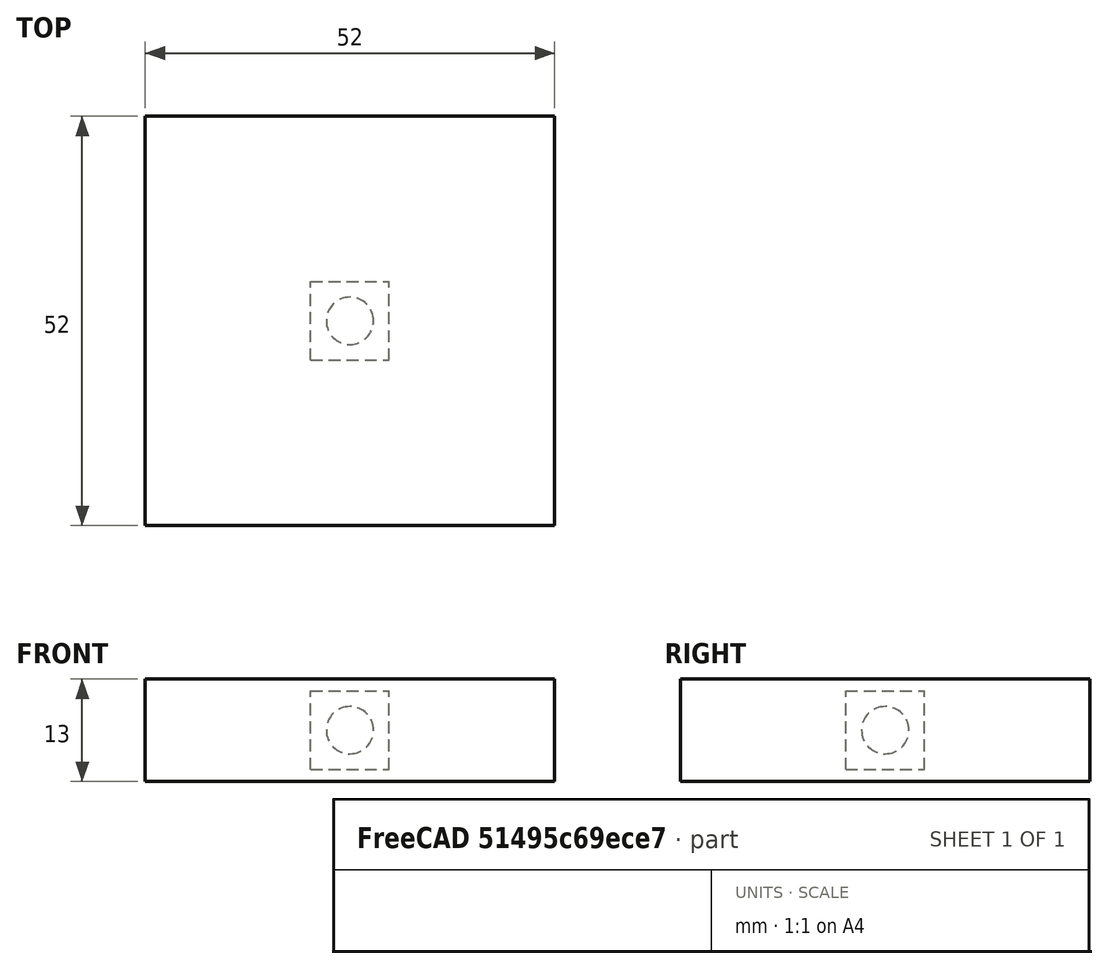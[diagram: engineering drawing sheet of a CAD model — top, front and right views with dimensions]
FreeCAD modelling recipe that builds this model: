
FCSTD DOCUMENT  (FreeCAD 0.21RUnknown)
Label: array-of-mother-daughter-vols-correct
License: All rights reserved
objects: App::DocumentObjectGroupPython×1251, Part::FeaturePython×5, App::Part×3
note: 3 computed .brp shape members not serialized (recipe doc carries the construction recipe); baked Part::Feature solids carry a one-line shape summary decoded from their .brp

FEATURE [App::DocumentObjectGroupPython] HALFPI  # scripted group (container) (typed FeaturePython)
  name = HALFPI
  value = pi/2.
FEATURE [App::DocumentObjectGroupPython] PI  # scripted group (container) (typed FeaturePython)
  name = PI
  value = 1.*pi
FEATURE [App::DocumentObjectGroupPython] TWOPI  # scripted group (container) (typed FeaturePython)
  name = TWOPI
  value = 2.*pi
FEATURE [App::DocumentObjectGroupPython] Constants  # scripted group (container) (typed FeaturePython)
  Group = -> [HALFPI,PI,TWOPI]
FEATURE [App::DocumentObjectGroupPython] Variables  # scripted group (container) (typed FeaturePython)
FEATURE [App::DocumentObjectGroupPython] Quantities  # scripted group (container) (typed FeaturePython)
FEATURE [App::DocumentObjectGroupPython] Isotopes  # scripted group (container) (typed FeaturePython)
FEATURE [App::DocumentObjectGroupPython] Elements  # scripted group (container) (typed FeaturePython)
FEATURE [App::DocumentObjectGroupPython] Matrix  # scripted group (container) (typed FeaturePython)
FEATURE [App::DocumentObjectGroupPython] Surfaces  # scripted group (container) (typed FeaturePython)
FEATURE [App::DocumentObjectGroupPython] Opticals  # scripted group (container) (typed FeaturePython)
  Group = -> [Matrix,Surfaces]
FEATURE [App::DocumentObjectGroupPython] G4Isotopes  # scripted group (container) (typed FeaturePython)
FEATURE [App::DocumentObjectGroupPython] H_element  # scripted group (container) (typed FeaturePython)
  Z = 1
  atom_value = 1.008
  formula = H
  name = H_element
FEATURE [App::DocumentObjectGroupPython] He_element  # scripted group (container) (typed FeaturePython)
  Z = 2
  atom_value = 4.0026
  formula = He
  name = He_element
FEATURE [App::DocumentObjectGroupPython] Li_element  # scripted group (container) (typed FeaturePython)
  Z = 3
  atom_value = 6.94
  formula = Li
  name = Li_element
FEATURE [App::DocumentObjectGroupPython] Be_element  # scripted group (container) (typed FeaturePython)
  Z = 4
  atom_value = 9.01218
  formula = Be
  name = Be_element
FEATURE [App::DocumentObjectGroupPython] B_element  # scripted group (container) (typed FeaturePython)
  Z = 5
  atom_value = 10.81
  formula = B
  name = B_element
FEATURE [App::DocumentObjectGroupPython] C_element  # scripted group (container) (typed FeaturePython)
  Z = 6
  atom_value = 12.011
  formula = C
  name = C_element
FEATURE [App::DocumentObjectGroupPython] N_element  # scripted group (container) (typed FeaturePython)
  Z = 7
  atom_value = 14.007
  formula = N
  name = N_element
FEATURE [App::DocumentObjectGroupPython] O_element  # scripted group (container) (typed FeaturePython)
  Z = 8
  atom_value = 15.999
  formula = O
  name = O_element
FEATURE [App::DocumentObjectGroupPython] F_element  # scripted group (container) (typed FeaturePython)
  Z = 9
  atom_value = 18.9984
  formula = F
  name = F_element
FEATURE [App::DocumentObjectGroupPython] Ne_element  # scripted group (container) (typed FeaturePython)
  Z = 10
  atom_value = 20.1797
  formula = Ne
  name = Ne_element
FEATURE [App::DocumentObjectGroupPython] Na_element  # scripted group (container) (typed FeaturePython)
  Z = 11
  atom_value = 22.9898
  formula = Na
  name = Na_element
FEATURE [App::DocumentObjectGroupPython] Mg_element  # scripted group (container) (typed FeaturePython)
  Z = 12
  atom_value = 24.305
  formula = Mg
  name = Mg_element
FEATURE [App::DocumentObjectGroupPython] Al_element  # scripted group (container) (typed FeaturePython)
  Z = 13
  atom_value = 26.9815
  formula = Al
  name = Al_element
FEATURE [App::DocumentObjectGroupPython] Si_element  # scripted group (container) (typed FeaturePython)
  Z = 14
  atom_value = 28.085
  formula = Si
  name = Si_element
FEATURE [App::DocumentObjectGroupPython] P_element  # scripted group (container) (typed FeaturePython)
  Z = 15
  atom_value = 30.9738
  formula = P
  name = P_element
FEATURE [App::DocumentObjectGroupPython] S_element  # scripted group (container) (typed FeaturePython)
  Z = 16
  atom_value = 32.06
  formula = S
  name = S_element
FEATURE [App::DocumentObjectGroupPython] Cl_element  # scripted group (container) (typed FeaturePython)
  Z = 17
  atom_value = 35.45
  formula = Cl
  name = Cl_element
FEATURE [App::DocumentObjectGroupPython] Ar_element  # scripted group (container) (typed FeaturePython)
  Z = 18
  atom_value = 39.95
  formula = Ar
  name = Ar_element
FEATURE [App::DocumentObjectGroupPython] K_element  # scripted group (container) (typed FeaturePython)
  Z = 19
  atom_value = 39.0983
  formula = K
  name = K_element
FEATURE [App::DocumentObjectGroupPython] Ca_element  # scripted group (container) (typed FeaturePython)
  Z = 20
  atom_value = 40.078
  formula = Ca
  name = Ca_element
FEATURE [App::DocumentObjectGroupPython] Sc_element  # scripted group (container) (typed FeaturePython)
  Z = 21
  atom_value = 44.9559
  formula = Sc
  name = Sc_element
FEATURE [App::DocumentObjectGroupPython] Ti_element  # scripted group (container) (typed FeaturePython)
  Z = 22
  atom_value = 47.867
  formula = Ti
  name = Ti_element
FEATURE [App::DocumentObjectGroupPython] V_element  # scripted group (container) (typed FeaturePython)
  Z = 23
  atom_value = 50.9415
  formula = V
  name = V_element
FEATURE [App::DocumentObjectGroupPython] Cr_element  # scripted group (container) (typed FeaturePython)
  Z = 24
  atom_value = 51.9961
  formula = Cr
  name = Cr_element
FEATURE [App::DocumentObjectGroupPython] Mn_element  # scripted group (container) (typed FeaturePython)
  Z = 25
  atom_value = 54.938
  formula = Mn
  name = Mn_element
FEATURE [App::DocumentObjectGroupPython] Fe_element  # scripted group (container) (typed FeaturePython)
  Z = 26
  atom_value = 55.845
  formula = Fe
  name = Fe_element
FEATURE [App::DocumentObjectGroupPython] Co_element  # scripted group (container) (typed FeaturePython)
  Z = 27
  atom_value = 58.9332
  formula = Co
  name = Co_element
FEATURE [App::DocumentObjectGroupPython] Ni_element  # scripted group (container) (typed FeaturePython)
  Z = 28
  atom_value = 58.6934
  formula = Ni
  name = Ni_element
FEATURE [App::DocumentObjectGroupPython] Cu_element  # scripted group (container) (typed FeaturePython)
  Z = 29
  atom_value = 63.546
  formula = Cu
  name = Cu_element
FEATURE [App::DocumentObjectGroupPython] Zn_element  # scripted group (container) (typed FeaturePython)
  Z = 30
  atom_value = 65.38
  formula = Zn
  name = Zn_element
FEATURE [App::DocumentObjectGroupPython] Ga_element  # scripted group (container) (typed FeaturePython)
  Z = 31
  atom_value = 69.723
  formula = Ga
  name = Ga_element
FEATURE [App::DocumentObjectGroupPython] Ge_element  # scripted group (container) (typed FeaturePython)
  Z = 32
  atom_value = 72.63
  formula = Ge
  name = Ge_element
FEATURE [App::DocumentObjectGroupPython] As_element  # scripted group (container) (typed FeaturePython)
  Z = 33
  atom_value = 74.9216
  formula = As
  name = As_element
FEATURE [App::DocumentObjectGroupPython] Se_element  # scripted group (container) (typed FeaturePython)
  Z = 34
  atom_value = 78.971
  formula = Se
  name = Se_element
FEATURE [App::DocumentObjectGroupPython] Br_element  # scripted group (container) (typed FeaturePython)
  Z = 35
  atom_value = 79.904
  formula = Br
  name = Br_element
FEATURE [App::DocumentObjectGroupPython] Kr_element  # scripted group (container) (typed FeaturePython)
  Z = 36
  atom_value = 83.798
  formula = Kr
  name = Kr_element
FEATURE [App::DocumentObjectGroupPython] Rb_element  # scripted group (container) (typed FeaturePython)
  Z = 37
  atom_value = 85.4678
  formula = Rb
  name = Rb_element
FEATURE [App::DocumentObjectGroupPython] Sr_element  # scripted group (container) (typed FeaturePython)
  Z = 38
  atom_value = 87.62
  formula = Sr
  name = Sr_element
FEATURE [App::DocumentObjectGroupPython] Y_element  # scripted group (container) (typed FeaturePython)
  Z = 39
  atom_value = 88.9058
  formula = Y
  name = Y_element
FEATURE [App::DocumentObjectGroupPython] Zr_element  # scripted group (container) (typed FeaturePython)
  Z = 40
  atom_value = 91.224
  formula = Zr
  name = Zr_element
FEATURE [App::DocumentObjectGroupPython] Nb_element  # scripted group (container) (typed FeaturePython)
  Z = 41
  atom_value = 92.9064
  formula = Nb
  name = Nb_element
FEATURE [App::DocumentObjectGroupPython] Mo_element  # scripted group (container) (typed FeaturePython)
  Z = 42
  atom_value = 95.95
  formula = Mo
  name = Mo_element
FEATURE [App::DocumentObjectGroupPython] Tc_element  # scripted group (container) (typed FeaturePython)
  Z = 43
  atom_value = 97
  formula = Tc
  name = Tc_element
FEATURE [App::DocumentObjectGroupPython] Ru_element  # scripted group (container) (typed FeaturePython)
  Z = 44
  atom_value = 101.07
  formula = Ru
  name = Ru_element
FEATURE [App::DocumentObjectGroupPython] Rh_element  # scripted group (container) (typed FeaturePython)
  Z = 45
  atom_value = 102.905
  formula = Rh
  name = Rh_element
FEATURE [App::DocumentObjectGroupPython] Pd_element  # scripted group (container) (typed FeaturePython)
  Z = 46
  atom_value = 106.42
  formula = Pd
  name = Pd_element
FEATURE [App::DocumentObjectGroupPython] Ag_element  # scripted group (container) (typed FeaturePython)
  Z = 47
  atom_value = 107.868
  formula = Ag
  name = Ag_element
FEATURE [App::DocumentObjectGroupPython] Cd_element  # scripted group (container) (typed FeaturePython)
  Z = 48
  atom_value = 112.414
  formula = Cd
  name = Cd_element
FEATURE [App::DocumentObjectGroupPython] In_element  # scripted group (container) (typed FeaturePython)
  Z = 49
  atom_value = 114.818
  formula = In
  name = In_element
FEATURE [App::DocumentObjectGroupPython] Sn_element  # scripted group (container) (typed FeaturePython)
  Z = 50
  atom_value = 118.71
  formula = Sn
  name = Sn_element
FEATURE [App::DocumentObjectGroupPython] Sb_element  # scripted group (container) (typed FeaturePython)
  Z = 51
  atom_value = 121.76
  formula = Sb
  name = Sb_element
FEATURE [App::DocumentObjectGroupPython] Te_element  # scripted group (container) (typed FeaturePython)
  Z = 52
  atom_value = 127.6
  formula = Te
  name = Te_element
FEATURE [App::DocumentObjectGroupPython] I_element  # scripted group (container) (typed FeaturePython)
  Z = 53
  atom_value = 126.904
  formula = I
  name = I_element
FEATURE [App::DocumentObjectGroupPython] Xe_element  # scripted group (container) (typed FeaturePython)
  Z = 54
  atom_value = 131.293
  formula = Xe
  name = Xe_element
FEATURE [App::DocumentObjectGroupPython] Cs_element  # scripted group (container) (typed FeaturePython)
  Z = 55
  atom_value = 132.905
  formula = Cs
  name = Cs_element
FEATURE [App::DocumentObjectGroupPython] Ba_element  # scripted group (container) (typed FeaturePython)
  Z = 56
  atom_value = 137.327
  formula = Ba
  name = Ba_element
FEATURE [App::DocumentObjectGroupPython] La_element  # scripted group (container) (typed FeaturePython)
  Z = 57
  atom_value = 138.905
  formula = La
  name = La_element
FEATURE [App::DocumentObjectGroupPython] Ce_element  # scripted group (container) (typed FeaturePython)
  Z = 58
  atom_value = 140.116
  formula = Ce
  name = Ce_element
FEATURE [App::DocumentObjectGroupPython] Pr_element  # scripted group (container) (typed FeaturePython)
  Z = 59
  atom_value = 140.908
  formula = Pr
  name = Pr_element
FEATURE [App::DocumentObjectGroupPython] Nd_element  # scripted group (container) (typed FeaturePython)
  Z = 60
  atom_value = 144.242
  formula = Nd
  name = Nd_element
FEATURE [App::DocumentObjectGroupPython] Pm_element  # scripted group (container) (typed FeaturePython)
  Z = 61
  atom_value = 145
  formula = Pm
  name = Pm_element
FEATURE [App::DocumentObjectGroupPython] Sm_element  # scripted group (container) (typed FeaturePython)
  Z = 62
  atom_value = 150.36
  formula = Sm
  name = Sm_element
FEATURE [App::DocumentObjectGroupPython] Eu_element  # scripted group (container) (typed FeaturePython)
  Z = 63
  atom_value = 151.964
  formula = Eu
  name = Eu_element
FEATURE [App::DocumentObjectGroupPython] Gd_element  # scripted group (container) (typed FeaturePython)
  Z = 64
  atom_value = 157.25
  formula = Gd
  name = Gd_element
FEATURE [App::DocumentObjectGroupPython] Tb_element  # scripted group (container) (typed FeaturePython)
  Z = 65
  atom_value = 158.925
  formula = Tb
  name = Tb_element
FEATURE [App::DocumentObjectGroupPython] Dy_element  # scripted group (container) (typed FeaturePython)
  Z = 66
  atom_value = 162.5
  formula = Dy
  name = Dy_element
FEATURE [App::DocumentObjectGroupPython] Ho_element  # scripted group (container) (typed FeaturePython)
  Z = 67
  atom_value = 164.93
  formula = Ho
  name = Ho_element
FEATURE [App::DocumentObjectGroupPython] Er_element  # scripted group (container) (typed FeaturePython)
  Z = 68
  atom_value = 167.259
  formula = Er
  name = Er_element
FEATURE [App::DocumentObjectGroupPython] Tm_element  # scripted group (container) (typed FeaturePython)
  Z = 69
  atom_value = 168.934
  formula = Tm
  name = Tm_element
FEATURE [App::DocumentObjectGroupPython] Yb_element  # scripted group (container) (typed FeaturePython)
  Z = 70
  atom_value = 173.045
  formula = Yb
  name = Yb_element
FEATURE [App::DocumentObjectGroupPython] Lu_element  # scripted group (container) (typed FeaturePython)
  Z = 71
  atom_value = 174.967
  formula = Lu
  name = Lu_element
FEATURE [App::DocumentObjectGroupPython] Hf_element  # scripted group (container) (typed FeaturePython)
  Z = 72
  atom_value = 178.49
  formula = Hf
  name = Hf_element
FEATURE [App::DocumentObjectGroupPython] Ta_element  # scripted group (container) (typed FeaturePython)
  Z = 73
  atom_value = 180.948
  formula = Ta
  name = Ta_element
FEATURE [App::DocumentObjectGroupPython] W_element  # scripted group (container) (typed FeaturePython)
  Z = 74
  atom_value = 183.84
  formula = W
  name = W_element
FEATURE [App::DocumentObjectGroupPython] Re_element  # scripted group (container) (typed FeaturePython)
  Z = 75
  atom_value = 186.207
  formula = Re
  name = Re_element
FEATURE [App::DocumentObjectGroupPython] Os_element  # scripted group (container) (typed FeaturePython)
  Z = 76
  atom_value = 190.23
  formula = Os
  name = Os_element
FEATURE [App::DocumentObjectGroupPython] Ir_element  # scripted group (container) (typed FeaturePython)
  Z = 77
  atom_value = 192.217
  formula = Ir
  name = Ir_element
FEATURE [App::DocumentObjectGroupPython] Pt_element  # scripted group (container) (typed FeaturePython)
  Z = 78
  atom_value = 195.084
  formula = Pt
  name = Pt_element
FEATURE [App::DocumentObjectGroupPython] Au_element  # scripted group (container) (typed FeaturePython)
  Z = 79
  atom_value = 196.967
  formula = Au
  name = Au_element
FEATURE [App::DocumentObjectGroupPython] Hg_element  # scripted group (container) (typed FeaturePython)
  Z = 80
  atom_value = 200.592
  formula = Hg
  name = Hg_element
FEATURE [App::DocumentObjectGroupPython] Tl_element  # scripted group (container) (typed FeaturePython)
  Z = 81
  atom_value = 204.38
  formula = Tl
  name = Tl_element
FEATURE [App::DocumentObjectGroupPython] Pb_element  # scripted group (container) (typed FeaturePython)
  Z = 82
  atom_value = 207.2
  formula = Pb
  name = Pb_element
FEATURE [App::DocumentObjectGroupPython] Bi_element  # scripted group (container) (typed FeaturePython)
  Z = 83
  atom_value = 208.98
  formula = Bi
  name = Bi_element
FEATURE [App::DocumentObjectGroupPython] Po_element  # scripted group (container) (typed FeaturePython)
  Z = 84
  atom_value = 209
  formula = Po
  name = Po_element
FEATURE [App::DocumentObjectGroupPython] At_element  # scripted group (container) (typed FeaturePython)
  Z = 85
  atom_value = 210
  formula = At
  name = At_element
FEATURE [App::DocumentObjectGroupPython] Rn_element  # scripted group (container) (typed FeaturePython)
  Z = 86
  atom_value = 222
  formula = Rn
  name = Rn_element
FEATURE [App::DocumentObjectGroupPython] Fr_element  # scripted group (container) (typed FeaturePython)
  Z = 87
  atom_value = 223
  formula = Fr
  name = Fr_element
FEATURE [App::DocumentObjectGroupPython] Ra_element  # scripted group (container) (typed FeaturePython)
  Z = 88
  atom_value = 226
  formula = Ra
  name = Ra_element
FEATURE [App::DocumentObjectGroupPython] Ac_element  # scripted group (container) (typed FeaturePython)
  Z = 89
  atom_value = 227
  formula = Ac
  name = Ac_element
FEATURE [App::DocumentObjectGroupPython] Th_element  # scripted group (container) (typed FeaturePython)
  Z = 90
  atom_value = 232.038
  formula = Th
  name = Th_element
FEATURE [App::DocumentObjectGroupPython] Pa_element  # scripted group (container) (typed FeaturePython)
  Z = 91
  atom_value = 231.036
  formula = Pa
  name = Pa_element
FEATURE [App::DocumentObjectGroupPython] U_element  # scripted group (container) (typed FeaturePython)
  Z = 92
  atom_value = 238.029
  formula = U
  name = U_element
FEATURE [App::DocumentObjectGroupPython] Np_element  # scripted group (container) (typed FeaturePython)
  Z = 93
  atom_value = 237
  formula = Np
  name = Np_element
FEATURE [App::DocumentObjectGroupPython] Pu_element  # scripted group (container) (typed FeaturePython)
  Z = 94
  atom_value = 244
  formula = Pu
  name = Pu_element
FEATURE [App::DocumentObjectGroupPython] Am_element  # scripted group (container) (typed FeaturePython)
  Z = 95
  atom_value = 243
  formula = Am
  name = Am_element
FEATURE [App::DocumentObjectGroupPython] Cm_element  # scripted group (container) (typed FeaturePython)
  Z = 96
  atom_value = 247
  formula = Cm
  name = Cm_element
FEATURE [App::DocumentObjectGroupPython] Bk_element  # scripted group (container) (typed FeaturePython)
  Z = 97
  atom_value = 247
  formula = Bk
  name = Bk_element
FEATURE [App::DocumentObjectGroupPython] Cf_element  # scripted group (container) (typed FeaturePython)
  Z = 98
  atom_value = 251
  formula = Cf
  name = Cf_element
FEATURE [App::DocumentObjectGroupPython] G4Elements  # scripted group (container) (typed FeaturePython)
  Group = -> [H_element,He_element,Li_element,Be_element,B_element,C_element,N_element,O_element,F_element,Ne_element,Na_element,Mg_element,Al_element,Si_element,P_element,S_element,Cl_element,Ar_element,K_element,Ca_element,Sc_element,Ti_element,V_element,Cr_element,Mn_element,Fe_element,Co_element,Ni_element,Cu_element,Zn_element,Ga_element,Ge_element,As_element,Se_element,Br_element,Kr_element,Rb_element,+61 more]
FEATURE [App::DocumentObjectGroupPython] H_element001  label="H_element : 0.101"  # scripted group (container) (typed FeaturePython)
  n = 0.101327
FEATURE [App::DocumentObjectGroupPython] C_element001  label="C_element : 0.775"  # scripted group (container) (typed FeaturePython)
  n = 0.7755
FEATURE [App::DocumentObjectGroupPython] N_element001  label="N_element : 0.035"  # scripted group (container) (typed FeaturePython)
  n = 0.035057
FEATURE [App::DocumentObjectGroupPython] O_element001  label="O_element : 0.052"  # scripted group (container) (typed FeaturePython)
  n = 0.0523159
FEATURE [App::DocumentObjectGroupPython] F_element001  label="F_element : 0.017"  # scripted group (container) (typed FeaturePython)
  n = 0.017422
FEATURE [App::DocumentObjectGroupPython] Ca_element001  label="Ca_element : 0.018"  # scripted group (container) (typed FeaturePython)
  n = 0.018378
FEATURE [App::DocumentObjectGroupPython] G4_A_150_TISSUE  label="G4_A-150_TISSUE"  # scripted group (container) (typed FeaturePython)
  Dunit = g/cm3
  Dvalue = 1.127
  Group = -> [H_element001,C_element001,N_element001,O_element001,F_element001,Ca_element001]
  conduct = 2
  density = 1
  expand = 3
  formula = G4_A-150_TISSUE
  name = G4_A-150_TISSUE
  specific = 4
FEATURE [App::DocumentObjectGroupPython] C_element002  label="C_element : 3"  # scripted group (container) (typed FeaturePython)
  n = 3
  ref = C_element
FEATURE [App::DocumentObjectGroupPython] H_element002  label="H_element : 6"  # scripted group (container) (typed FeaturePython)
  n = 6
  ref = H_element
FEATURE [App::DocumentObjectGroupPython] O_element002  label="O_element : 1"  # scripted group (container) (typed FeaturePython)
  n = 1
  ref = O_element
FEATURE [App::DocumentObjectGroupPython] G4_ACETONE  # scripted group (container) (typed FeaturePython)
  Dunit = g/cm3
  Dvalue = 0.7899
  Group = -> [C_element002,H_element002,O_element002]
  conduct = 2
  density = 1
  expand = 3
  formula = G4_ACETONE
  name = G4_ACETONE
  specific = 4
FEATURE [App::DocumentObjectGroupPython] C_element003  label="C_element : 2"  # scripted group (container) (typed FeaturePython)
  n = 2
  ref = C_element
FEATURE [App::DocumentObjectGroupPython] H_element003  label="H_element : 2"  # scripted group (container) (typed FeaturePython)
  n = 2
  ref = H_element
FEATURE [App::DocumentObjectGroupPython] G4_ACETYLENE  # scripted group (container) (typed FeaturePython)
  Dunit = g/cm3
  Dvalue = 0.0010967
  Group = -> [C_element003,H_element003]
  conduct = 2
  density = 1
  expand = 3
  formula = G4_ACETYLENE
  name = G4_ACETYLENE
  specific = 4
FEATURE [App::DocumentObjectGroupPython] C_element004  label="C_element : 5"  # scripted group (container) (typed FeaturePython)
  n = 5
  ref = C_element
FEATURE [App::DocumentObjectGroupPython] H_element004  label="H_element : 5"  # scripted group (container) (typed FeaturePython)
  n = 5
  ref = H_element
FEATURE [App::DocumentObjectGroupPython] N_element002  label="N_element : 5"  # scripted group (container) (typed FeaturePython)
  n = 5
  ref = N_element
FEATURE [App::DocumentObjectGroupPython] G4_ADENINE  # scripted group (container) (typed FeaturePython)
  Dunit = g/cm3
  Dvalue = 1.6
  Group = -> [C_element004,H_element004,N_element002]
  conduct = 2
  density = 1
  expand = 3
  formula = G4_ADENINE
  name = G4_ADENINE
  specific = 4
FEATURE [App::DocumentObjectGroupPython] H_element005  label="H_element : 0.114"  # scripted group (container) (typed FeaturePython)
  n = 0.114
FEATURE [App::DocumentObjectGroupPython] C_element005  label="C_element : 0.598"  # scripted group (container) (typed FeaturePython)
  n = 0.598
FEATURE [App::DocumentObjectGroupPython] N_element003  label="N_element : 0.007"  # scripted group (container) (typed FeaturePython)
  n = 0.007
FEATURE [App::DocumentObjectGroupPython] O_element003  label="O_element : 0.278"  # scripted group (container) (typed FeaturePython)
  n = 0.278
FEATURE [App::DocumentObjectGroupPython] Na_element001  label="Na_element : 0.001"  # scripted group (container) (typed FeaturePython)
  n = 0.001
FEATURE [App::DocumentObjectGroupPython] S_element001  label="S_element : 0.001"  # scripted group (container) (typed FeaturePython)
  n = 0.001
FEATURE [App::DocumentObjectGroupPython] Cl_element001  label="Cl_element : 0.001"  # scripted group (container) (typed FeaturePython)
  n = 0.001
FEATURE [App::DocumentObjectGroupPython] G4_ADIPOSE_TISSUE_ICRP  # scripted group (container) (typed FeaturePython)
  Dunit = g/cm3
  Dvalue = 0.95
  Group = -> [H_element005,C_element005,N_element003,O_element003,Na_element001,S_element001,Cl_element001]
  conduct = 2
  density = 1
  expand = 3
  formula = G4_ADIPOSE_TISSUE_ICRP
  name = G4_ADIPOSE_TISSUE_ICRP
  specific = 4
FEATURE [App::DocumentObjectGroupPython] C_element006  label="C_element : 0.000"  # scripted group (container) (typed FeaturePython)
  n = 0.000124
FEATURE [App::DocumentObjectGroupPython] N_element004  label="N_element : 0.755"  # scripted group (container) (typed FeaturePython)
  n = 0.755268
FEATURE [App::DocumentObjectGroupPython] O_element004  label="O_element : 0.232"  # scripted group (container) (typed FeaturePython)
  n = 0.231781
FEATURE [App::DocumentObjectGroupPython] Ar_element001  label="Ar_element : 0.013"  # scripted group (container) (typed FeaturePython)
  n = 0.012827
FEATURE [App::DocumentObjectGroupPython] G4_AIR  # scripted group (container) (typed FeaturePython)
  Dunit = g/cm3
  Dvalue = 0.00120479
  Group = -> [C_element006,N_element004,O_element004,Ar_element001]
  conduct = 2
  density = 1
  expand = 3
  formula = G4_AIR
  name = G4_AIR
  specific = 4
FEATURE [App::DocumentObjectGroupPython] C_element007  label="C_element : 006"  # scripted group (container) (typed FeaturePython)
  n = 3
  ref = C_element
FEATURE [App::DocumentObjectGroupPython] H_element006  label="H_element : 7"  # scripted group (container) (typed FeaturePython)
  n = 7
  ref = H_element
FEATURE [App::DocumentObjectGroupPython] N_element005  label="N_element : 1"  # scripted group (container) (typed FeaturePython)
  n = 1
  ref = N_element
FEATURE [App::DocumentObjectGroupPython] O_element005  label="O_element : 2"  # scripted group (container) (typed FeaturePython)
  n = 2
  ref = O_element
FEATURE [App::DocumentObjectGroupPython] G4_ALANINE  # scripted group (container) (typed FeaturePython)
  Dunit = g/cm3
  Dvalue = 1.42
  Group = -> [C_element007,H_element006,N_element005,O_element005]
  conduct = 2
  density = 1
  expand = 3
  formula = G4_ALANINE
  name = G4_ALANINE
  specific = 4
FEATURE [App::DocumentObjectGroupPython] Al_element001  label="Al_element : 2"  # scripted group (container) (typed FeaturePython)
  n = 2
  ref = Al_element
FEATURE [App::DocumentObjectGroupPython] O_element006  label="O_element : 3"  # scripted group (container) (typed FeaturePython)
  n = 3
  ref = O_element
FEATURE [App::DocumentObjectGroupPython] G4_ALUMINUM_OXIDE  # scripted group (container) (typed FeaturePython)
  Dunit = g/cm3
  Dvalue = 3.97
  Group = -> [Al_element001,O_element006]
  conduct = 2
  density = 1
  expand = 3
  formula = G4_ALUMINUM_OXIDE
  name = G4_ALUMINUM_OXIDE
  specific = 4
FEATURE [App::DocumentObjectGroupPython] H_element007  label="H_element : 0.106"  # scripted group (container) (typed FeaturePython)
  n = 0.10593
FEATURE [App::DocumentObjectGroupPython] C_element008  label="C_element : 0.789"  # scripted group (container) (typed FeaturePython)
  n = 0.788974
FEATURE [App::DocumentObjectGroupPython] O_element007  label="O_element : 0.105"  # scripted group (container) (typed FeaturePython)
  n = 0.105096
FEATURE [App::DocumentObjectGroupPython] G4_AMBER  # scripted group (container) (typed FeaturePython)
  Dunit = g/cm3
  Dvalue = 1.1
  Group = -> [H_element007,C_element008,O_element007]
  conduct = 2
  density = 1
  expand = 3
  formula = G4_AMBER
  name = G4_AMBER
  specific = 4
FEATURE [App::DocumentObjectGroupPython] N_element006  label="N_element : 006"  # scripted group (container) (typed FeaturePython)
  n = 1
  ref = N_element
FEATURE [App::DocumentObjectGroupPython] H_element008  label="H_element : 3"  # scripted group (container) (typed FeaturePython)
  n = 3
  ref = H_element
FEATURE [App::DocumentObjectGroupPython] G4_AMMONIA  # scripted group (container) (typed FeaturePython)
  Dunit = g/cm3
  Dvalue = 0.000826019
  Group = -> [N_element006,H_element008]
  conduct = 2
  density = 1
  expand = 3
  formula = G4_AMMONIA
  name = G4_AMMONIA
  specific = 4
FEATURE [App::DocumentObjectGroupPython] C_element009  label="C_element : 6"  # scripted group (container) (typed FeaturePython)
  n = 6
  ref = C_element
FEATURE [App::DocumentObjectGroupPython] H_element009  label="H_element : 008"  # scripted group (container) (typed FeaturePython)
  n = 7
  ref = H_element
FEATURE [App::DocumentObjectGroupPython] N_element007  label="N_element : 007"  # scripted group (container) (typed FeaturePython)
  n = 1
  ref = N_element
FEATURE [App::DocumentObjectGroupPython] G4_ANILINE  # scripted group (container) (typed FeaturePython)
  Dunit = g/cm3
  Dvalue = 1.0235
  Group = -> [C_element009,H_element009,N_element007]
  conduct = 2
  density = 1
  expand = 3
  formula = G4_ANILINE
  name = G4_ANILINE
  specific = 4
FEATURE [App::DocumentObjectGroupPython] C_element010  label="C_element : 14"  # scripted group (container) (typed FeaturePython)
  n = 14
  ref = C_element
FEATURE [App::DocumentObjectGroupPython] H_element010  label="H_element : 10"  # scripted group (container) (typed FeaturePython)
  n = 10
  ref = H_element
FEATURE [App::DocumentObjectGroupPython] G4_ANTHRACENE  # scripted group (container) (typed FeaturePython)
  Dunit = g/cm3
  Dvalue = 1.283
  Group = -> [C_element010,H_element010]
  conduct = 2
  density = 1
  expand = 3
  formula = G4_ANTHRACENE
  name = G4_ANTHRACENE
  specific = 4
FEATURE [App::DocumentObjectGroupPython] H_element011  label="H_element : 0.065"  # scripted group (container) (typed FeaturePython)
  n = 0.0654709
FEATURE [App::DocumentObjectGroupPython] C_element011  label="C_element : 0.537"  # scripted group (container) (typed FeaturePython)
  n = 0.536944
FEATURE [App::DocumentObjectGroupPython] N_element008  label="N_element : 0.021"  # scripted group (container) (typed FeaturePython)
  n = 0.0215
FEATURE [App::DocumentObjectGroupPython] O_element008  label="O_element : 0.032"  # scripted group (container) (typed FeaturePython)
  n = 0.032085
FEATURE [App::DocumentObjectGroupPython] F_element002  label="F_element : 0.167"  # scripted group (container) (typed FeaturePython)
  n = 0.167411
FEATURE [App::DocumentObjectGroupPython] Ca_element002  label="Ca_element : 0.177"  # scripted group (container) (typed FeaturePython)
  n = 0.176589
FEATURE [App::DocumentObjectGroupPython] G4_B_100_BONE  label="G4_B-100_BONE"  # scripted group (container) (typed FeaturePython)
  Dunit = g/cm3
  Dvalue = 1.45
  Group = -> [H_element011,C_element011,N_element008,O_element008,F_element002,Ca_element002]
  conduct = 2
  density = 1
  expand = 3
  formula = G4_B-100_BONE
  name = G4_B-100_BONE
  specific = 4
FEATURE [App::DocumentObjectGroupPython] H_element012  label="H_element : 0.057"  # scripted group (container) (typed FeaturePython)
  n = 0.057441
FEATURE [App::DocumentObjectGroupPython] C_element012  label="C_element : 0.790"  # scripted group (container) (typed FeaturePython)
  n = 0.774591
FEATURE [App::DocumentObjectGroupPython] O_element009  label="O_element : 0.168"  # scripted group (container) (typed FeaturePython)
  n = 0.167968
FEATURE [App::DocumentObjectGroupPython] G4_BAKELITE  # scripted group (container) (typed FeaturePython)
  Dunit = g/cm3
  Dvalue = 1.25
  Group = -> [H_element012,C_element012,O_element009]
  conduct = 2
  density = 1
  expand = 3
  formula = G4_BAKELITE
  name = G4_BAKELITE
  specific = 4
FEATURE [App::DocumentObjectGroupPython] Ba_element001  label="Ba_element : 1"  # scripted group (container) (typed FeaturePython)
  n = 1
  ref = Ba_element
FEATURE [App::DocumentObjectGroupPython] F_element003  label="F_element : 2"  # scripted group (container) (typed FeaturePython)
  n = 2
  ref = F_element
FEATURE [App::DocumentObjectGroupPython] G4_BARIUM_FLUORIDE  # scripted group (container) (typed FeaturePython)
  Dunit = g/cm3
  Dvalue = 4.89
  Group = -> [Ba_element001,F_element003]
  conduct = 2
  density = 1
  expand = 3
  formula = G4_BARIUM_FLUORIDE
  name = G4_BARIUM_FLUORIDE
  specific = 4
FEATURE [App::DocumentObjectGroupPython] Ba_element002  label="Ba_element : 002"  # scripted group (container) (typed FeaturePython)
  n = 1
  ref = Ba_element
FEATURE [App::DocumentObjectGroupPython] S_element002  label="S_element : 1"  # scripted group (container) (typed FeaturePython)
  n = 1
  ref = S_element
FEATURE [App::DocumentObjectGroupPython] O_element010  label="O_element : 4"  # scripted group (container) (typed FeaturePython)
  n = 4
  ref = O_element
FEATURE [App::DocumentObjectGroupPython] G4_BARIUM_SULFATE  # scripted group (container) (typed FeaturePython)
  Dunit = g/cm3
  Dvalue = 4.5
  Group = -> [Ba_element002,S_element002,O_element010]
  conduct = 2
  density = 1
  expand = 3
  formula = G4_BARIUM_SULFATE
  name = G4_BARIUM_SULFATE
  specific = 4
FEATURE [App::DocumentObjectGroupPython] C_element013  label="C_element : 007"  # scripted group (container) (typed FeaturePython)
  n = 6
  ref = C_element
FEATURE [App::DocumentObjectGroupPython] H_element013  label="H_element : 009"  # scripted group (container) (typed FeaturePython)
  n = 6
  ref = H_element
FEATURE [App::DocumentObjectGroupPython] G4_BENZENE  # scripted group (container) (typed FeaturePython)
  Dunit = g/cm3
  Dvalue = 0.87865
  Group = -> [C_element013,H_element013]
  conduct = 2
  density = 1
  expand = 3
  formula = G4_BENZENE
  name = G4_BENZENE
  specific = 4
FEATURE [App::DocumentObjectGroupPython] Be_element001  label="Be_element : 1"  # scripted group (container) (typed FeaturePython)
  n = 1
  ref = Be_element
FEATURE [App::DocumentObjectGroupPython] O_element011  label="O_element : 005"  # scripted group (container) (typed FeaturePython)
  n = 1
  ref = O_element
FEATURE [App::DocumentObjectGroupPython] G4_BERYLLIUM_OXIDE  # scripted group (container) (typed FeaturePython)
  Dunit = g/cm3
  Dvalue = 3.01
  Group = -> [Be_element001,O_element011]
  conduct = 2
  density = 1
  expand = 3
  formula = G4_BERYLLIUM_OXIDE
  name = G4_BERYLLIUM_OXIDE
  specific = 4
FEATURE [App::DocumentObjectGroupPython] Bi_element001  label="Bi_element : 4"  # scripted group (container) (typed FeaturePython)
  n = 4
  ref = Bi_element
FEATURE [App::DocumentObjectGroupPython] Ge_element001  label="Ge_element : 3"  # scripted group (container) (typed FeaturePython)
  n = 3
  ref = Ge_element
FEATURE [App::DocumentObjectGroupPython] O_element012  label="O_element : 12"  # scripted group (container) (typed FeaturePython)
  n = 12
  ref = O_element
FEATURE [App::DocumentObjectGroupPython] G4_BGO  # scripted group (container) (typed FeaturePython)
  Dunit = g/cm3
  Dvalue = 7.13
  Group = -> [Bi_element001,Ge_element001,O_element012]
  conduct = 2
  density = 1
  expand = 3
  formula = G4_BGO
  name = G4_BGO
  specific = 4
FEATURE [App::DocumentObjectGroupPython] H_element014  label="H_element : 0.102"  # scripted group (container) (typed FeaturePython)
  n = 0.102
FEATURE [App::DocumentObjectGroupPython] C_element014  label="C_element : 0.110"  # scripted group (container) (typed FeaturePython)
  n = 0.11
FEATURE [App::DocumentObjectGroupPython] N_element009  label="N_element : 0.033"  # scripted group (container) (typed FeaturePython)
  n = 0.033
FEATURE [App::DocumentObjectGroupPython] O_element013  label="O_element : 0.745"  # scripted group (container) (typed FeaturePython)
  n = 0.745
FEATURE [App::DocumentObjectGroupPython] Na_element002  label="Na_element : 0.002"  # scripted group (container) (typed FeaturePython)
  n = 0.001
FEATURE [App::DocumentObjectGroupPython] P_element001  label="P_element : 0.001"  # scripted group (container) (typed FeaturePython)
  n = 0.001
FEATURE [App::DocumentObjectGroupPython] S_element003  label="S_element : 0.002"  # scripted group (container) (typed FeaturePython)
  n = 0.002
FEATURE [App::DocumentObjectGroupPython] Cl_element002  label="Cl_element : 0.003"  # scripted group (container) (typed FeaturePython)
  n = 0.003
FEATURE [App::DocumentObjectGroupPython] K_element001  label="K_element : 0.002"  # scripted group (container) (typed FeaturePython)
  n = 0.002
FEATURE [App::DocumentObjectGroupPython] Fe_element001  label="Fe_element : 0.001"  # scripted group (container) (typed FeaturePython)
  n = 0.001
FEATURE [App::DocumentObjectGroupPython] G4_BLOOD_ICRP  # scripted group (container) (typed FeaturePython)
  Dunit = g/cm3
  Dvalue = 1.06
  Group = -> [H_element014,C_element014,N_element009,O_element013,Na_element002,P_element001,S_element003,Cl_element002,K_element001,Fe_element001]
  conduct = 2
  density = 1
  expand = 3
  formula = G4_BLOOD_ICRP
  name = G4_BLOOD_ICRP
  specific = 4
FEATURE [App::DocumentObjectGroupPython] H_element015  label="H_element : 0.064"  # scripted group (container) (typed FeaturePython)
  n = 0.064
FEATURE [App::DocumentObjectGroupPython] C_element015  label="C_element : 0.278"  # scripted group (container) (typed FeaturePython)
  n = 0.278
FEATURE [App::DocumentObjectGroupPython] N_element010  label="N_element : 0.027"  # scripted group (container) (typed FeaturePython)
  n = 0.027
FEATURE [App::DocumentObjectGroupPython] O_element014  label="O_element : 0.410"  # scripted group (container) (typed FeaturePython)
  n = 0.41
FEATURE [App::DocumentObjectGroupPython] Mg_element001  label="Mg_element : 0.002"  # scripted group (container) (typed FeaturePython)
  n = 0.002
FEATURE [App::DocumentObjectGroupPython] P_element002  label="P_element : 0.070"  # scripted group (container) (typed FeaturePython)
  n = 0.07
FEATURE [App::DocumentObjectGroupPython] S_element004  label="S_element : 0.003"  # scripted group (container) (typed FeaturePython)
  n = 0.002
FEATURE [App::DocumentObjectGroupPython] Ca_element003  label="Ca_element : 0.147"  # scripted group (container) (typed FeaturePython)
  n = 0.147
FEATURE [App::DocumentObjectGroupPython] G4_BONE_COMPACT_ICRU  # scripted group (container) (typed FeaturePython)
  Dunit = g/cm3
  Dvalue = 1.85
  Group = -> [H_element015,C_element015,N_element010,O_element014,Mg_element001,P_element002,S_element004,Ca_element003]
  conduct = 2
  density = 1
  expand = 3
  formula = G4_BONE_COMPACT_ICRU
  name = G4_BONE_COMPACT_ICRU
  specific = 4
FEATURE [App::DocumentObjectGroupPython] H_element016  label="H_element : 0.034"  # scripted group (container) (typed FeaturePython)
  n = 0.034
FEATURE [App::DocumentObjectGroupPython] C_element016  label="C_element : 0.155"  # scripted group (container) (typed FeaturePython)
  n = 0.155
FEATURE [App::DocumentObjectGroupPython] N_element011  label="N_element : 0.042"  # scripted group (container) (typed FeaturePython)
  n = 0.042
FEATURE [App::DocumentObjectGroupPython] O_element015  label="O_element : 0.435"  # scripted group (container) (typed FeaturePython)
  n = 0.435
FEATURE [App::DocumentObjectGroupPython] Na_element003  label="Na_element : 0.003"  # scripted group (container) (typed FeaturePython)
  n = 0.001
FEATURE [App::DocumentObjectGroupPython] Mg_element002  label="Mg_element : 0.003"  # scripted group (container) (typed FeaturePython)
  n = 0.002
FEATURE [App::DocumentObjectGroupPython] P_element003  label="P_element : 0.103"  # scripted group (container) (typed FeaturePython)
  n = 0.103
FEATURE [App::DocumentObjectGroupPython] S_element005  label="S_element : 0.004"  # scripted group (container) (typed FeaturePython)
  n = 0.003
FEATURE [App::DocumentObjectGroupPython] Ca_element004  label="Ca_element : 0.225"  # scripted group (container) (typed FeaturePython)
  n = 0.225
FEATURE [App::DocumentObjectGroupPython] G4_BONE_CORTICAL_ICRP  # scripted group (container) (typed FeaturePython)
  Dunit = g/cm3
  Dvalue = 1.92
  Group = -> [H_element016,C_element016,N_element011,O_element015,Na_element003,Mg_element002,P_element003,S_element005,Ca_element004]
  conduct = 2
  density = 1
  expand = 3
  formula = G4_BONE_CORTICAL_ICRP
  name = G4_BONE_CORTICAL_ICRP
  specific = 4
FEATURE [App::DocumentObjectGroupPython] B_element001  label="B_element : 4"  # scripted group (container) (typed FeaturePython)
  n = 4
  ref = B_element
FEATURE [App::DocumentObjectGroupPython] C_element017  label="C_element : 1"  # scripted group (container) (typed FeaturePython)
  n = 1
  ref = C_element
FEATURE [App::DocumentObjectGroupPython] G4_BORON_CARBIDE  # scripted group (container) (typed FeaturePython)
  Dunit = g/cm3
  Dvalue = 2.52
  Group = -> [B_element001,C_element017]
  conduct = 2
  density = 1
  expand = 3
  formula = G4_BORON_CARBIDE
  name = G4_BORON_CARBIDE
  specific = 4
FEATURE [App::DocumentObjectGroupPython] B_element002  label="B_element : 2"  # scripted group (container) (typed FeaturePython)
  n = 2
  ref = B_element
FEATURE [App::DocumentObjectGroupPython] O_element016  label="O_element : 006"  # scripted group (container) (typed FeaturePython)
  n = 3
  ref = O_element
FEATURE [App::DocumentObjectGroupPython] G4_BORON_OXIDE  # scripted group (container) (typed FeaturePython)
  Dunit = g/cm3
  Dvalue = 1.812
  Group = -> [B_element002,O_element016]
  conduct = 2
  density = 1
  expand = 3
  formula = G4_BORON_OXIDE
  name = G4_BORON_OXIDE
  specific = 4
FEATURE [App::DocumentObjectGroupPython] H_element017  label="H_element : 0.107"  # scripted group (container) (typed FeaturePython)
  n = 0.107
FEATURE [App::DocumentObjectGroupPython] C_element018  label="C_element : 0.145"  # scripted group (container) (typed FeaturePython)
  n = 0.145
FEATURE [App::DocumentObjectGroupPython] N_element012  label="N_element : 0.022"  # scripted group (container) (typed FeaturePython)
  n = 0.022
FEATURE [App::DocumentObjectGroupPython] O_element017  label="O_element : 0.712"  # scripted group (container) (typed FeaturePython)
  n = 0.712
FEATURE [App::DocumentObjectGroupPython] Na_element004  label="Na_element : 0.004"  # scripted group (container) (typed FeaturePython)
  n = 0.002
FEATURE [App::DocumentObjectGroupPython] P_element004  label="P_element : 0.004"  # scripted group (container) (typed FeaturePython)
  n = 0.004
FEATURE [App::DocumentObjectGroupPython] S_element006  label="S_element : 0.005"  # scripted group (container) (typed FeaturePython)
  n = 0.002
FEATURE [App::DocumentObjectGroupPython] Cl_element003  label="Cl_element : 0.004"  # scripted group (container) (typed FeaturePython)
  n = 0.003
FEATURE [App::DocumentObjectGroupPython] K_element002  label="K_element : 0.003"  # scripted group (container) (typed FeaturePython)
  n = 0.003
FEATURE [App::DocumentObjectGroupPython] G4_BRAIN_ICRP  # scripted group (container) (typed FeaturePython)
  Dunit = g/cm3
  Dvalue = 1.04
  Group = -> [H_element017,C_element018,N_element012,O_element017,Na_element004,P_element004,S_element006,Cl_element003,K_element002]
  conduct = 2
  density = 1
  expand = 3
  formula = G4_BRAIN_ICRP
  name = G4_BRAIN_ICRP
  specific = 4
FEATURE [App::DocumentObjectGroupPython] C_element019  label="C_element : 4"  # scripted group (container) (typed FeaturePython)
  n = 4
  ref = C_element
FEATURE [App::DocumentObjectGroupPython] H_element018  label="H_element : 010"  # scripted group (container) (typed FeaturePython)
  n = 10
  ref = H_element
FEATURE [App::DocumentObjectGroupPython] G4_BUTANE  # scripted group (container) (typed FeaturePython)
  Dunit = g/cm3
  Dvalue = 0.00249343
  Group = -> [C_element019,H_element018]
  conduct = 2
  density = 1
  expand = 3
  formula = G4_BUTANE
  name = G4_BUTANE
  specific = 4
FEATURE [App::DocumentObjectGroupPython] C_element020  label="C_element : 008"  # scripted group (container) (typed FeaturePython)
  n = 4
  ref = C_element
FEATURE [App::DocumentObjectGroupPython] H_element019  label="H_element : 011"  # scripted group (container) (typed FeaturePython)
  n = 10
  ref = H_element
FEATURE [App::DocumentObjectGroupPython] O_element018  label="O_element : 007"  # scripted group (container) (typed FeaturePython)
  n = 1
  ref = O_element
FEATURE [App::DocumentObjectGroupPython] G4_N_BUTYL_ALCOHOL  label="G4_N-BUTYL_ALCOHOL"  # scripted group (container) (typed FeaturePython)
  Dunit = g/cm3
  Dvalue = 0.8098
  Group = -> [C_element020,H_element019,O_element018]
  conduct = 2
  density = 1
  expand = 3
  formula = G4_N-BUTYL_ALCOHOL
  name = G4_N-BUTYL_ALCOHOL
  specific = 4
FEATURE [App::DocumentObjectGroupPython] H_element020  label="H_element : 0.025"  # scripted group (container) (typed FeaturePython)
  n = 0.02468
FEATURE [App::DocumentObjectGroupPython] C_element021  label="C_element : 0.502"  # scripted group (container) (typed FeaturePython)
  n = 0.501611
FEATURE [App::DocumentObjectGroupPython] O_element019  label="O_element : 0.005"  # scripted group (container) (typed FeaturePython)
  n = 0.004527
FEATURE [App::DocumentObjectGroupPython] F_element004  label="F_element : 0.465"  # scripted group (container) (typed FeaturePython)
  n = 0.465209
FEATURE [App::DocumentObjectGroupPython] Si_element001  label="Si_element : 0.004"  # scripted group (container) (typed FeaturePython)
  n = 0.003973
FEATURE [App::DocumentObjectGroupPython] G4_C_552  label="G4_C-552"  # scripted group (container) (typed FeaturePython)
  Dunit = g/cm3
  Dvalue = 1.76
  Group = -> [H_element020,C_element021,O_element019,F_element004,Si_element001]
  conduct = 2
  density = 1
  expand = 3
  formula = G4_C-552
  name = G4_C-552
  specific = 4
FEATURE [App::DocumentObjectGroupPython] Cd_element001  label="Cd_element : 1"  # scripted group (container) (typed FeaturePython)
  n = 1
  ref = Cd_element
FEATURE [App::DocumentObjectGroupPython] Te_element001  label="Te_element : 1"  # scripted group (container) (typed FeaturePython)
  n = 1
  ref = Te_element
FEATURE [App::DocumentObjectGroupPython] G4_CADMIUM_TELLURIDE  # scripted group (container) (typed FeaturePython)
  Dunit = g/cm3
  Dvalue = 6.2
  Group = -> [Cd_element001,Te_element001]
  conduct = 2
  density = 1
  expand = 3
  formula = G4_CADMIUM_TELLURIDE
  name = G4_CADMIUM_TELLURIDE
  specific = 4
FEATURE [App::DocumentObjectGroupPython] Cd_element002  label="Cd_element : 002"  # scripted group (container) (typed FeaturePython)
  n = 1
  ref = Cd_element
FEATURE [App::DocumentObjectGroupPython] W_element001  label="W_element : 1"  # scripted group (container) (typed FeaturePython)
  n = 1
  ref = W_element
FEATURE [App::DocumentObjectGroupPython] O_element020  label="O_element : 008"  # scripted group (container) (typed FeaturePython)
  n = 4
  ref = O_element
FEATURE [App::DocumentObjectGroupPython] G4_CADMIUM_TUNGSTATE  # scripted group (container) (typed FeaturePython)
  Dunit = g/cm3
  Dvalue = 7.9
  Group = -> [Cd_element002,W_element001,O_element020]
  conduct = 2
  density = 1
  expand = 3
  formula = G4_CADMIUM_TUNGSTATE
  name = G4_CADMIUM_TUNGSTATE
  specific = 4
FEATURE [App::DocumentObjectGroupPython] Ca_element005  label="Ca_element : 1"  # scripted group (container) (typed FeaturePython)
  n = 1
  ref = Ca_element
FEATURE [App::DocumentObjectGroupPython] C_element022  label="C_element : 009"  # scripted group (container) (typed FeaturePython)
  n = 1
  ref = C_element
FEATURE [App::DocumentObjectGroupPython] O_element021  label="O_element : 009"  # scripted group (container) (typed FeaturePython)
  n = 3
  ref = O_element
FEATURE [App::DocumentObjectGroupPython] G4_CALCIUM_CARBONATE  # scripted group (container) (typed FeaturePython)
  Dunit = g/cm3
  Dvalue = 2.8
  Group = -> [Ca_element005,C_element022,O_element021]
  conduct = 2
  density = 1
  expand = 3
  formula = G4_CALCIUM_CARBONATE
  name = G4_CALCIUM_CARBONATE
  specific = 4
FEATURE [App::DocumentObjectGroupPython] Ca_element006  label="Ca_element : 002"  # scripted group (container) (typed FeaturePython)
  n = 1
  ref = Ca_element
FEATURE [App::DocumentObjectGroupPython] F_element005  label="F_element : 003"  # scripted group (container) (typed FeaturePython)
  n = 2
  ref = F_element
FEATURE [App::DocumentObjectGroupPython] G4_CALCIUM_FLUORIDE  # scripted group (container) (typed FeaturePython)
  Dunit = g/cm3
  Dvalue = 3.18
  Group = -> [Ca_element006,F_element005]
  conduct = 2
  density = 1
  expand = 3
  formula = G4_CALCIUM_FLUORIDE
  name = G4_CALCIUM_FLUORIDE
  specific = 4
FEATURE [App::DocumentObjectGroupPython] Ca_element007  label="Ca_element : 003"  # scripted group (container) (typed FeaturePython)
  n = 1
  ref = Ca_element
FEATURE [App::DocumentObjectGroupPython] O_element022  label="O_element : 010"  # scripted group (container) (typed FeaturePython)
  n = 1
  ref = O_element
FEATURE [App::DocumentObjectGroupPython] G4_CALCIUM_OXIDE  # scripted group (container) (typed FeaturePython)
  Dunit = g/cm3
  Dvalue = 3.3
  Group = -> [Ca_element007,O_element022]
  conduct = 2
  density = 1
  expand = 3
  formula = G4_CALCIUM_OXIDE
  name = G4_CALCIUM_OXIDE
  specific = 4
FEATURE [App::DocumentObjectGroupPython] Ca_element008  label="Ca_element : 004"  # scripted group (container) (typed FeaturePython)
  n = 1
  ref = Ca_element
FEATURE [App::DocumentObjectGroupPython] S_element007  label="S_element : 002"  # scripted group (container) (typed FeaturePython)
  n = 1
  ref = S_element
FEATURE [App::DocumentObjectGroupPython] O_element023  label="O_element : 011"  # scripted group (container) (typed FeaturePython)
  n = 4
  ref = O_element
FEATURE [App::DocumentObjectGroupPython] G4_CALCIUM_SULFATE  # scripted group (container) (typed FeaturePython)
  Dunit = g/cm3
  Dvalue = 2.96
  Group = -> [Ca_element008,S_element007,O_element023]
  conduct = 2
  density = 1
  expand = 3
  formula = G4_CALCIUM_SULFATE
  name = G4_CALCIUM_SULFATE
  specific = 4
FEATURE [App::DocumentObjectGroupPython] Ca_element009  label="Ca_element : 005"  # scripted group (container) (typed FeaturePython)
  n = 1
  ref = Ca_element
FEATURE [App::DocumentObjectGroupPython] W_element002  label="W_element : 002"  # scripted group (container) (typed FeaturePython)
  n = 1
  ref = W_element
FEATURE [App::DocumentObjectGroupPython] O_element024  label="O_element : 012"  # scripted group (container) (typed FeaturePython)
  n = 4
  ref = O_element
FEATURE [App::DocumentObjectGroupPython] G4_CALCIUM_TUNGSTATE  # scripted group (container) (typed FeaturePython)
  Dunit = g/cm3
  Dvalue = 6.062
  Group = -> [Ca_element009,W_element002,O_element024]
  conduct = 2
  density = 1
  expand = 3
  formula = G4_CALCIUM_TUNGSTATE
  name = G4_CALCIUM_TUNGSTATE
  specific = 4
FEATURE [App::DocumentObjectGroupPython] C_element023  label="C_element : 010"  # scripted group (container) (typed FeaturePython)
  n = 1
  ref = C_element
FEATURE [App::DocumentObjectGroupPython] O_element025  label="O_element : 013"  # scripted group (container) (typed FeaturePython)
  n = 2
  ref = O_element
FEATURE [App::DocumentObjectGroupPython] G4_CARBON_DIOXIDE  # scripted group (container) (typed FeaturePython)
  Dunit = g/cm3
  Dvalue = 0.00184212
  Group = -> [C_element023,O_element025]
  conduct = 2
  density = 1
  expand = 3
  formula = G4_CARBON_DIOXIDE
  name = G4_CARBON_DIOXIDE
  specific = 4
FEATURE [App::DocumentObjectGroupPython] C_element024  label="C_element : 011"  # scripted group (container) (typed FeaturePython)
  n = 1
  ref = C_element
FEATURE [App::DocumentObjectGroupPython] Cl_element004  label="Cl_element : 4"  # scripted group (container) (typed FeaturePython)
  n = 4
  ref = Cl_element
FEATURE [App::DocumentObjectGroupPython] G4_CARBON_TETRACHLORIDE  # scripted group (container) (typed FeaturePython)
  Dunit = g/cm3
  Dvalue = 1.594
  Group = -> [C_element024,Cl_element004]
  conduct = 2
  density = 1
  expand = 3
  formula = G4_CARBON_TETRACHLORIDE
  name = G4_CARBON_TETRACHLORIDE
  specific = 4
FEATURE [App::DocumentObjectGroupPython] C_element025  label="C_element : 012"  # scripted group (container) (typed FeaturePython)
  n = 6
  ref = C_element
FEATURE [App::DocumentObjectGroupPython] H_element021  label="H_element : 012"  # scripted group (container) (typed FeaturePython)
  n = 10
  ref = H_element
FEATURE [App::DocumentObjectGroupPython] O_element026  label="O_element : 5"  # scripted group (container) (typed FeaturePython)
  n = 5
  ref = O_element
FEATURE [App::DocumentObjectGroupPython] G4_CELLULOSE_CELLOPHANE  # scripted group (container) (typed FeaturePython)
  Dunit = g/cm3
  Dvalue = 1.42
  Group = -> [C_element025,H_element021,O_element026]
  conduct = 2
  density = 1
  expand = 3
  formula = G4_CELLULOSE_CELLOPHANE
  name = G4_CELLULOSE_CELLOPHANE
  specific = 4
FEATURE [App::DocumentObjectGroupPython] H_element022  label="H_element : 0.067"  # scripted group (container) (typed FeaturePython)
  n = 0.067125
FEATURE [App::DocumentObjectGroupPython] C_element026  label="C_element : 0.545"  # scripted group (container) (typed FeaturePython)
  n = 0.545403
FEATURE [App::DocumentObjectGroupPython] O_element027  label="O_element : 0.387"  # scripted group (container) (typed FeaturePython)
  n = 0.387472
FEATURE [App::DocumentObjectGroupPython] G4_CELLULOSE_BUTYRATE  # scripted group (container) (typed FeaturePython)
  Dunit = g/cm3
  Dvalue = 1.2
  Group = -> [H_element022,C_element026,O_element027]
  conduct = 2
  density = 1
  expand = 3
  formula = G4_CELLULOSE_BUTYRATE
  name = G4_CELLULOSE_BUTYRATE
  specific = 4
FEATURE [App::DocumentObjectGroupPython] H_element023  label="H_element : 0.029"  # scripted group (container) (typed FeaturePython)
  n = 0.029216
FEATURE [App::DocumentObjectGroupPython] C_element027  label="C_element : 0.271"  # scripted group (container) (typed FeaturePython)
  n = 0.271296
FEATURE [App::DocumentObjectGroupPython] N_element013  label="N_element : 0.121"  # scripted group (container) (typed FeaturePython)
  n = 0.121276
FEATURE [App::DocumentObjectGroupPython] O_element028  label="O_element : 0.578"  # scripted group (container) (typed FeaturePython)
  n = 0.578212
FEATURE [App::DocumentObjectGroupPython] G4_CELLULOSE_NITRATE  # scripted group (container) (typed FeaturePython)
  Dunit = g/cm3
  Dvalue = 1.49
  Group = -> [H_element023,C_element027,N_element013,O_element028]
  conduct = 2
  density = 1
  expand = 3
  formula = G4_CELLULOSE_NITRATE
  name = G4_CELLULOSE_NITRATE
  specific = 4
FEATURE [App::DocumentObjectGroupPython] H_element024  label="H_element : 0.108"  # scripted group (container) (typed FeaturePython)
  n = 0.107596
FEATURE [App::DocumentObjectGroupPython] N_element014  label="N_element : 0.001"  # scripted group (container) (typed FeaturePython)
  n = 0.0008
FEATURE [App::DocumentObjectGroupPython] O_element029  label="O_element : 0.875"  # scripted group (container) (typed FeaturePython)
  n = 0.874976
FEATURE [App::DocumentObjectGroupPython] S_element008  label="S_element : 0.015"  # scripted group (container) (typed FeaturePython)
  n = 0.014627
FEATURE [App::DocumentObjectGroupPython] Ce_element001  label="Ce_element : 0.002"  # scripted group (container) (typed FeaturePython)
  n = 0.002001
FEATURE [App::DocumentObjectGroupPython] G4_CERIC_SULFATE  # scripted group (container) (typed FeaturePython)
  Dunit = g/cm3
  Dvalue = 1.03
  Group = -> [H_element024,N_element014,O_element029,S_element008,Ce_element001]
  conduct = 2
  density = 1
  expand = 3
  formula = G4_CERIC_SULFATE
  name = G4_CERIC_SULFATE
  specific = 4
FEATURE [App::DocumentObjectGroupPython] Cs_element001  label="Cs_element : 1"  # scripted group (container) (typed FeaturePython)
  n = 1
  ref = Cs_element
FEATURE [App::DocumentObjectGroupPython] F_element006  label="F_element : 1"  # scripted group (container) (typed FeaturePython)
  n = 1
  ref = F_element
FEATURE [App::DocumentObjectGroupPython] G4_CESIUM_FLUORIDE  # scripted group (container) (typed FeaturePython)
  Dunit = g/cm3
  Dvalue = 4.115
  Group = -> [Cs_element001,F_element006]
  conduct = 2
  density = 1
  expand = 3
  formula = G4_CESIUM_FLUORIDE
  name = G4_CESIUM_FLUORIDE
  specific = 4
FEATURE [App::DocumentObjectGroupPython] Cs_element002  label="Cs_element : 002"  # scripted group (container) (typed FeaturePython)
  n = 1
  ref = Cs_element
FEATURE [App::DocumentObjectGroupPython] I_element001  label="I_element : 1"  # scripted group (container) (typed FeaturePython)
  n = 1
  ref = I_element
FEATURE [App::DocumentObjectGroupPython] G4_CESIUM_IODIDE  # scripted group (container) (typed FeaturePython)
  Dunit = g/cm3
  Dvalue = 4.51
  Group = -> [Cs_element002,I_element001]
  conduct = 2
  density = 1
  expand = 3
  formula = G4_CESIUM_IODIDE
  name = G4_CESIUM_IODIDE
  specific = 4
FEATURE [App::DocumentObjectGroupPython] C_element028  label="C_element : 013"  # scripted group (container) (typed FeaturePython)
  n = 6
  ref = C_element
FEATURE [App::DocumentObjectGroupPython] H_element025  label="H_element : 013"  # scripted group (container) (typed FeaturePython)
  n = 5
  ref = H_element
FEATURE [App::DocumentObjectGroupPython] Cl_element005  label="Cl_element : 1"  # scripted group (container) (typed FeaturePython)
  n = 1
  ref = Cl_element
FEATURE [App::DocumentObjectGroupPython] G4_CHLOROBENZENE  # scripted group (container) (typed FeaturePython)
  Dunit = g/cm3
  Dvalue = 1.1058
  Group = -> [C_element028,H_element025,Cl_element005]
  conduct = 2
  density = 1
  expand = 3
  formula = G4_CHLOROBENZENE
  name = G4_CHLOROBENZENE
  specific = 4
FEATURE [App::DocumentObjectGroupPython] C_element029  label="C_element : 014"  # scripted group (container) (typed FeaturePython)
  n = 1
  ref = C_element
FEATURE [App::DocumentObjectGroupPython] H_element026  label="H_element : 1"  # scripted group (container) (typed FeaturePython)
  n = 1
  ref = H_element
FEATURE [App::DocumentObjectGroupPython] Cl_element006  label="Cl_element : 3"  # scripted group (container) (typed FeaturePython)
  n = 3
  ref = Cl_element
FEATURE [App::DocumentObjectGroupPython] G4_CHLOROFORM  # scripted group (container) (typed FeaturePython)
  Dunit = g/cm3
  Dvalue = 1.4832
  Group = -> [C_element029,H_element026,Cl_element006]
  conduct = 2
  density = 1
  expand = 3
  formula = G4_CHLOROFORM
  name = G4_CHLOROFORM
  specific = 4
FEATURE [App::DocumentObjectGroupPython] H_element027  label="H_element : 0.010"  # scripted group (container) (typed FeaturePython)
  n = 0.01
FEATURE [App::DocumentObjectGroupPython] C_element030  label="C_element : 0.001"  # scripted group (container) (typed FeaturePython)
  n = 0.001
FEATURE [App::DocumentObjectGroupPython] O_element030  label="O_element : 0.529"  # scripted group (container) (typed FeaturePython)
  n = 0.529107
FEATURE [App::DocumentObjectGroupPython] Na_element005  label="Na_element : 0.016"  # scripted group (container) (typed FeaturePython)
  n = 0.016
FEATURE [App::DocumentObjectGroupPython] Mg_element003  label="Mg_element : 0.004"  # scripted group (container) (typed FeaturePython)
  n = 0.002
FEATURE [App::DocumentObjectGroupPython] Al_element002  label="Al_element : 0.034"  # scripted group (container) (typed FeaturePython)
  n = 0.033872
FEATURE [App::DocumentObjectGroupPython] Si_element002  label="Si_element : 0.337"  # scripted group (container) (typed FeaturePython)
  n = 0.337021
FEATURE [App::DocumentObjectGroupPython] K_element003  label="K_element : 0.013"  # scripted group (container) (typed FeaturePython)
  n = 0.013
FEATURE [App::DocumentObjectGroupPython] Ca_element010  label="Ca_element : 0.044"  # scripted group (container) (typed FeaturePython)
  n = 0.044
FEATURE [App::DocumentObjectGroupPython] Fe_element002  label="Fe_element : 0.014"  # scripted group (container) (typed FeaturePython)
  n = 0.014
FEATURE [App::DocumentObjectGroupPython] G4_CONCRETE  # scripted group (container) (typed FeaturePython)
  Dunit = g/cm3
  Dvalue = 2.3
  Group = -> [H_element027,C_element030,O_element030,Na_element005,Mg_element003,Al_element002,Si_element002,K_element003,Ca_element010,Fe_element002]
  conduct = 2
  density = 1
  expand = 3
  formula = G4_CONCRETE
  name = G4_CONCRETE
  specific = 4
FEATURE [App::DocumentObjectGroupPython] C_element031  label="C_element : 015"  # scripted group (container) (typed FeaturePython)
  n = 6
  ref = C_element
FEATURE [App::DocumentObjectGroupPython] H_element028  label="H_element : 12"  # scripted group (container) (typed FeaturePython)
  n = 12
  ref = H_element
FEATURE [App::DocumentObjectGroupPython] G4_CYCLOHEXANE  # scripted group (container) (typed FeaturePython)
  Dunit = g/cm3
  Dvalue = 0.779
  Group = -> [C_element031,H_element028]
  conduct = 2
  density = 1
  expand = 3
  formula = G4_CYCLOHEXANE
  name = G4_CYCLOHEXANE
  specific = 4
FEATURE [App::DocumentObjectGroupPython] C_element032  label="C_element : 016"  # scripted group (container) (typed FeaturePython)
  n = 6
  ref = C_element
FEATURE [App::DocumentObjectGroupPython] H_element029  label="H_element : 4"  # scripted group (container) (typed FeaturePython)
  n = 4
  ref = H_element
FEATURE [App::DocumentObjectGroupPython] Cl_element007  label="Cl_element : 2"  # scripted group (container) (typed FeaturePython)
  n = 2
  ref = Cl_element
FEATURE [App::DocumentObjectGroupPython] G4_1_2_DICHLOROBENZENE  label="G4_1.2-DICHLOROBENZENE"  # scripted group (container) (typed FeaturePython)
  Dunit = g/cm3
  Dvalue = 1.3048
  Group = -> [C_element032,H_element029,Cl_element007]
  conduct = 2
  density = 1
  expand = 3
  formula = G4_1.2-DICHLOROBENZENE
  name = G4_1.2-DICHLOROBENZENE
  specific = 4
FEATURE [App::DocumentObjectGroupPython] C_element033  label="C_element : 017"  # scripted group (container) (typed FeaturePython)
  n = 4
  ref = C_element
FEATURE [App::DocumentObjectGroupPython] H_element030  label="H_element : 8"  # scripted group (container) (typed FeaturePython)
  n = 8
  ref = H_element
FEATURE [App::DocumentObjectGroupPython] O_element031  label="O_element : 014"  # scripted group (container) (typed FeaturePython)
  n = 1
  ref = O_element
FEATURE [App::DocumentObjectGroupPython] Cl_element008  label="Cl_element : 005"  # scripted group (container) (typed FeaturePython)
  n = 2
  ref = Cl_element
FEATURE [App::DocumentObjectGroupPython] G4_DICHLORODIETHYL_ETHER  # scripted group (container) (typed FeaturePython)
  Dunit = g/cm3
  Dvalue = 1.2199
  Group = -> [C_element033,H_element030,O_element031,Cl_element008]
  conduct = 2
  density = 1
  expand = 3
  formula = G4_DICHLORODIETHYL_ETHER
  name = G4_DICHLORODIETHYL_ETHER
  specific = 4
FEATURE [App::DocumentObjectGroupPython] C_element034  label="C_element : 018"  # scripted group (container) (typed FeaturePython)
  n = 2
  ref = C_element
FEATURE [App::DocumentObjectGroupPython] H_element031  label="H_element : 014"  # scripted group (container) (typed FeaturePython)
  n = 4
  ref = H_element
FEATURE [App::DocumentObjectGroupPython] Cl_element009  label="Cl_element : 006"  # scripted group (container) (typed FeaturePython)
  n = 2
  ref = Cl_element
FEATURE [App::DocumentObjectGroupPython] G4_1_2_DICHLOROETHANE  label="G4_1.2-DICHLOROETHANE"  # scripted group (container) (typed FeaturePython)
  Dunit = g/cm3
  Dvalue = 1.2351
  Group = -> [C_element034,H_element031,Cl_element009]
  conduct = 2
  density = 1
  expand = 3
  formula = G4_1.2-DICHLOROETHANE
  name = G4_1.2-DICHLOROETHANE
  specific = 4
FEATURE [App::DocumentObjectGroupPython] C_element035  label="C_element : 019"  # scripted group (container) (typed FeaturePython)
  n = 4
  ref = C_element
FEATURE [App::DocumentObjectGroupPython] H_element032  label="H_element : 015"  # scripted group (container) (typed FeaturePython)
  n = 10
  ref = H_element
FEATURE [App::DocumentObjectGroupPython] O_element032  label="O_element : 015"  # scripted group (container) (typed FeaturePython)
  n = 1
  ref = O_element
FEATURE [App::DocumentObjectGroupPython] G4_DIETHYL_ETHER  # scripted group (container) (typed FeaturePython)
  Dunit = g/cm3
  Dvalue = 0.71378
  Group = -> [C_element035,H_element032,O_element032]
  conduct = 2
  density = 1
  expand = 3
  formula = G4_DIETHYL_ETHER
  name = G4_DIETHYL_ETHER
  specific = 4
FEATURE [App::DocumentObjectGroupPython] C_element036  label="C_element : 020"  # scripted group (container) (typed FeaturePython)
  n = 3
  ref = C_element
FEATURE [App::DocumentObjectGroupPython] H_element033  label="H_element : 016"  # scripted group (container) (typed FeaturePython)
  n = 7
  ref = H_element
FEATURE [App::DocumentObjectGroupPython] N_element015  label="N_element : 008"  # scripted group (container) (typed FeaturePython)
  n = 1
  ref = N_element
FEATURE [App::DocumentObjectGroupPython] O_element033  label="O_element : 016"  # scripted group (container) (typed FeaturePython)
  n = 1
  ref = O_element
FEATURE [App::DocumentObjectGroupPython] G4_N_N_DIMETHYL_FORMAMIDE  label="G4_N.N-DIMETHYL_FORMAMIDE"  # scripted group (container) (typed FeaturePython)
  Dunit = g/cm3
  Dvalue = 0.9487
  Group = -> [C_element036,H_element033,N_element015,O_element033]
  conduct = 2
  density = 1
  expand = 3
  formula = G4_N.N-DIMETHYL_FORMAMIDE
  name = G4_N.N-DIMETHYL_FORMAMIDE
  specific = 4
FEATURE [App::DocumentObjectGroupPython] C_element037  label="C_element : 021"  # scripted group (container) (typed FeaturePython)
  n = 2
  ref = C_element
FEATURE [App::DocumentObjectGroupPython] H_element034  label="H_element : 017"  # scripted group (container) (typed FeaturePython)
  n = 6
  ref = H_element
FEATURE [App::DocumentObjectGroupPython] O_element034  label="O_element : 017"  # scripted group (container) (typed FeaturePython)
  n = 1
  ref = O_element
FEATURE [App::DocumentObjectGroupPython] S_element009  label="S_element : 003"  # scripted group (container) (typed FeaturePython)
  n = 1
  ref = S_element
FEATURE [App::DocumentObjectGroupPython] G4_DIMETHYL_SULFOXIDE  # scripted group (container) (typed FeaturePython)
  Dunit = g/cm3
  Dvalue = 1.1014
  Group = -> [C_element037,H_element034,O_element034,S_element009]
  conduct = 2
  density = 1
  expand = 3
  formula = G4_DIMETHYL_SULFOXIDE
  name = G4_DIMETHYL_SULFOXIDE
  specific = 4
FEATURE [App::DocumentObjectGroupPython] C_element038  label="C_element : 022"  # scripted group (container) (typed FeaturePython)
  n = 2
  ref = C_element
FEATURE [App::DocumentObjectGroupPython] H_element035  label="H_element : 018"  # scripted group (container) (typed FeaturePython)
  n = 6
  ref = H_element
FEATURE [App::DocumentObjectGroupPython] G4_ETHANE  # scripted group (container) (typed FeaturePython)
  Dunit = g/cm3
  Dvalue = 0.00125324
  Group = -> [C_element038,H_element035]
  conduct = 2
  density = 1
  expand = 3
  formula = G4_ETHANE
  name = G4_ETHANE
  specific = 4
FEATURE [App::DocumentObjectGroupPython] C_element039  label="C_element : 023"  # scripted group (container) (typed FeaturePython)
  n = 2
  ref = C_element
FEATURE [App::DocumentObjectGroupPython] H_element036  label="H_element : 019"  # scripted group (container) (typed FeaturePython)
  n = 6
  ref = H_element
FEATURE [App::DocumentObjectGroupPython] O_element035  label="O_element : 018"  # scripted group (container) (typed FeaturePython)
  n = 1
  ref = O_element
FEATURE [App::DocumentObjectGroupPython] G4_ETHYL_ALCOHOL  # scripted group (container) (typed FeaturePython)
  Dunit = g/cm3
  Dvalue = 0.7893
  Group = -> [C_element039,H_element036,O_element035]
  conduct = 2
  density = 1
  expand = 3
  formula = G4_ETHYL_ALCOHOL
  name = G4_ETHYL_ALCOHOL
  specific = 4
FEATURE [App::DocumentObjectGroupPython] H_element037  label="H_element : 0.090"  # scripted group (container) (typed FeaturePython)
  n = 0.090027
FEATURE [App::DocumentObjectGroupPython] C_element040  label="C_element : 0.585"  # scripted group (container) (typed FeaturePython)
  n = 0.585182
FEATURE [App::DocumentObjectGroupPython] O_element036  label="O_element : 0.325"  # scripted group (container) (typed FeaturePython)
  n = 0.324791
FEATURE [App::DocumentObjectGroupPython] G4_ETHYL_CELLULOSE  # scripted group (container) (typed FeaturePython)
  Dunit = g/cm3
  Dvalue = 1.13
  Group = -> [H_element037,C_element040,O_element036]
  conduct = 2
  density = 1
  expand = 3
  formula = G4_ETHYL_CELLULOSE
  name = G4_ETHYL_CELLULOSE
  specific = 4
FEATURE [App::DocumentObjectGroupPython] C_element041  label="C_element : 024"  # scripted group (container) (typed FeaturePython)
  n = 2
  ref = C_element
FEATURE [App::DocumentObjectGroupPython] H_element038  label="H_element : 020"  # scripted group (container) (typed FeaturePython)
  n = 4
  ref = H_element
FEATURE [App::DocumentObjectGroupPython] G4_ETHYLENE  # scripted group (container) (typed FeaturePython)
  Dunit = g/cm3
  Dvalue = 0.00117497
  Group = -> [C_element041,H_element038]
  conduct = 2
  density = 1
  expand = 3
  formula = G4_ETHYLENE
  name = G4_ETHYLENE
  specific = 4
FEATURE [App::DocumentObjectGroupPython] H_element039  label="H_element : 0.096"  # scripted group (container) (typed FeaturePython)
  n = 0.096
FEATURE [App::DocumentObjectGroupPython] C_element042  label="C_element : 0.195"  # scripted group (container) (typed FeaturePython)
  n = 0.195
FEATURE [App::DocumentObjectGroupPython] N_element016  label="N_element : 0.057"  # scripted group (container) (typed FeaturePython)
  n = 0.057
FEATURE [App::DocumentObjectGroupPython] O_element037  label="O_element : 0.646"  # scripted group (container) (typed FeaturePython)
  n = 0.646
FEATURE [App::DocumentObjectGroupPython] Na_element006  label="Na_element : 0.017"  # scripted group (container) (typed FeaturePython)
  n = 0.001
FEATURE [App::DocumentObjectGroupPython] P_element005  label="P_element : 0.104"  # scripted group (container) (typed FeaturePython)
  n = 0.001
FEATURE [App::DocumentObjectGroupPython] S_element010  label="S_element : 0.016"  # scripted group (container) (typed FeaturePython)
  n = 0.003
FEATURE [App::DocumentObjectGroupPython] Cl_element010  label="Cl_element : 0.005"  # scripted group (container) (typed FeaturePython)
  n = 0.001
FEATURE [App::DocumentObjectGroupPython] G4_EYE_LENS_ICRP  # scripted group (container) (typed FeaturePython)
  Dunit = g/cm3
  Dvalue = 1.07
  Group = -> [H_element039,C_element042,N_element016,O_element037,Na_element006,P_element005,S_element010,Cl_element010]
  conduct = 2
  density = 1
  expand = 3
  formula = G4_EYE_LENS_ICRP
  name = G4_EYE_LENS_ICRP
  specific = 4
FEATURE [App::DocumentObjectGroupPython] Fe_element003  label="Fe_element : 2"  # scripted group (container) (typed FeaturePython)
  n = 2
  ref = Fe_element
FEATURE [App::DocumentObjectGroupPython] O_element038  label="O_element : 019"  # scripted group (container) (typed FeaturePython)
  n = 3
  ref = O_element
FEATURE [App::DocumentObjectGroupPython] G4_FERRIC_OXIDE  # scripted group (container) (typed FeaturePython)
  Dunit = g/cm3
  Dvalue = 5.2
  Group = -> [Fe_element003,O_element038]
  conduct = 2
  density = 1
  expand = 3
  formula = G4_FERRIC_OXIDE
  name = G4_FERRIC_OXIDE
  specific = 4
FEATURE [App::DocumentObjectGroupPython] Fe_element004  label="Fe_element : 1"  # scripted group (container) (typed FeaturePython)
  n = 1
  ref = Fe_element
FEATURE [App::DocumentObjectGroupPython] B_element003  label="B_element : 1"  # scripted group (container) (typed FeaturePython)
  n = 1
  ref = B_element
FEATURE [App::DocumentObjectGroupPython] G4_FERROBORIDE  # scripted group (container) (typed FeaturePython)
  Dunit = g/cm3
  Dvalue = 7.15
  Group = -> [Fe_element004,B_element003]
  conduct = 2
  density = 1
  expand = 3
  formula = G4_FERROBORIDE
  name = G4_FERROBORIDE
  specific = 4
FEATURE [App::DocumentObjectGroupPython] Fe_element005  label="Fe_element : 003"  # scripted group (container) (typed FeaturePython)
  n = 1
  ref = Fe_element
FEATURE [App::DocumentObjectGroupPython] O_element039  label="O_element : 020"  # scripted group (container) (typed FeaturePython)
  n = 1
  ref = O_element
FEATURE [App::DocumentObjectGroupPython] G4_FERROUS_OXIDE  # scripted group (container) (typed FeaturePython)
  Dunit = g/cm3
  Dvalue = 5.7
  Group = -> [Fe_element005,O_element039]
  conduct = 2
  density = 1
  expand = 3
  formula = G4_FERROUS_OXIDE
  name = G4_FERROUS_OXIDE
  specific = 4
FEATURE [App::DocumentObjectGroupPython] H_element040  label="H_element : 0.115"  # scripted group (container) (typed FeaturePython)
  n = 0.108259
FEATURE [App::DocumentObjectGroupPython] N_element017  label="N_element : 0.000"  # scripted group (container) (typed FeaturePython)
  n = 2.7e-05
FEATURE [App::DocumentObjectGroupPython] O_element040  label="O_element : 0.879"  # scripted group (container) (typed FeaturePython)
  n = 0.878636
FEATURE [App::DocumentObjectGroupPython] Na_element007  label="Na_element : 0.000"  # scripted group (container) (typed FeaturePython)
  n = 2.2e-05
FEATURE [App::DocumentObjectGroupPython] S_element011  label="S_element : 0.013"  # scripted group (container) (typed FeaturePython)
  n = 0.012968
FEATURE [App::DocumentObjectGroupPython] Cl_element011  label="Cl_element : 0.000"  # scripted group (container) (typed FeaturePython)
  n = 3.4e-05
FEATURE [App::DocumentObjectGroupPython] Fe_element006  label="Fe_element : 0.000"  # scripted group (container) (typed FeaturePython)
  n = 5.4e-05
FEATURE [App::DocumentObjectGroupPython] G4_FERROUS_SULFATE  # scripted group (container) (typed FeaturePython)
  Dunit = g/cm3
  Dvalue = 1.024
  Group = -> [H_element040,N_element017,O_element040,Na_element007,S_element011,Cl_element011,Fe_element006]
  conduct = 2
  density = 1
  expand = 3
  formula = G4_FERROUS_SULFATE
  name = G4_FERROUS_SULFATE
  specific = 4
FEATURE [App::DocumentObjectGroupPython] C_element043  label="C_element : 0.099"  # scripted group (container) (typed FeaturePython)
  n = 0.099335
FEATURE [App::DocumentObjectGroupPython] F_element007  label="F_element : 0.314"  # scripted group (container) (typed FeaturePython)
  n = 0.314247
FEATURE [App::DocumentObjectGroupPython] Cl_element012  label="Cl_element : 0.586"  # scripted group (container) (typed FeaturePython)
  n = 0.586418
FEATURE [App::DocumentObjectGroupPython] G4_FREON_12  label="G4_FREON-12"  # scripted group (container) (typed FeaturePython)
  Dunit = g/cm3
  Dvalue = 1.12
  Group = -> [C_element043,F_element007,Cl_element012]
  conduct = 2
  density = 1
  expand = 3
  formula = G4_FREON-12
  name = G4_FREON-12
  specific = 4
FEATURE [App::DocumentObjectGroupPython] C_element044  label="C_element : 0.057"  # scripted group (container) (typed FeaturePython)
  n = 0.057245
FEATURE [App::DocumentObjectGroupPython] F_element008  label="F_element : 0.181"  # scripted group (container) (typed FeaturePython)
  n = 0.181096
FEATURE [App::DocumentObjectGroupPython] Br_element001  label="Br_element : 0.762"  # scripted group (container) (typed FeaturePython)
  n = 0.761659
FEATURE [App::DocumentObjectGroupPython] G4_FREON_12B2  label="G4_FREON-12B2"  # scripted group (container) (typed FeaturePython)
  Dunit = g/cm3
  Dvalue = 1.8
  Group = -> [C_element044,F_element008,Br_element001]
  conduct = 2
  density = 1
  expand = 3
  formula = G4_FREON-12B2
  name = G4_FREON-12B2
  specific = 4
FEATURE [App::DocumentObjectGroupPython] C_element045  label="C_element : 0.115"  # scripted group (container) (typed FeaturePython)
  n = 0.114983
FEATURE [App::DocumentObjectGroupPython] F_element009  label="F_element : 0.546"  # scripted group (container) (typed FeaturePython)
  n = 0.545621
FEATURE [App::DocumentObjectGroupPython] Cl_element013  label="Cl_element : 0.339"  # scripted group (container) (typed FeaturePython)
  n = 0.339396
FEATURE [App::DocumentObjectGroupPython] G4_FREON_13  label="G4_FREON-13"  # scripted group (container) (typed FeaturePython)
  Dunit = g/cm3
  Dvalue = 0.95
  Group = -> [C_element045,F_element009,Cl_element013]
  conduct = 2
  density = 1
  expand = 3
  formula = G4_FREON-13
  name = G4_FREON-13
  specific = 4
FEATURE [App::DocumentObjectGroupPython] C_element046  label="C_element : 025"  # scripted group (container) (typed FeaturePython)
  n = 1
  ref = C_element
FEATURE [App::DocumentObjectGroupPython] F_element010  label="F_element : 3"  # scripted group (container) (typed FeaturePython)
  n = 3
  ref = F_element
FEATURE [App::DocumentObjectGroupPython] Br_element002  label="Br_element : 1"  # scripted group (container) (typed FeaturePython)
  n = 1
  ref = Br_element
FEATURE [App::DocumentObjectGroupPython] G4_FREON_13B1  label="G4_FREON-13B1"  # scripted group (container) (typed FeaturePython)
  Dunit = g/cm3
  Dvalue = 1.5
  Group = -> [C_element046,F_element010,Br_element002]
  conduct = 2
  density = 1
  expand = 3
  formula = G4_FREON-13B1
  name = G4_FREON-13B1
  specific = 4
FEATURE [App::DocumentObjectGroupPython] C_element047  label="C_element : 0.061"  # scripted group (container) (typed FeaturePython)
  n = 0.061309
FEATURE [App::DocumentObjectGroupPython] F_element011  label="F_element : 0.291"  # scripted group (container) (typed FeaturePython)
  n = 0.290924
FEATURE [App::DocumentObjectGroupPython] I_element002  label="I_element : 0.648"  # scripted group (container) (typed FeaturePython)
  n = 0.647767
FEATURE [App::DocumentObjectGroupPython] G4_FREON_13I1  label="G4_FREON-13I1"  # scripted group (container) (typed FeaturePython)
  Dunit = g/cm3
  Dvalue = 1.8
  Group = -> [C_element047,F_element011,I_element002]
  conduct = 2
  density = 1
  expand = 3
  formula = G4_FREON-13I1
  name = G4_FREON-13I1
  specific = 4
FEATURE [App::DocumentObjectGroupPython] Gd_element001  label="Gd_element : 2"  # scripted group (container) (typed FeaturePython)
  n = 2
  ref = Gd_element
FEATURE [App::DocumentObjectGroupPython] O_element041  label="O_element : 021"  # scripted group (container) (typed FeaturePython)
  n = 2
  ref = O_element
FEATURE [App::DocumentObjectGroupPython] S_element012  label="S_element : 004"  # scripted group (container) (typed FeaturePython)
  n = 1
  ref = S_element
FEATURE [App::DocumentObjectGroupPython] G4_GADOLINIUM_OXYSULFIDE  # scripted group (container) (typed FeaturePython)
  Dunit = g/cm3
  Dvalue = 7.44
  Group = -> [Gd_element001,O_element041,S_element012]
  conduct = 2
  density = 1
  expand = 3
  formula = G4_GADOLINIUM_OXYSULFIDE
  name = G4_GADOLINIUM_OXYSULFIDE
  specific = 4
FEATURE [App::DocumentObjectGroupPython] Ga_element001  label="Ga_element : 1"  # scripted group (container) (typed FeaturePython)
  n = 1
  ref = Ga_element
FEATURE [App::DocumentObjectGroupPython] As_element001  label="As_element : 1"  # scripted group (container) (typed FeaturePython)
  n = 1
  ref = As_element
FEATURE [App::DocumentObjectGroupPython] G4_GALLIUM_ARSENIDE  # scripted group (container) (typed FeaturePython)
  Dunit = g/cm3
  Dvalue = 5.31
  Group = -> [Ga_element001,As_element001]
  conduct = 2
  density = 1
  expand = 3
  formula = G4_GALLIUM_ARSENIDE
  name = G4_GALLIUM_ARSENIDE
  specific = 4
FEATURE [App::DocumentObjectGroupPython] H_element041  label="H_element : 0.081"  # scripted group (container) (typed FeaturePython)
  n = 0.08118
FEATURE [App::DocumentObjectGroupPython] C_element048  label="C_element : 0.416"  # scripted group (container) (typed FeaturePython)
  n = 0.41606
FEATURE [App::DocumentObjectGroupPython] N_element018  label="N_element : 0.111"  # scripted group (container) (typed FeaturePython)
  n = 0.11124
FEATURE [App::DocumentObjectGroupPython] O_element042  label="O_element : 0.381"  # scripted group (container) (typed FeaturePython)
  n = 0.38064
FEATURE [App::DocumentObjectGroupPython] S_element013  label="S_element : 0.011"  # scripted group (container) (typed FeaturePython)
  n = 0.01088
FEATURE [App::DocumentObjectGroupPython] G4_GEL_PHOTO_EMULSION  # scripted group (container) (typed FeaturePython)
  Dunit = g/cm3
  Dvalue = 1.2914
  Group = -> [H_element041,C_element048,N_element018,O_element042,S_element013]
  conduct = 2
  density = 1
  expand = 3
  formula = G4_GEL_PHOTO_EMULSION
  name = G4_GEL_PHOTO_EMULSION
  specific = 4
FEATURE [App::DocumentObjectGroupPython] B_element004  label="B_element : 0.040"  # scripted group (container) (typed FeaturePython)
  n = 0.0400639
FEATURE [App::DocumentObjectGroupPython] O_element043  label="O_element : 0.540"  # scripted group (container) (typed FeaturePython)
  n = 0.539561
FEATURE [App::DocumentObjectGroupPython] Na_element008  label="Na_element : 0.028"  # scripted group (container) (typed FeaturePython)
  n = 0.0281909
FEATURE [App::DocumentObjectGroupPython] Al_element003  label="Al_element : 0.012"  # scripted group (container) (typed FeaturePython)
  n = 0.011644
FEATURE [App::DocumentObjectGroupPython] Si_element003  label="Si_element : 0.377"  # scripted group (container) (typed FeaturePython)
  n = 0.377219
FEATURE [App::DocumentObjectGroupPython] K_element004  label="K_element : 0.014"  # scripted group (container) (typed FeaturePython)
  n = 0.00332099
FEATURE [App::DocumentObjectGroupPython] G4_Pyrex_Glass  # scripted group (container) (typed FeaturePython)
  Dunit = g/cm3
  Dvalue = 2.23
  Group = -> [B_element004,O_element043,Na_element008,Al_element003,Si_element003,K_element004]
  conduct = 2
  density = 1
  expand = 3
  formula = G4_Pyrex_Glass
  name = G4_Pyrex_Glass
  specific = 4
FEATURE [App::DocumentObjectGroupPython] O_element044  label="O_element : 0.156"  # scripted group (container) (typed FeaturePython)
  n = 0.156453
FEATURE [App::DocumentObjectGroupPython] Si_element004  label="Si_element : 0.081"  # scripted group (container) (typed FeaturePython)
  n = 0.080866
FEATURE [App::DocumentObjectGroupPython] Ti_element001  label="Ti_element : 0.008"  # scripted group (container) (typed FeaturePython)
  n = 0.008092
FEATURE [App::DocumentObjectGroupPython] As_element002  label="As_element : 0.003"  # scripted group (container) (typed FeaturePython)
  n = 0.002651
FEATURE [App::DocumentObjectGroupPython] Pb_element001  label="Pb_element : 0.752"  # scripted group (container) (typed FeaturePython)
  n = 0.751938
FEATURE [App::DocumentObjectGroupPython] G4_GLASS_LEAD  # scripted group (container) (typed FeaturePython)
  Dunit = g/cm3
  Dvalue = 6.22
  Group = -> [O_element044,Si_element004,Ti_element001,As_element002,Pb_element001]
  conduct = 2
  density = 1
  expand = 3
  formula = G4_GLASS_LEAD
  name = G4_GLASS_LEAD
  specific = 4
FEATURE [App::DocumentObjectGroupPython] O_element045  label="O_element : 0.460"  # scripted group (container) (typed FeaturePython)
  n = 0.4598
FEATURE [App::DocumentObjectGroupPython] Na_element009  label="Na_element : 0.096"  # scripted group (container) (typed FeaturePython)
  n = 0.0964411
FEATURE [App::DocumentObjectGroupPython] Si_element005  label="Si_element : 0.378"  # scripted group (container) (typed FeaturePython)
  n = 0.336553
FEATURE [App::DocumentObjectGroupPython] Ca_element011  label="Ca_element : 0.107"  # scripted group (container) (typed FeaturePython)
  n = 0.107205
FEATURE [App::DocumentObjectGroupPython] G4_GLASS_PLATE  # scripted group (container) (typed FeaturePython)
  Dunit = g/cm3
  Dvalue = 2.4
  Group = -> [O_element045,Na_element009,Si_element005,Ca_element011]
  conduct = 2
  density = 1
  expand = 3
  formula = G4_GLASS_PLATE
  name = G4_GLASS_PLATE
  specific = 4
FEATURE [App::DocumentObjectGroupPython] C_element049  label="C_element : 026"  # scripted group (container) (typed FeaturePython)
  n = 5
  ref = C_element
FEATURE [App::DocumentObjectGroupPython] H_element042  label="H_element : 021"  # scripted group (container) (typed FeaturePython)
  n = 10
  ref = H_element
FEATURE [App::DocumentObjectGroupPython] N_element019  label="N_element : 2"  # scripted group (container) (typed FeaturePython)
  n = 2
  ref = N_element
FEATURE [App::DocumentObjectGroupPython] O_element046  label="O_element : 022"  # scripted group (container) (typed FeaturePython)
  n = 3
  ref = O_element
FEATURE [App::DocumentObjectGroupPython] G4_GLUTAMINE  # scripted group (container) (typed FeaturePython)
  Dunit = g/cm3
  Dvalue = 1.46
  Group = -> [C_element049,H_element042,N_element019,O_element046]
  conduct = 2
  density = 1
  expand = 3
  formula = G4_GLUTAMINE
  name = G4_GLUTAMINE
  specific = 4
FEATURE [App::DocumentObjectGroupPython] C_element050  label="C_element : 027"  # scripted group (container) (typed FeaturePython)
  n = 3
  ref = C_element
FEATURE [App::DocumentObjectGroupPython] H_element043  label="H_element : 022"  # scripted group (container) (typed FeaturePython)
  n = 8
  ref = H_element
FEATURE [App::DocumentObjectGroupPython] O_element047  label="O_element : 023"  # scripted group (container) (typed FeaturePython)
  n = 3
  ref = O_element
FEATURE [App::DocumentObjectGroupPython] G4_GLYCEROL  # scripted group (container) (typed FeaturePython)
  Dunit = g/cm3
  Dvalue = 1.2613
  Group = -> [C_element050,H_element043,O_element047]
  conduct = 2
  density = 1
  expand = 3
  formula = G4_GLYCEROL
  name = G4_GLYCEROL
  specific = 4
FEATURE [App::DocumentObjectGroupPython] C_element051  label="C_element : 028"  # scripted group (container) (typed FeaturePython)
  n = 5
  ref = C_element
FEATURE [App::DocumentObjectGroupPython] H_element044  label="H_element : 023"  # scripted group (container) (typed FeaturePython)
  n = 5
  ref = H_element
FEATURE [App::DocumentObjectGroupPython] N_element020  label="N_element : 009"  # scripted group (container) (typed FeaturePython)
  n = 5
  ref = N_element
FEATURE [App::DocumentObjectGroupPython] O_element048  label="O_element : 024"  # scripted group (container) (typed FeaturePython)
  n = 1
  ref = O_element
FEATURE [App::DocumentObjectGroupPython] G4_GUANINE  # scripted group (container) (typed FeaturePython)
  Dunit = g/cm3
  Dvalue = 2.2
  Group = -> [C_element051,H_element044,N_element020,O_element048]
  conduct = 2
  density = 1
  expand = 3
  formula = G4_GUANINE
  name = G4_GUANINE
  specific = 4
FEATURE [App::DocumentObjectGroupPython] Ca_element012  label="Ca_element : 006"  # scripted group (container) (typed FeaturePython)
  n = 1
  ref = Ca_element
FEATURE [App::DocumentObjectGroupPython] S_element014  label="S_element : 005"  # scripted group (container) (typed FeaturePython)
  n = 1
  ref = S_element
FEATURE [App::DocumentObjectGroupPython] O_element049  label="O_element : 6"  # scripted group (container) (typed FeaturePython)
  n = 6
  ref = O_element
FEATURE [App::DocumentObjectGroupPython] H_element045  label="H_element : 024"  # scripted group (container) (typed FeaturePython)
  n = 4
  ref = H_element
FEATURE [App::DocumentObjectGroupPython] G4_GYPSUM  # scripted group (container) (typed FeaturePython)
  Dunit = g/cm3
  Dvalue = 2.32
  Group = -> [Ca_element012,S_element014,O_element049,H_element045]
  conduct = 2
  density = 1
  expand = 3
  formula = G4_GYPSUM
  name = G4_GYPSUM
  specific = 4
FEATURE [App::DocumentObjectGroupPython] C_element052  label="C_element : 7"  # scripted group (container) (typed FeaturePython)
  n = 7
  ref = C_element
FEATURE [App::DocumentObjectGroupPython] H_element046  label="H_element : 16"  # scripted group (container) (typed FeaturePython)
  n = 16
  ref = H_element
FEATURE [App::DocumentObjectGroupPython] G4_N_HEPTANE  label="G4_N-HEPTANE"  # scripted group (container) (typed FeaturePython)
  Dunit = g/cm3
  Dvalue = 0.68376
  Group = -> [C_element052,H_element046]
  conduct = 2
  density = 1
  expand = 3
  formula = G4_N-HEPTANE
  name = G4_N-HEPTANE
  specific = 4
FEATURE [App::DocumentObjectGroupPython] C_element053  label="C_element : 029"  # scripted group (container) (typed FeaturePython)
  n = 6
  ref = C_element
FEATURE [App::DocumentObjectGroupPython] H_element047  label="H_element : 14"  # scripted group (container) (typed FeaturePython)
  n = 14
  ref = H_element
FEATURE [App::DocumentObjectGroupPython] G4_N_HEXANE  label="G4_N-HEXANE"  # scripted group (container) (typed FeaturePython)
  Dunit = g/cm3
  Dvalue = 0.6603
  Group = -> [C_element053,H_element047]
  conduct = 2
  density = 1
  expand = 3
  formula = G4_N-HEXANE
  name = G4_N-HEXANE
  specific = 4
FEATURE [App::DocumentObjectGroupPython] C_element054  label="C_element : 22"  # scripted group (container) (typed FeaturePython)
  n = 22
  ref = C_element
FEATURE [App::DocumentObjectGroupPython] H_element048  label="H_element : 025"  # scripted group (container) (typed FeaturePython)
  n = 10
  ref = H_element
FEATURE [App::DocumentObjectGroupPython] N_element021  label="N_element : 010"  # scripted group (container) (typed FeaturePython)
  n = 2
  ref = N_element
FEATURE [App::DocumentObjectGroupPython] O_element050  label="O_element : 025"  # scripted group (container) (typed FeaturePython)
  n = 5
  ref = O_element
FEATURE [App::DocumentObjectGroupPython] G4_KAPTON  # scripted group (container) (typed FeaturePython)
  Dunit = g/cm3
  Dvalue = 1.42
  Group = -> [C_element054,H_element048,N_element021,O_element050]
  conduct = 2
  density = 1
  expand = 3
  formula = G4_KAPTON
  name = G4_KAPTON
  specific = 4
FEATURE [App::DocumentObjectGroupPython] La_element001  label="La_element : 1"  # scripted group (container) (typed FeaturePython)
  n = 1
  ref = La_element
FEATURE [App::DocumentObjectGroupPython] Br_element003  label="Br_element : 002"  # scripted group (container) (typed FeaturePython)
  n = 1
  ref = Br_element
FEATURE [App::DocumentObjectGroupPython] O_element051  label="O_element : 026"  # scripted group (container) (typed FeaturePython)
  n = 1
  ref = O_element
FEATURE [App::DocumentObjectGroupPython] G4_LANTHANUM_OXYBROMIDE  # scripted group (container) (typed FeaturePython)
  Dunit = g/cm3
  Dvalue = 6.28
  Group = -> [La_element001,Br_element003,O_element051]
  conduct = 2
  density = 1
  expand = 3
  formula = G4_LANTHANUM_OXYBROMIDE
  name = G4_LANTHANUM_OXYBROMIDE
  specific = 4
FEATURE [App::DocumentObjectGroupPython] La_element002  label="La_element : 2"  # scripted group (container) (typed FeaturePython)
  n = 2
  ref = La_element
FEATURE [App::DocumentObjectGroupPython] O_element052  label="O_element : 027"  # scripted group (container) (typed FeaturePython)
  n = 2
  ref = O_element
FEATURE [App::DocumentObjectGroupPython] S_element015  label="S_element : 006"  # scripted group (container) (typed FeaturePython)
  n = 1
  ref = S_element
FEATURE [App::DocumentObjectGroupPython] G4_LANTHANUM_OXYSULFIDE  # scripted group (container) (typed FeaturePython)
  Dunit = g/cm3
  Dvalue = 5.86
  Group = -> [La_element002,O_element052,S_element015]
  conduct = 2
  density = 1
  expand = 3
  formula = G4_LANTHANUM_OXYSULFIDE
  name = G4_LANTHANUM_OXYSULFIDE
  specific = 4
FEATURE [App::DocumentObjectGroupPython] O_element053  label="O_element : 0.072"  # scripted group (container) (typed FeaturePython)
  n = 0.071682
FEATURE [App::DocumentObjectGroupPython] Pb_element002  label="Pb_element : 0.928"  # scripted group (container) (typed FeaturePython)
  n = 0.928318
FEATURE [App::DocumentObjectGroupPython] G4_LEAD_OXIDE  # scripted group (container) (typed FeaturePython)
  Dunit = g/cm3
  Dvalue = 9.53
  Group = -> [O_element053,Pb_element002]
  conduct = 2
  density = 1
  expand = 3
  formula = G4_LEAD_OXIDE
  name = G4_LEAD_OXIDE
  specific = 4
FEATURE [App::DocumentObjectGroupPython] Li_element001  label="Li_element : 1"  # scripted group (container) (typed FeaturePython)
  n = 1
  ref = Li_element
FEATURE [App::DocumentObjectGroupPython] N_element022  label="N_element : 011"  # scripted group (container) (typed FeaturePython)
  n = 1
  ref = N_element
FEATURE [App::DocumentObjectGroupPython] H_element049  label="H_element : 026"  # scripted group (container) (typed FeaturePython)
  n = 2
  ref = H_element
FEATURE [App::DocumentObjectGroupPython] G4_LITHIUM_AMIDE  # scripted group (container) (typed FeaturePython)
  Dunit = g/cm3
  Dvalue = 1.178
  Group = -> [Li_element001,N_element022,H_element049]
  conduct = 2
  density = 1
  expand = 3
  formula = G4_LITHIUM_AMIDE
  name = G4_LITHIUM_AMIDE
  specific = 4
FEATURE [App::DocumentObjectGroupPython] Li_element002  label="Li_element : 2"  # scripted group (container) (typed FeaturePython)
  n = 2
  ref = Li_element
FEATURE [App::DocumentObjectGroupPython] C_element055  label="C_element : 030"  # scripted group (container) (typed FeaturePython)
  n = 1
  ref = C_element
FEATURE [App::DocumentObjectGroupPython] O_element054  label="O_element : 028"  # scripted group (container) (typed FeaturePython)
  n = 3
  ref = O_element
FEATURE [App::DocumentObjectGroupPython] G4_LITHIUM_CARBONATE  # scripted group (container) (typed FeaturePython)
  Dunit = g/cm3
  Dvalue = 2.11
  Group = -> [Li_element002,C_element055,O_element054]
  conduct = 2
  density = 1
  expand = 3
  formula = G4_LITHIUM_CARBONATE
  name = G4_LITHIUM_CARBONATE
  specific = 4
FEATURE [App::DocumentObjectGroupPython] Li_element003  label="Li_element : 003"  # scripted group (container) (typed FeaturePython)
  n = 1
  ref = Li_element
FEATURE [App::DocumentObjectGroupPython] F_element012  label="F_element : 004"  # scripted group (container) (typed FeaturePython)
  n = 1
  ref = F_element
FEATURE [App::DocumentObjectGroupPython] G4_LITHIUM_FLUORIDE  # scripted group (container) (typed FeaturePython)
  Dunit = g/cm3
  Dvalue = 2.635
  Group = -> [Li_element003,F_element012]
  conduct = 2
  density = 1
  expand = 3
  formula = G4_LITHIUM_FLUORIDE
  name = G4_LITHIUM_FLUORIDE
  specific = 4
FEATURE [App::DocumentObjectGroupPython] Li_element004  label="Li_element : 004"  # scripted group (container) (typed FeaturePython)
  n = 1
  ref = Li_element
FEATURE [App::DocumentObjectGroupPython] H_element050  label="H_element : 027"  # scripted group (container) (typed FeaturePython)
  n = 1
  ref = H_element
FEATURE [App::DocumentObjectGroupPython] G4_LITHIUM_HYDRIDE  # scripted group (container) (typed FeaturePython)
  Dunit = g/cm3
  Dvalue = 0.82
  Group = -> [Li_element004,H_element050]
  conduct = 2
  density = 1
  expand = 3
  formula = G4_LITHIUM_HYDRIDE
  name = G4_LITHIUM_HYDRIDE
  specific = 4
FEATURE [App::DocumentObjectGroupPython] Li_element005  label="Li_element : 005"  # scripted group (container) (typed FeaturePython)
  n = 1
  ref = Li_element
FEATURE [App::DocumentObjectGroupPython] I_element003  label="I_element : 002"  # scripted group (container) (typed FeaturePython)
  n = 1
  ref = I_element
FEATURE [App::DocumentObjectGroupPython] G4_LITHIUM_IODIDE  # scripted group (container) (typed FeaturePython)
  Dunit = g/cm3
  Dvalue = 3.494
  Group = -> [Li_element005,I_element003]
  conduct = 2
  density = 1
  expand = 3
  formula = G4_LITHIUM_IODIDE
  name = G4_LITHIUM_IODIDE
  specific = 4
FEATURE [App::DocumentObjectGroupPython] Li_element006  label="Li_element : 006"  # scripted group (container) (typed FeaturePython)
  n = 2
  ref = Li_element
FEATURE [App::DocumentObjectGroupPython] O_element055  label="O_element : 029"  # scripted group (container) (typed FeaturePython)
  n = 1
  ref = O_element
FEATURE [App::DocumentObjectGroupPython] G4_LITHIUM_OXIDE  # scripted group (container) (typed FeaturePython)
  Dunit = g/cm3
  Dvalue = 2.013
  Group = -> [Li_element006,O_element055]
  conduct = 2
  density = 1
  expand = 3
  formula = G4_LITHIUM_OXIDE
  name = G4_LITHIUM_OXIDE
  specific = 4
FEATURE [App::DocumentObjectGroupPython] Li_element007  label="Li_element : 007"  # scripted group (container) (typed FeaturePython)
  n = 2
  ref = Li_element
FEATURE [App::DocumentObjectGroupPython] B_element005  label="B_element : 005"  # scripted group (container) (typed FeaturePython)
  n = 4
  ref = B_element
FEATURE [App::DocumentObjectGroupPython] O_element056  label="O_element : 7"  # scripted group (container) (typed FeaturePython)
  n = 7
  ref = O_element
FEATURE [App::DocumentObjectGroupPython] G4_LITHIUM_TETRABORATE  # scripted group (container) (typed FeaturePython)
  Dunit = g/cm3
  Dvalue = 2.44
  Group = -> [Li_element007,B_element005,O_element056]
  conduct = 2
  density = 1
  expand = 3
  formula = G4_LITHIUM_TETRABORATE
  name = G4_LITHIUM_TETRABORATE
  specific = 4
FEATURE [App::DocumentObjectGroupPython] H_element051  label="H_element : 0.105"  # scripted group (container) (typed FeaturePython)
  n = 0.105
FEATURE [App::DocumentObjectGroupPython] C_element056  label="C_element : 0.083"  # scripted group (container) (typed FeaturePython)
  n = 0.083
FEATURE [App::DocumentObjectGroupPython] N_element023  label="N_element : 0.023"  # scripted group (container) (typed FeaturePython)
  n = 0.023
FEATURE [App::DocumentObjectGroupPython] O_element057  label="O_element : 0.779"  # scripted group (container) (typed FeaturePython)
  n = 0.779
FEATURE [App::DocumentObjectGroupPython] Na_element010  label="Na_element : 0.097"  # scripted group (container) (typed FeaturePython)
  n = 0.002
FEATURE [App::DocumentObjectGroupPython] P_element006  label="P_element : 0.105"  # scripted group (container) (typed FeaturePython)
  n = 0.001
FEATURE [App::DocumentObjectGroupPython] S_element016  label="S_element : 0.017"  # scripted group (container) (typed FeaturePython)
  n = 0.002
FEATURE [App::DocumentObjectGroupPython] Cl_element014  label="Cl_element : 0.587"  # scripted group (container) (typed FeaturePython)
  n = 0.003
FEATURE [App::DocumentObjectGroupPython] K_element005  label="K_element : 0.015"  # scripted group (container) (typed FeaturePython)
  n = 0.002
FEATURE [App::DocumentObjectGroupPython] G4_LUNG_ICRP  # scripted group (container) (typed FeaturePython)
  Dunit = g/cm3
  Dvalue = 1.04
  Group = -> [H_element051,C_element056,N_element023,O_element057,Na_element010,P_element006,S_element016,Cl_element014,K_element005]
  conduct = 2
  density = 1
  expand = 3
  formula = G4_LUNG_ICRP
  name = G4_LUNG_ICRP
  specific = 4
FEATURE [App::DocumentObjectGroupPython] H_element052  label="H_element : 0.116"  # scripted group (container) (typed FeaturePython)
  n = 0.114318
FEATURE [App::DocumentObjectGroupPython] C_element057  label="C_element : 0.656"  # scripted group (container) (typed FeaturePython)
  n = 0.655824
FEATURE [App::DocumentObjectGroupPython] O_element058  label="O_element : 0.092"  # scripted group (container) (typed FeaturePython)
  n = 0.0921831
FEATURE [App::DocumentObjectGroupPython] Mg_element004  label="Mg_element : 0.135"  # scripted group (container) (typed FeaturePython)
  n = 0.134792
FEATURE [App::DocumentObjectGroupPython] Ca_element013  label="Ca_element : 0.003"  # scripted group (container) (typed FeaturePython)
  n = 0.002883
FEATURE [App::DocumentObjectGroupPython] G4_M3_WAX  # scripted group (container) (typed FeaturePython)
  Dunit = g/cm3
  Dvalue = 1.05
  Group = -> [H_element052,C_element057,O_element058,Mg_element004,Ca_element013]
  conduct = 2
  density = 1
  expand = 3
  formula = G4_M3_WAX
  name = G4_M3_WAX
  specific = 4
FEATURE [App::DocumentObjectGroupPython] Mg_element005  label="Mg_element : 1"  # scripted group (container) (typed FeaturePython)
  n = 1
  ref = Mg_element
FEATURE [App::DocumentObjectGroupPython] C_element058  label="C_element : 031"  # scripted group (container) (typed FeaturePython)
  n = 1
  ref = C_element
FEATURE [App::DocumentObjectGroupPython] O_element059  label="O_element : 030"  # scripted group (container) (typed FeaturePython)
  n = 3
  ref = O_element
FEATURE [App::DocumentObjectGroupPython] G4_MAGNESIUM_CARBONATE  # scripted group (container) (typed FeaturePython)
  Dunit = g/cm3
  Dvalue = 2.958
  Group = -> [Mg_element005,C_element058,O_element059]
  conduct = 2
  density = 1
  expand = 3
  formula = G4_MAGNESIUM_CARBONATE
  name = G4_MAGNESIUM_CARBONATE
  specific = 4
FEATURE [App::DocumentObjectGroupPython] Mg_element006  label="Mg_element : 002"  # scripted group (container) (typed FeaturePython)
  n = 1
  ref = Mg_element
FEATURE [App::DocumentObjectGroupPython] F_element013  label="F_element : 005"  # scripted group (container) (typed FeaturePython)
  n = 2
  ref = F_element
FEATURE [App::DocumentObjectGroupPython] G4_MAGNESIUM_FLUORIDE  # scripted group (container) (typed FeaturePython)
  Dunit = g/cm3
  Dvalue = 3
  Group = -> [Mg_element006,F_element013]
  conduct = 2
  density = 1
  expand = 3
  formula = G4_MAGNESIUM_FLUORIDE
  name = G4_MAGNESIUM_FLUORIDE
  specific = 4
FEATURE [App::DocumentObjectGroupPython] Mg_element007  label="Mg_element : 003"  # scripted group (container) (typed FeaturePython)
  n = 1
  ref = Mg_element
FEATURE [App::DocumentObjectGroupPython] O_element060  label="O_element : 031"  # scripted group (container) (typed FeaturePython)
  n = 1
  ref = O_element
FEATURE [App::DocumentObjectGroupPython] G4_MAGNESIUM_OXIDE  # scripted group (container) (typed FeaturePython)
  Dunit = g/cm3
  Dvalue = 3.58
  Group = -> [Mg_element007,O_element060]
  conduct = 2
  density = 1
  expand = 3
  formula = G4_MAGNESIUM_OXIDE
  name = G4_MAGNESIUM_OXIDE
  specific = 4
FEATURE [App::DocumentObjectGroupPython] Mg_element008  label="Mg_element : 004"  # scripted group (container) (typed FeaturePython)
  n = 1
  ref = Mg_element
FEATURE [App::DocumentObjectGroupPython] B_element006  label="B_element : 006"  # scripted group (container) (typed FeaturePython)
  n = 4
  ref = B_element
FEATURE [App::DocumentObjectGroupPython] O_element061  label="O_element : 032"  # scripted group (container) (typed FeaturePython)
  n = 7
  ref = O_element
FEATURE [App::DocumentObjectGroupPython] G4_MAGNESIUM_TETRABORATE  # scripted group (container) (typed FeaturePython)
  Dunit = g/cm3
  Dvalue = 2.53
  Group = -> [Mg_element008,B_element006,O_element061]
  conduct = 2
  density = 1
  expand = 3
  formula = G4_MAGNESIUM_TETRABORATE
  name = G4_MAGNESIUM_TETRABORATE
  specific = 4
FEATURE [App::DocumentObjectGroupPython] Hg_element001  label="Hg_element : 1"  # scripted group (container) (typed FeaturePython)
  n = 1
  ref = Hg_element
FEATURE [App::DocumentObjectGroupPython] I_element004  label="I_element : 2"  # scripted group (container) (typed FeaturePython)
  n = 2
  ref = I_element
FEATURE [App::DocumentObjectGroupPython] G4_MERCURIC_IODIDE  # scripted group (container) (typed FeaturePython)
  Dunit = g/cm3
  Dvalue = 6.36
  Group = -> [Hg_element001,I_element004]
  conduct = 2
  density = 1
  expand = 3
  formula = G4_MERCURIC_IODIDE
  name = G4_MERCURIC_IODIDE
  specific = 4
FEATURE [App::DocumentObjectGroupPython] C_element059  label="C_element : 032"  # scripted group (container) (typed FeaturePython)
  n = 1
  ref = C_element
FEATURE [App::DocumentObjectGroupPython] H_element053  label="H_element : 028"  # scripted group (container) (typed FeaturePython)
  n = 4
  ref = H_element
FEATURE [App::DocumentObjectGroupPython] G4_METHANE  # scripted group (container) (typed FeaturePython)
  Dunit = g/cm3
  Dvalue = 0.000667151
  Group = -> [C_element059,H_element053]
  conduct = 2
  density = 1
  expand = 3
  formula = G4_METHANE
  name = G4_METHANE
  specific = 4
FEATURE [App::DocumentObjectGroupPython] C_element060  label="C_element : 033"  # scripted group (container) (typed FeaturePython)
  n = 1
  ref = C_element
FEATURE [App::DocumentObjectGroupPython] H_element054  label="H_element : 029"  # scripted group (container) (typed FeaturePython)
  n = 4
  ref = H_element
FEATURE [App::DocumentObjectGroupPython] O_element062  label="O_element : 033"  # scripted group (container) (typed FeaturePython)
  n = 1
  ref = O_element
FEATURE [App::DocumentObjectGroupPython] G4_METHANOL  # scripted group (container) (typed FeaturePython)
  Dunit = g/cm3
  Dvalue = 0.7914
  Group = -> [C_element060,H_element054,O_element062]
  conduct = 2
  density = 1
  expand = 3
  formula = G4_METHANOL
  name = G4_METHANOL
  specific = 4
FEATURE [App::DocumentObjectGroupPython] H_element055  label="H_element : 0.134"  # scripted group (container) (typed FeaturePython)
  n = 0.13404
FEATURE [App::DocumentObjectGroupPython] C_element061  label="C_element : 0.778"  # scripted group (container) (typed FeaturePython)
  n = 0.77796
FEATURE [App::DocumentObjectGroupPython] O_element063  label="O_element : 0.035"  # scripted group (container) (typed FeaturePython)
  n = 0.03502
FEATURE [App::DocumentObjectGroupPython] Mg_element009  label="Mg_element : 0.039"  # scripted group (container) (typed FeaturePython)
  n = 0.038594
FEATURE [App::DocumentObjectGroupPython] Ti_element002  label="Ti_element : 0.014"  # scripted group (container) (typed FeaturePython)
  n = 0.014386
FEATURE [App::DocumentObjectGroupPython] G4_MIX_D_WAX  # scripted group (container) (typed FeaturePython)
  Dunit = g/cm3
  Dvalue = 0.99
  Group = -> [H_element055,C_element061,O_element063,Mg_element009,Ti_element002]
  conduct = 2
  density = 1
  expand = 3
  formula = G4_MIX_D_WAX
  name = G4_MIX_D_WAX
  specific = 4
FEATURE [App::DocumentObjectGroupPython] H_element056  label="H_element : 0.135"  # scripted group (container) (typed FeaturePython)
  n = 0.081192
FEATURE [App::DocumentObjectGroupPython] C_element062  label="C_element : 0.583"  # scripted group (container) (typed FeaturePython)
  n = 0.583442
FEATURE [App::DocumentObjectGroupPython] N_element024  label="N_element : 0.018"  # scripted group (container) (typed FeaturePython)
  n = 0.017798
FEATURE [App::DocumentObjectGroupPython] O_element064  label="O_element : 0.186"  # scripted group (container) (typed FeaturePython)
  n = 0.186381
FEATURE [App::DocumentObjectGroupPython] Mg_element010  label="Mg_element : 0.130"  # scripted group (container) (typed FeaturePython)
  n = 0.130287
FEATURE [App::DocumentObjectGroupPython] Cl_element015  label="Cl_element : 0.588"  # scripted group (container) (typed FeaturePython)
  n = 0.0009
FEATURE [App::DocumentObjectGroupPython] G4_MS20_TISSUE  # scripted group (container) (typed FeaturePython)
  Dunit = g/cm3
  Dvalue = 1
  Group = -> [H_element056,C_element062,N_element024,O_element064,Mg_element010,Cl_element015]
  conduct = 2
  density = 1
  expand = 3
  formula = G4_MS20_TISSUE
  name = G4_MS20_TISSUE
  specific = 4
FEATURE [App::DocumentObjectGroupPython] H_element057  label="H_element : 0.136"  # scripted group (container) (typed FeaturePython)
  n = 0.102
FEATURE [App::DocumentObjectGroupPython] C_element063  label="C_element : 0.143"  # scripted group (container) (typed FeaturePython)
  n = 0.143
FEATURE [App::DocumentObjectGroupPython] N_element025  label="N_element : 0.034"  # scripted group (container) (typed FeaturePython)
  n = 0.034
FEATURE [App::DocumentObjectGroupPython] O_element065  label="O_element : 0.710"  # scripted group (container) (typed FeaturePython)
  n = 0.71
FEATURE [App::DocumentObjectGroupPython] Na_element011  label="Na_element : 0.098"  # scripted group (container) (typed FeaturePython)
  n = 0.001
FEATURE [App::DocumentObjectGroupPython] P_element007  label="P_element : 0.002"  # scripted group (container) (typed FeaturePython)
  n = 0.002
FEATURE [App::DocumentObjectGroupPython] S_element017  label="S_element : 0.018"  # scripted group (container) (typed FeaturePython)
  n = 0.003
FEATURE [App::DocumentObjectGroupPython] Cl_element016  label="Cl_element : 0.589"  # scripted group (container) (typed FeaturePython)
  n = 0.001
FEATURE [App::DocumentObjectGroupPython] K_element006  label="K_element : 0.004"  # scripted group (container) (typed FeaturePython)
  n = 0.004
FEATURE [App::DocumentObjectGroupPython] G4_MUSCLE_SKELETAL_ICRP  # scripted group (container) (typed FeaturePython)
  Dunit = g/cm3
  Dvalue = 1.05
  Group = -> [H_element057,C_element063,N_element025,O_element065,Na_element011,P_element007,S_element017,Cl_element016,K_element006]
  conduct = 2
  density = 1
  expand = 3
  formula = G4_MUSCLE_SKELETAL_ICRP
  name = G4_MUSCLE_SKELETAL_ICRP
  specific = 4
FEATURE [App::DocumentObjectGroupPython] H_element058  label="H_element : 0.137"  # scripted group (container) (typed FeaturePython)
  n = 0.102102
FEATURE [App::DocumentObjectGroupPython] C_element064  label="C_element : 0.123"  # scripted group (container) (typed FeaturePython)
  n = 0.123123
FEATURE [App::DocumentObjectGroupPython] N_element026  label="N_element : 0.756"  # scripted group (container) (typed FeaturePython)
  n = 0.035035
FEATURE [App::DocumentObjectGroupPython] O_element066  label="O_element : 0.730"  # scripted group (container) (typed FeaturePython)
  n = 0.72973
FEATURE [App::DocumentObjectGroupPython] Na_element012  label="Na_element : 0.099"  # scripted group (container) (typed FeaturePython)
  n = 0.001001
FEATURE [App::DocumentObjectGroupPython] P_element008  label="P_element : 0.106"  # scripted group (container) (typed FeaturePython)
  n = 0.002002
FEATURE [App::DocumentObjectGroupPython] S_element018  label="S_element : 0.019"  # scripted group (container) (typed FeaturePython)
  n = 0.004004
FEATURE [App::DocumentObjectGroupPython] K_element007  label="K_element : 0.016"  # scripted group (container) (typed FeaturePython)
  n = 0.003003
FEATURE [App::DocumentObjectGroupPython] G4_MUSCLE_STRIATED_ICRU  # scripted group (container) (typed FeaturePython)
  Dunit = g/cm3
  Dvalue = 1.04
  Group = -> [H_element058,C_element064,N_element026,O_element066,Na_element012,P_element008,S_element018,K_element007]
  conduct = 2
  density = 1
  expand = 3
  formula = G4_MUSCLE_STRIATED_ICRU
  name = G4_MUSCLE_STRIATED_ICRU
  specific = 4
FEATURE [App::DocumentObjectGroupPython] H_element059  label="H_element : 0.098"  # scripted group (container) (typed FeaturePython)
  n = 0.0982341
FEATURE [App::DocumentObjectGroupPython] C_element065  label="C_element : 0.156"  # scripted group (container) (typed FeaturePython)
  n = 0.156214
FEATURE [App::DocumentObjectGroupPython] N_element027  label="N_element : 0.757"  # scripted group (container) (typed FeaturePython)
  n = 0.035451
FEATURE [App::DocumentObjectGroupPython] O_element067  label="O_element : 0.880"  # scripted group (container) (typed FeaturePython)
  n = 0.710101
FEATURE [App::DocumentObjectGroupPython] G4_MUSCLE_WITH_SUCROSE  # scripted group (container) (typed FeaturePython)
  Dunit = g/cm3
  Dvalue = 1.11
  Group = -> [H_element059,C_element065,N_element027,O_element067]
  conduct = 2
  density = 1
  expand = 3
  formula = G4_MUSCLE_WITH_SUCROSE
  name = G4_MUSCLE_WITH_SUCROSE
  specific = 4
FEATURE [App::DocumentObjectGroupPython] H_element060  label="H_element : 0.138"  # scripted group (container) (typed FeaturePython)
  n = 0.101969
FEATURE [App::DocumentObjectGroupPython] C_element066  label="C_element : 0.120"  # scripted group (container) (typed FeaturePython)
  n = 0.120058
FEATURE [App::DocumentObjectGroupPython] N_element028  label="N_element : 0.758"  # scripted group (container) (typed FeaturePython)
  n = 0.035451
FEATURE [App::DocumentObjectGroupPython] O_element068  label="O_element : 0.743"  # scripted group (container) (typed FeaturePython)
  n = 0.742522
FEATURE [App::DocumentObjectGroupPython] G4_MUSCLE_WITHOUT_SUCROSE  # scripted group (container) (typed FeaturePython)
  Dunit = g/cm3
  Dvalue = 1.07
  Group = -> [H_element060,C_element066,N_element028,O_element068]
  conduct = 2
  density = 1
  expand = 3
  formula = G4_MUSCLE_WITHOUT_SUCROSE
  name = G4_MUSCLE_WITHOUT_SUCROSE
  specific = 4
FEATURE [App::DocumentObjectGroupPython] C_element067  label="C_element : 10"  # scripted group (container) (typed FeaturePython)
  n = 10
  ref = C_element
FEATURE [App::DocumentObjectGroupPython] H_element061  label="H_element : 030"  # scripted group (container) (typed FeaturePython)
  n = 8
  ref = H_element
FEATURE [App::DocumentObjectGroupPython] G4_NAPHTHALENE  # scripted group (container) (typed FeaturePython)
  Dunit = g/cm3
  Dvalue = 1.145
  Group = -> [C_element067,H_element061]
  conduct = 2
  density = 1
  expand = 3
  formula = G4_NAPHTHALENE
  name = G4_NAPHTHALENE
  specific = 4
FEATURE [App::DocumentObjectGroupPython] C_element068  label="C_element : 034"  # scripted group (container) (typed FeaturePython)
  n = 6
  ref = C_element
FEATURE [App::DocumentObjectGroupPython] H_element062  label="H_element : 031"  # scripted group (container) (typed FeaturePython)
  n = 5
  ref = H_element
FEATURE [App::DocumentObjectGroupPython] N_element029  label="N_element : 012"  # scripted group (container) (typed FeaturePython)
  n = 1
  ref = N_element
FEATURE [App::DocumentObjectGroupPython] O_element069  label="O_element : 034"  # scripted group (container) (typed FeaturePython)
  n = 2
  ref = O_element
FEATURE [App::DocumentObjectGroupPython] G4_NITROBENZENE  # scripted group (container) (typed FeaturePython)
  Dunit = g/cm3
  Dvalue = 1.19867
  Group = -> [C_element068,H_element062,N_element029,O_element069]
  conduct = 2
  density = 1
  expand = 3
  formula = G4_NITROBENZENE
  name = G4_NITROBENZENE
  specific = 4
FEATURE [App::DocumentObjectGroupPython] N_element030  label="N_element : 013"  # scripted group (container) (typed FeaturePython)
  n = 2
  ref = N_element
FEATURE [App::DocumentObjectGroupPython] O_element070  label="O_element : 035"  # scripted group (container) (typed FeaturePython)
  n = 1
  ref = O_element
FEATURE [App::DocumentObjectGroupPython] G4_NITROUS_OXIDE  # scripted group (container) (typed FeaturePython)
  Dunit = g/cm3
  Dvalue = 0.00183094
  Group = -> [N_element030,O_element070]
  conduct = 2
  density = 1
  expand = 3
  formula = G4_NITROUS_OXIDE
  name = G4_NITROUS_OXIDE
  specific = 4
FEATURE [App::DocumentObjectGroupPython] H_element063  label="H_element : 0.104"  # scripted group (container) (typed FeaturePython)
  n = 0.103509
FEATURE [App::DocumentObjectGroupPython] C_element069  label="C_element : 0.648"  # scripted group (container) (typed FeaturePython)
  n = 0.648416
FEATURE [App::DocumentObjectGroupPython] N_element031  label="N_element : 0.100"  # scripted group (container) (typed FeaturePython)
  n = 0.0995361
FEATURE [App::DocumentObjectGroupPython] O_element071  label="O_element : 0.149"  # scripted group (container) (typed FeaturePython)
  n = 0.148539
FEATURE [App::DocumentObjectGroupPython] G4_NYLON_8062  label="G4_NYLON-8062"  # scripted group (container) (typed FeaturePython)
  Dunit = g/cm3
  Dvalue = 1.08
  Group = -> [H_element063,C_element069,N_element031,O_element071]
  conduct = 2
  density = 1
  expand = 3
  formula = G4_NYLON-8062
  name = G4_NYLON-8062
  specific = 4
FEATURE [App::DocumentObjectGroupPython] C_element070  label="C_element : 035"  # scripted group (container) (typed FeaturePython)
  n = 6
  ref = C_element
FEATURE [App::DocumentObjectGroupPython] H_element064  label="H_element : 11"  # scripted group (container) (typed FeaturePython)
  n = 11
  ref = H_element
FEATURE [App::DocumentObjectGroupPython] N_element032  label="N_element : 014"  # scripted group (container) (typed FeaturePython)
  n = 1
  ref = N_element
FEATURE [App::DocumentObjectGroupPython] O_element072  label="O_element : 036"  # scripted group (container) (typed FeaturePython)
  n = 1
  ref = O_element
FEATURE [App::DocumentObjectGroupPython] G4_NYLON_6_6  label="G4_NYLON-6-6"  # scripted group (container) (typed FeaturePython)
  Dunit = g/cm3
  Dvalue = 1.14
  Group = -> [C_element070,H_element064,N_element032,O_element072]
  conduct = 2
  density = 1
  expand = 3
  formula = G4_NYLON-6-6
  name = G4_NYLON-6-6
  specific = 4
FEATURE [App::DocumentObjectGroupPython] H_element065  label="H_element : 0.139"  # scripted group (container) (typed FeaturePython)
  n = 0.107062
FEATURE [App::DocumentObjectGroupPython] C_element071  label="C_element : 0.680"  # scripted group (container) (typed FeaturePython)
  n = 0.680449
FEATURE [App::DocumentObjectGroupPython] N_element033  label="N_element : 0.099"  # scripted group (container) (typed FeaturePython)
  n = 0.099189
FEATURE [App::DocumentObjectGroupPython] O_element073  label="O_element : 0.113"  # scripted group (container) (typed FeaturePython)
  n = 0.1133
FEATURE [App::DocumentObjectGroupPython] G4_NYLON_6_10  label="G4_NYLON-6-10"  # scripted group (container) (typed FeaturePython)
  Dunit = g/cm3
  Dvalue = 1.14
  Group = -> [H_element065,C_element071,N_element033,O_element073]
  conduct = 2
  density = 1
  expand = 3
  formula = G4_NYLON-6-10
  name = G4_NYLON-6-10
  specific = 4
FEATURE [App::DocumentObjectGroupPython] H_element066  label="H_element : 0.140"  # scripted group (container) (typed FeaturePython)
  n = 0.115476
FEATURE [App::DocumentObjectGroupPython] C_element072  label="C_element : 0.721"  # scripted group (container) (typed FeaturePython)
  n = 0.720818
FEATURE [App::DocumentObjectGroupPython] N_element034  label="N_element : 0.076"  # scripted group (container) (typed FeaturePython)
  n = 0.0764169
FEATURE [App::DocumentObjectGroupPython] O_element074  label="O_element : 0.087"  # scripted group (container) (typed FeaturePython)
  n = 0.0872889
FEATURE [App::DocumentObjectGroupPython] G4_NYLON_11_RILSAN  label="G4_NYLON-11_RILSAN"  # scripted group (container) (typed FeaturePython)
  Dunit = g/cm3
  Dvalue = 1.425
  Group = -> [H_element066,C_element072,N_element034,O_element074]
  conduct = 2
  density = 1
  expand = 3
  formula = G4_NYLON-11_RILSAN
  name = G4_NYLON-11_RILSAN
  specific = 4
FEATURE [App::DocumentObjectGroupPython] C_element073  label="C_element : 8"  # scripted group (container) (typed FeaturePython)
  n = 8
  ref = C_element
FEATURE [App::DocumentObjectGroupPython] H_element067  label="H_element : 18"  # scripted group (container) (typed FeaturePython)
  n = 18
  ref = H_element
FEATURE [App::DocumentObjectGroupPython] G4_OCTANE  # scripted group (container) (typed FeaturePython)
  Dunit = g/cm3
  Dvalue = 0.7026
  Group = -> [C_element073,H_element067]
  conduct = 2
  density = 1
  expand = 3
  formula = G4_OCTANE
  name = G4_OCTANE
  specific = 4
FEATURE [App::DocumentObjectGroupPython] C_element074  label="C_element : 25"  # scripted group (container) (typed FeaturePython)
  n = 25
  ref = C_element
FEATURE [App::DocumentObjectGroupPython] H_element068  label="H_element : 52"  # scripted group (container) (typed FeaturePython)
  n = 52
  ref = H_element
FEATURE [App::DocumentObjectGroupPython] G4_PARAFFIN  # scripted group (container) (typed FeaturePython)
  Dunit = g/cm3
  Dvalue = 0.93
  Group = -> [C_element074,H_element068]
  conduct = 2
  density = 1
  expand = 3
  formula = G4_PARAFFIN
  name = G4_PARAFFIN
  specific = 4
FEATURE [App::DocumentObjectGroupPython] C_element075  label="C_element : 036"  # scripted group (container) (typed FeaturePython)
  n = 5
  ref = C_element
FEATURE [App::DocumentObjectGroupPython] H_element069  label="H_element : 032"  # scripted group (container) (typed FeaturePython)
  n = 12
  ref = H_element
FEATURE [App::DocumentObjectGroupPython] G4_N_PENTANE  label="G4_N-PENTANE"  # scripted group (container) (typed FeaturePython)
  Dunit = g/cm3
  Dvalue = 0.6262
  Group = -> [C_element075,H_element069]
  conduct = 2
  density = 1
  expand = 3
  formula = G4_N-PENTANE
  name = G4_N-PENTANE
  specific = 4
FEATURE [App::DocumentObjectGroupPython] H_element070  label="H_element : 0.014"  # scripted group (container) (typed FeaturePython)
  n = 0.0141
FEATURE [App::DocumentObjectGroupPython] C_element076  label="C_element : 0.072"  # scripted group (container) (typed FeaturePython)
  n = 0.072261
FEATURE [App::DocumentObjectGroupPython] N_element035  label="N_element : 0.019"  # scripted group (container) (typed FeaturePython)
  n = 0.01932
FEATURE [App::DocumentObjectGroupPython] O_element075  label="O_element : 0.066"  # scripted group (container) (typed FeaturePython)
  n = 0.066101
FEATURE [App::DocumentObjectGroupPython] S_element019  label="S_element : 0.020"  # scripted group (container) (typed FeaturePython)
  n = 0.00189
FEATURE [App::DocumentObjectGroupPython] Br_element004  label="Br_element : 0.349"  # scripted group (container) (typed FeaturePython)
  n = 0.349103
FEATURE [App::DocumentObjectGroupPython] Ag_element001  label="Ag_element : 0.474"  # scripted group (container) (typed FeaturePython)
  n = 0.474105
FEATURE [App::DocumentObjectGroupPython] I_element005  label="I_element : 0.003"  # scripted group (container) (typed FeaturePython)
  n = 0.00312
FEATURE [App::DocumentObjectGroupPython] G4_PHOTO_EMULSION  # scripted group (container) (typed FeaturePython)
  Dunit = g/cm3
  Dvalue = 3.815
  Group = -> [H_element070,C_element076,N_element035,O_element075,S_element019,Br_element004,Ag_element001,I_element005]
  conduct = 2
  density = 1
  expand = 3
  formula = G4_PHOTO_EMULSION
  name = G4_PHOTO_EMULSION
  specific = 4
FEATURE [App::DocumentObjectGroupPython] C_element077  label="C_element : 9"  # scripted group (container) (typed FeaturePython)
  n = 9
  ref = C_element
FEATURE [App::DocumentObjectGroupPython] H_element071  label="H_element : 033"  # scripted group (container) (typed FeaturePython)
  n = 10
  ref = H_element
FEATURE [App::DocumentObjectGroupPython] G4_PLASTIC_SC_VINYLTOLUENE  # scripted group (container) (typed FeaturePython)
  Dunit = g/cm3
  Dvalue = 1.032
  Group = -> [C_element077,H_element071]
  conduct = 2
  density = 1
  expand = 3
  formula = G4_PLASTIC_SC_VINYLTOLUENE
  name = G4_PLASTIC_SC_VINYLTOLUENE
  specific = 4
FEATURE [App::DocumentObjectGroupPython] Pu_element001  label="Pu_element : 1"  # scripted group (container) (typed FeaturePython)
  n = 1
  ref = Pu_element
FEATURE [App::DocumentObjectGroupPython] O_element076  label="O_element : 037"  # scripted group (container) (typed FeaturePython)
  n = 2
  ref = O_element
FEATURE [App::DocumentObjectGroupPython] G4_PLUTONIUM_DIOXIDE  # scripted group (container) (typed FeaturePython)
  Dunit = g/cm3
  Dvalue = 11.46
  Group = -> [Pu_element001,O_element076]
  conduct = 2
  density = 1
  expand = 3
  formula = G4_PLUTONIUM_DIOXIDE
  name = G4_PLUTONIUM_DIOXIDE
  specific = 4
FEATURE [App::DocumentObjectGroupPython] C_element078  label="C_element : 037"  # scripted group (container) (typed FeaturePython)
  n = 3
  ref = C_element
FEATURE [App::DocumentObjectGroupPython] H_element072  label="H_element : 034"  # scripted group (container) (typed FeaturePython)
  n = 3
  ref = H_element
FEATURE [App::DocumentObjectGroupPython] N_element036  label="N_element : 015"  # scripted group (container) (typed FeaturePython)
  n = 1
  ref = N_element
FEATURE [App::DocumentObjectGroupPython] G4_POLYACRYLONITRILE  # scripted group (container) (typed FeaturePython)
  Dunit = g/cm3
  Dvalue = 1.17
  Group = -> [C_element078,H_element072,N_element036]
  conduct = 2
  density = 1
  expand = 3
  formula = G4_POLYACRYLONITRILE
  name = G4_POLYACRYLONITRILE
  specific = 4
FEATURE [App::DocumentObjectGroupPython] C_element079  label="C_element : 16"  # scripted group (container) (typed FeaturePython)
  n = 16
  ref = C_element
FEATURE [App::DocumentObjectGroupPython] H_element073  label="H_element : 035"  # scripted group (container) (typed FeaturePython)
  n = 14
  ref = H_element
FEATURE [App::DocumentObjectGroupPython] O_element077  label="O_element : 038"  # scripted group (container) (typed FeaturePython)
  n = 3
  ref = O_element
FEATURE [App::DocumentObjectGroupPython] G4_POLYCARBONATE  # scripted group (container) (typed FeaturePython)
  Dunit = g/cm3
  Dvalue = 1.2
  Group = -> [C_element079,H_element073,O_element077]
  conduct = 2
  density = 1
  expand = 3
  formula = G4_POLYCARBONATE
  name = G4_POLYCARBONATE
  specific = 4
FEATURE [App::DocumentObjectGroupPython] C_element080  label="C_element : 038"  # scripted group (container) (typed FeaturePython)
  n = 8
  ref = C_element
FEATURE [App::DocumentObjectGroupPython] H_element074  label="H_element : 036"  # scripted group (container) (typed FeaturePython)
  n = 7
  ref = H_element
FEATURE [App::DocumentObjectGroupPython] Cl_element017  label="Cl_element : 007"  # scripted group (container) (typed FeaturePython)
  n = 1
  ref = Cl_element
FEATURE [App::DocumentObjectGroupPython] G4_POLYCHLOROSTYRENE  # scripted group (container) (typed FeaturePython)
  Dunit = g/cm3
  Dvalue = 1.3
  Group = -> [C_element080,H_element074,Cl_element017]
  conduct = 2
  density = 1
  expand = 3
  formula = G4_POLYCHLOROSTYRENE
  name = G4_POLYCHLOROSTYRENE
  specific = 4
FEATURE [App::DocumentObjectGroupPython] C_element081  label="C_element : 039"  # scripted group (container) (typed FeaturePython)
  n = 1
  ref = C_element
FEATURE [App::DocumentObjectGroupPython] H_element075  label="H_element : 037"  # scripted group (container) (typed FeaturePython)
  n = 2
  ref = H_element
FEATURE [App::DocumentObjectGroupPython] G4_POLYETHYLENE  # scripted group (container) (typed FeaturePython)
  Dunit = g/cm3
  Dvalue = 0.94
  Group = -> [C_element081,H_element075]
  conduct = 2
  density = 1
  expand = 3
  formula = G4_POLYETHYLENE
  name = G4_POLYETHYLENE
  specific = 4
FEATURE [App::DocumentObjectGroupPython] C_element082  label="C_element : 040"  # scripted group (container) (typed FeaturePython)
  n = 10
  ref = C_element
FEATURE [App::DocumentObjectGroupPython] H_element076  label="H_element : 038"  # scripted group (container) (typed FeaturePython)
  n = 8
  ref = H_element
FEATURE [App::DocumentObjectGroupPython] O_element078  label="O_element : 039"  # scripted group (container) (typed FeaturePython)
  n = 4
  ref = O_element
FEATURE [App::DocumentObjectGroupPython] G4_MYLAR  # scripted group (container) (typed FeaturePython)
  Dunit = g/cm3
  Dvalue = 1.4
  Group = -> [C_element082,H_element076,O_element078]
  conduct = 2
  density = 1
  expand = 3
  formula = G4_MYLAR
  name = G4_MYLAR
  specific = 4
FEATURE [App::DocumentObjectGroupPython] C_element083  label="C_element : 041"  # scripted group (container) (typed FeaturePython)
  n = 5
  ref = C_element
FEATURE [App::DocumentObjectGroupPython] H_element077  label="H_element : 039"  # scripted group (container) (typed FeaturePython)
  n = 8
  ref = H_element
FEATURE [App::DocumentObjectGroupPython] O_element079  label="O_element : 040"  # scripted group (container) (typed FeaturePython)
  n = 2
  ref = O_element
FEATURE [App::DocumentObjectGroupPython] G4_PLEXIGLASS  # scripted group (container) (typed FeaturePython)
  Dunit = g/cm3
  Dvalue = 1.19
  Group = -> [C_element083,H_element077,O_element079]
  conduct = 2
  density = 1
  expand = 3
  formula = G4_PLEXIGLASS
  name = G4_PLEXIGLASS
  specific = 4
FEATURE [App::DocumentObjectGroupPython] C_element084  label="C_element : 042"  # scripted group (container) (typed FeaturePython)
  n = 1
  ref = C_element
FEATURE [App::DocumentObjectGroupPython] H_element078  label="H_element : 040"  # scripted group (container) (typed FeaturePython)
  n = 2
  ref = H_element
FEATURE [App::DocumentObjectGroupPython] O_element080  label="O_element : 041"  # scripted group (container) (typed FeaturePython)
  n = 1
  ref = O_element
FEATURE [App::DocumentObjectGroupPython] G4_POLYOXYMETHYLENE  # scripted group (container) (typed FeaturePython)
  Dunit = g/cm3
  Dvalue = 1.425
  Group = -> [C_element084,H_element078,O_element080]
  conduct = 2
  density = 1
  expand = 3
  formula = G4_POLYOXYMETHYLENE
  name = G4_POLYOXYMETHYLENE
  specific = 4
FEATURE [App::DocumentObjectGroupPython] C_element085  label="C_element : 043"  # scripted group (container) (typed FeaturePython)
  n = 2
  ref = C_element
FEATURE [App::DocumentObjectGroupPython] H_element079  label="H_element : 041"  # scripted group (container) (typed FeaturePython)
  n = 4
  ref = H_element
FEATURE [App::DocumentObjectGroupPython] G4_POLYPROPYLENE  # scripted group (container) (typed FeaturePython)
  Dunit = g/cm3
  Dvalue = 0.9
  Group = -> [C_element085,H_element079]
  conduct = 2
  density = 1
  expand = 3
  formula = G4_POLYPROPYLENE
  name = G4_POLYPROPYLENE
  specific = 4
FEATURE [App::DocumentObjectGroupPython] C_element086  label="C_element : 044"  # scripted group (container) (typed FeaturePython)
  n = 8
  ref = C_element
FEATURE [App::DocumentObjectGroupPython] H_element080  label="H_element : 042"  # scripted group (container) (typed FeaturePython)
  n = 8
  ref = H_element
FEATURE [App::DocumentObjectGroupPython] G4_POLYSTYRENE  # scripted group (container) (typed FeaturePython)
  Dunit = g/cm3
  Dvalue = 1.06
  Group = -> [C_element086,H_element080]
  conduct = 2
  density = 1
  expand = 3
  formula = G4_POLYSTYRENE
  name = G4_POLYSTYRENE
  specific = 4
FEATURE [App::DocumentObjectGroupPython] C_element087  label="C_element : 045"  # scripted group (container) (typed FeaturePython)
  n = 2
  ref = C_element
FEATURE [App::DocumentObjectGroupPython] F_element014  label="F_element : 4"  # scripted group (container) (typed FeaturePython)
  n = 4
  ref = F_element
FEATURE [App::DocumentObjectGroupPython] G4_TEFLON  # scripted group (container) (typed FeaturePython)
  Dunit = g/cm3
  Dvalue = 2.2
  Group = -> [C_element087,F_element014]
  conduct = 2
  density = 1
  expand = 3
  formula = G4_TEFLON
  name = G4_TEFLON
  specific = 4
FEATURE [App::DocumentObjectGroupPython] C_element088  label="C_element : 046"  # scripted group (container) (typed FeaturePython)
  n = 2
  ref = C_element
FEATURE [App::DocumentObjectGroupPython] F_element015  label="F_element : 006"  # scripted group (container) (typed FeaturePython)
  n = 3
  ref = F_element
FEATURE [App::DocumentObjectGroupPython] Cl_element018  label="Cl_element : 008"  # scripted group (container) (typed FeaturePython)
  n = 1
  ref = Cl_element
FEATURE [App::DocumentObjectGroupPython] G4_POLYTRIFLUOROCHLOROETHYLENE  # scripted group (container) (typed FeaturePython)
  Dunit = g/cm3
  Dvalue = 2.1
  Group = -> [C_element088,F_element015,Cl_element018]
  conduct = 2
  density = 1
  expand = 3
  formula = G4_POLYTRIFLUOROCHLOROETHYLENE
  name = G4_POLYTRIFLUOROCHLOROETHYLENE
  specific = 4
FEATURE [App::DocumentObjectGroupPython] C_element089  label="C_element : 047"  # scripted group (container) (typed FeaturePython)
  n = 4
  ref = C_element
FEATURE [App::DocumentObjectGroupPython] H_element081  label="H_element : 043"  # scripted group (container) (typed FeaturePython)
  n = 6
  ref = H_element
FEATURE [App::DocumentObjectGroupPython] O_element081  label="O_element : 042"  # scripted group (container) (typed FeaturePython)
  n = 2
  ref = O_element
FEATURE [App::DocumentObjectGroupPython] G4_POLYVINYL_ACETATE  # scripted group (container) (typed FeaturePython)
  Dunit = g/cm3
  Dvalue = 1.19
  Group = -> [C_element089,H_element081,O_element081]
  conduct = 2
  density = 1
  expand = 3
  formula = G4_POLYVINYL_ACETATE
  name = G4_POLYVINYL_ACETATE
  specific = 4
FEATURE [App::DocumentObjectGroupPython] C_element090  label="C_element : 048"  # scripted group (container) (typed FeaturePython)
  n = 2
  ref = C_element
FEATURE [App::DocumentObjectGroupPython] H_element082  label="H_element : 044"  # scripted group (container) (typed FeaturePython)
  n = 4
  ref = H_element
FEATURE [App::DocumentObjectGroupPython] O_element082  label="O_element : 043"  # scripted group (container) (typed FeaturePython)
  n = 1
  ref = O_element
FEATURE [App::DocumentObjectGroupPython] G4_POLYVINYL_ALCOHOL  # scripted group (container) (typed FeaturePython)
  Dunit = g/cm3
  Dvalue = 1.3
  Group = -> [C_element090,H_element082,O_element082]
  conduct = 2
  density = 1
  expand = 3
  formula = G4_POLYVINYL_ALCOHOL
  name = G4_POLYVINYL_ALCOHOL
  specific = 4
FEATURE [App::DocumentObjectGroupPython] C_element091  label="C_element : 049"  # scripted group (container) (typed FeaturePython)
  n = 8
  ref = C_element
FEATURE [App::DocumentObjectGroupPython] H_element083  label="H_element : 045"  # scripted group (container) (typed FeaturePython)
  n = 14
  ref = H_element
FEATURE [App::DocumentObjectGroupPython] O_element083  label="O_element : 044"  # scripted group (container) (typed FeaturePython)
  n = 2
  ref = O_element
FEATURE [App::DocumentObjectGroupPython] G4_POLYVINYL_BUTYRAL  # scripted group (container) (typed FeaturePython)
  Dunit = g/cm3
  Dvalue = 1.12
  Group = -> [C_element091,H_element083,O_element083]
  conduct = 2
  density = 1
  expand = 3
  formula = G4_POLYVINYL_BUTYRAL
  name = G4_POLYVINYL_BUTYRAL
  specific = 4
FEATURE [App::DocumentObjectGroupPython] C_element092  label="C_element : 050"  # scripted group (container) (typed FeaturePython)
  n = 2
  ref = C_element
FEATURE [App::DocumentObjectGroupPython] H_element084  label="H_element : 046"  # scripted group (container) (typed FeaturePython)
  n = 3
  ref = H_element
FEATURE [App::DocumentObjectGroupPython] Cl_element019  label="Cl_element : 009"  # scripted group (container) (typed FeaturePython)
  n = 1
  ref = Cl_element
FEATURE [App::DocumentObjectGroupPython] G4_POLYVINYL_CHLORIDE  # scripted group (container) (typed FeaturePython)
  Dunit = g/cm3
  Dvalue = 1.3
  Group = -> [C_element092,H_element084,Cl_element019]
  conduct = 2
  density = 1
  expand = 3
  formula = G4_POLYVINYL_CHLORIDE
  name = G4_POLYVINYL_CHLORIDE
  specific = 4
FEATURE [App::DocumentObjectGroupPython] C_element093  label="C_element : 051"  # scripted group (container) (typed FeaturePython)
  n = 2
  ref = C_element
FEATURE [App::DocumentObjectGroupPython] H_element085  label="H_element : 047"  # scripted group (container) (typed FeaturePython)
  n = 2
  ref = H_element
FEATURE [App::DocumentObjectGroupPython] Cl_element020  label="Cl_element : 010"  # scripted group (container) (typed FeaturePython)
  n = 2
  ref = Cl_element
FEATURE [App::DocumentObjectGroupPython] G4_POLYVINYLIDENE_CHLORIDE  # scripted group (container) (typed FeaturePython)
  Dunit = g/cm3
  Dvalue = 1.7
  Group = -> [C_element093,H_element085,Cl_element020]
  conduct = 2
  density = 1
  expand = 3
  formula = G4_POLYVINYLIDENE_CHLORIDE
  name = G4_POLYVINYLIDENE_CHLORIDE
  specific = 4
FEATURE [App::DocumentObjectGroupPython] C_element094  label="C_element : 052"  # scripted group (container) (typed FeaturePython)
  n = 2
  ref = C_element
FEATURE [App::DocumentObjectGroupPython] H_element086  label="H_element : 048"  # scripted group (container) (typed FeaturePython)
  n = 2
  ref = H_element
FEATURE [App::DocumentObjectGroupPython] F_element016  label="F_element : 007"  # scripted group (container) (typed FeaturePython)
  n = 2
  ref = F_element
FEATURE [App::DocumentObjectGroupPython] G4_POLYVINYLIDENE_FLUORIDE  # scripted group (container) (typed FeaturePython)
  Dunit = g/cm3
  Dvalue = 1.76
  Group = -> [C_element094,H_element086,F_element016]
  conduct = 2
  density = 1
  expand = 3
  formula = G4_POLYVINYLIDENE_FLUORIDE
  name = G4_POLYVINYLIDENE_FLUORIDE
  specific = 4
FEATURE [App::DocumentObjectGroupPython] C_element095  label="C_element : 053"  # scripted group (container) (typed FeaturePython)
  n = 6
  ref = C_element
FEATURE [App::DocumentObjectGroupPython] H_element087  label="H_element : 9"  # scripted group (container) (typed FeaturePython)
  n = 9
  ref = H_element
FEATURE [App::DocumentObjectGroupPython] N_element037  label="N_element : 016"  # scripted group (container) (typed FeaturePython)
  n = 1
  ref = N_element
FEATURE [App::DocumentObjectGroupPython] O_element084  label="O_element : 045"  # scripted group (container) (typed FeaturePython)
  n = 1
  ref = O_element
FEATURE [App::DocumentObjectGroupPython] G4_POLYVINYL_PYRROLIDONE  # scripted group (container) (typed FeaturePython)
  Dunit = g/cm3
  Dvalue = 1.25
  Group = -> [C_element095,H_element087,N_element037,O_element084]
  conduct = 2
  density = 1
  expand = 3
  formula = G4_POLYVINYL_PYRROLIDONE
  name = G4_POLYVINYL_PYRROLIDONE
  specific = 4
FEATURE [App::DocumentObjectGroupPython] K_element008  label="K_element : 1"  # scripted group (container) (typed FeaturePython)
  n = 1
  ref = K_element
FEATURE [App::DocumentObjectGroupPython] I_element006  label="I_element : 003"  # scripted group (container) (typed FeaturePython)
  n = 1
  ref = I_element
FEATURE [App::DocumentObjectGroupPython] G4_POTASSIUM_IODIDE  # scripted group (container) (typed FeaturePython)
  Dunit = g/cm3
  Dvalue = 3.13
  Group = -> [K_element008,I_element006]
  conduct = 2
  density = 1
  expand = 3
  formula = G4_POTASSIUM_IODIDE
  name = G4_POTASSIUM_IODIDE
  specific = 4
FEATURE [App::DocumentObjectGroupPython] K_element009  label="K_element : 2"  # scripted group (container) (typed FeaturePython)
  n = 2
  ref = K_element
FEATURE [App::DocumentObjectGroupPython] O_element085  label="O_element : 046"  # scripted group (container) (typed FeaturePython)
  n = 1
  ref = O_element
FEATURE [App::DocumentObjectGroupPython] G4_POTASSIUM_OXIDE  # scripted group (container) (typed FeaturePython)
  Dunit = g/cm3
  Dvalue = 2.32
  Group = -> [K_element009,O_element085]
  conduct = 2
  density = 1
  expand = 3
  formula = G4_POTASSIUM_OXIDE
  name = G4_POTASSIUM_OXIDE
  specific = 4
FEATURE [App::DocumentObjectGroupPython] C_element096  label="C_element : 054"  # scripted group (container) (typed FeaturePython)
  n = 3
  ref = C_element
FEATURE [App::DocumentObjectGroupPython] H_element088  label="H_element : 049"  # scripted group (container) (typed FeaturePython)
  n = 8
  ref = H_element
FEATURE [App::DocumentObjectGroupPython] G4_PROPANE  # scripted group (container) (typed FeaturePython)
  Dunit = g/cm3
  Dvalue = 0.00187939
  Group = -> [C_element096,H_element088]
  conduct = 2
  density = 1
  expand = 3
  formula = G4_PROPANE
  name = G4_PROPANE
  specific = 4
FEATURE [App::DocumentObjectGroupPython] C_element097  label="C_element : 055"  # scripted group (container) (typed FeaturePython)
  n = 3
  ref = C_element
FEATURE [App::DocumentObjectGroupPython] H_element089  label="H_element : 050"  # scripted group (container) (typed FeaturePython)
  n = 8
  ref = H_element
FEATURE [App::DocumentObjectGroupPython] G4_lPROPANE  # scripted group (container) (typed FeaturePython)
  Dunit = g/cm3
  Dvalue = 0.43
  Group = -> [C_element097,H_element089]
  conduct = 2
  density = 1
  expand = 3
  formula = G4_lPROPANE
  name = G4_lPROPANE
  specific = 4
FEATURE [App::DocumentObjectGroupPython] C_element098  label="C_element : 056"  # scripted group (container) (typed FeaturePython)
  n = 3
  ref = C_element
FEATURE [App::DocumentObjectGroupPython] H_element090  label="H_element : 051"  # scripted group (container) (typed FeaturePython)
  n = 8
  ref = H_element
FEATURE [App::DocumentObjectGroupPython] O_element086  label="O_element : 047"  # scripted group (container) (typed FeaturePython)
  n = 1
  ref = O_element
FEATURE [App::DocumentObjectGroupPython] G4_N_PROPYL_ALCOHOL  label="G4_N-PROPYL_ALCOHOL"  # scripted group (container) (typed FeaturePython)
  Dunit = g/cm3
  Dvalue = 0.8035
  Group = -> [C_element098,H_element090,O_element086]
  conduct = 2
  density = 1
  expand = 3
  formula = G4_N-PROPYL_ALCOHOL
  name = G4_N-PROPYL_ALCOHOL
  specific = 4
FEATURE [App::DocumentObjectGroupPython] C_element099  label="C_element : 057"  # scripted group (container) (typed FeaturePython)
  n = 5
  ref = C_element
FEATURE [App::DocumentObjectGroupPython] H_element091  label="H_element : 052"  # scripted group (container) (typed FeaturePython)
  n = 5
  ref = H_element
FEATURE [App::DocumentObjectGroupPython] N_element038  label="N_element : 017"  # scripted group (container) (typed FeaturePython)
  n = 1
  ref = N_element
FEATURE [App::DocumentObjectGroupPython] G4_PYRIDINE  # scripted group (container) (typed FeaturePython)
  Dunit = g/cm3
  Dvalue = 0.9819
  Group = -> [C_element099,H_element091,N_element038]
  conduct = 2
  density = 1
  expand = 3
  formula = G4_PYRIDINE
  name = G4_PYRIDINE
  specific = 4
FEATURE [App::DocumentObjectGroupPython] H_element092  label="H_element : 0.144"  # scripted group (container) (typed FeaturePython)
  n = 0.143711
FEATURE [App::DocumentObjectGroupPython] C_element100  label="C_element : 0.856"  # scripted group (container) (typed FeaturePython)
  n = 0.856289
FEATURE [App::DocumentObjectGroupPython] G4_RUBBER_BUTYL  # scripted group (container) (typed FeaturePython)
  Dunit = g/cm3
  Dvalue = 0.92
  Group = -> [H_element092,C_element100]
  conduct = 2
  density = 1
  expand = 3
  formula = G4_RUBBER_BUTYL
  name = G4_RUBBER_BUTYL
  specific = 4
FEATURE [App::DocumentObjectGroupPython] H_element093  label="H_element : 0.118"  # scripted group (container) (typed FeaturePython)
  n = 0.118371
FEATURE [App::DocumentObjectGroupPython] C_element101  label="C_element : 0.882"  # scripted group (container) (typed FeaturePython)
  n = 0.881629
FEATURE [App::DocumentObjectGroupPython] G4_RUBBER_NATURAL  # scripted group (container) (typed FeaturePython)
  Dunit = g/cm3
  Dvalue = 0.92
  Group = -> [H_element093,C_element101]
  conduct = 2
  density = 1
  expand = 3
  formula = G4_RUBBER_NATURAL
  name = G4_RUBBER_NATURAL
  specific = 4
FEATURE [App::DocumentObjectGroupPython] H_element094  label="H_element : 0.145"  # scripted group (container) (typed FeaturePython)
  n = 0.05692
FEATURE [App::DocumentObjectGroupPython] C_element102  label="C_element : 0.543"  # scripted group (container) (typed FeaturePython)
  n = 0.542646
FEATURE [App::DocumentObjectGroupPython] Cl_element021  label="Cl_element : 0.400"  # scripted group (container) (typed FeaturePython)
  n = 0.400434
FEATURE [App::DocumentObjectGroupPython] G4_RUBBER_NEOPRENE  # scripted group (container) (typed FeaturePython)
  Dunit = g/cm3
  Dvalue = 1.23
  Group = -> [H_element094,C_element102,Cl_element021]
  conduct = 2
  density = 1
  expand = 3
  formula = G4_RUBBER_NEOPRENE
  name = G4_RUBBER_NEOPRENE
  specific = 4
FEATURE [App::DocumentObjectGroupPython] Si_element006  label="Si_element : 1"  # scripted group (container) (typed FeaturePython)
  n = 1
  ref = Si_element
FEATURE [App::DocumentObjectGroupPython] O_element087  label="O_element : 048"  # scripted group (container) (typed FeaturePython)
  n = 2
  ref = O_element
FEATURE [App::DocumentObjectGroupPython] G4_SILICON_DIOXIDE  # scripted group (container) (typed FeaturePython)
  Dunit = g/cm3
  Dvalue = 2.32
  Group = -> [Si_element006,O_element087]
  conduct = 2
  density = 1
  expand = 3
  formula = G4_SILICON_DIOXIDE
  name = G4_SILICON_DIOXIDE
  specific = 4
FEATURE [App::DocumentObjectGroupPython] Ag_element002  label="Ag_element : 1"  # scripted group (container) (typed FeaturePython)
  n = 1
  ref = Ag_element
FEATURE [App::DocumentObjectGroupPython] Br_element005  label="Br_element : 003"  # scripted group (container) (typed FeaturePython)
  n = 1
  ref = Br_element
FEATURE [App::DocumentObjectGroupPython] G4_SILVER_BROMIDE  # scripted group (container) (typed FeaturePython)
  Dunit = g/cm3
  Dvalue = 6.473
  Group = -> [Ag_element002,Br_element005]
  conduct = 2
  density = 1
  expand = 3
  formula = G4_SILVER_BROMIDE
  name = G4_SILVER_BROMIDE
  specific = 4
FEATURE [App::DocumentObjectGroupPython] Ag_element003  label="Ag_element : 002"  # scripted group (container) (typed FeaturePython)
  n = 1
  ref = Ag_element
FEATURE [App::DocumentObjectGroupPython] Cl_element022  label="Cl_element : 011"  # scripted group (container) (typed FeaturePython)
  n = 1
  ref = Cl_element
FEATURE [App::DocumentObjectGroupPython] G4_SILVER_CHLORIDE  # scripted group (container) (typed FeaturePython)
  Dunit = g/cm3
  Dvalue = 5.56
  Group = -> [Ag_element003,Cl_element022]
  conduct = 2
  density = 1
  expand = 3
  formula = G4_SILVER_CHLORIDE
  name = G4_SILVER_CHLORIDE
  specific = 4
FEATURE [App::DocumentObjectGroupPython] Br_element006  label="Br_element : 0.423"  # scripted group (container) (typed FeaturePython)
  n = 0.422895
FEATURE [App::DocumentObjectGroupPython] Ag_element004  label="Ag_element : 0.574"  # scripted group (container) (typed FeaturePython)
  n = 0.573748
FEATURE [App::DocumentObjectGroupPython] I_element007  label="I_element : 0.649"  # scripted group (container) (typed FeaturePython)
  n = 0.003357
FEATURE [App::DocumentObjectGroupPython] G4_SILVER_HALIDES  # scripted group (container) (typed FeaturePython)
  Dunit = g/cm3
  Dvalue = 6.47
  Group = -> [Br_element006,Ag_element004,I_element007]
  conduct = 2
  density = 1
  expand = 3
  formula = G4_SILVER_HALIDES
  name = G4_SILVER_HALIDES
  specific = 4
FEATURE [App::DocumentObjectGroupPython] Ag_element005  label="Ag_element : 003"  # scripted group (container) (typed FeaturePython)
  n = 1
  ref = Ag_element
FEATURE [App::DocumentObjectGroupPython] I_element008  label="I_element : 004"  # scripted group (container) (typed FeaturePython)
  n = 1
  ref = I_element
FEATURE [App::DocumentObjectGroupPython] G4_SILVER_IODIDE  # scripted group (container) (typed FeaturePython)
  Dunit = g/cm3
  Dvalue = 6.01
  Group = -> [Ag_element005,I_element008]
  conduct = 2
  density = 1
  expand = 3
  formula = G4_SILVER_IODIDE
  name = G4_SILVER_IODIDE
  specific = 4
FEATURE [App::DocumentObjectGroupPython] H_element095  label="H_element : 0.100"  # scripted group (container) (typed FeaturePython)
  n = 0.1
FEATURE [App::DocumentObjectGroupPython] C_element103  label="C_element : 0.204"  # scripted group (container) (typed FeaturePython)
  n = 0.204
FEATURE [App::DocumentObjectGroupPython] N_element039  label="N_element : 0.759"  # scripted group (container) (typed FeaturePython)
  n = 0.042
FEATURE [App::DocumentObjectGroupPython] O_element088  label="O_element : 0.645"  # scripted group (container) (typed FeaturePython)
  n = 0.645
FEATURE [App::DocumentObjectGroupPython] Na_element013  label="Na_element : 0.100"  # scripted group (container) (typed FeaturePython)
  n = 0.002
FEATURE [App::DocumentObjectGroupPython] P_element009  label="P_element : 0.107"  # scripted group (container) (typed FeaturePython)
  n = 0.001
FEATURE [App::DocumentObjectGroupPython] S_element020  label="S_element : 0.021"  # scripted group (container) (typed FeaturePython)
  n = 0.002
FEATURE [App::DocumentObjectGroupPython] Cl_element023  label="Cl_element : 0.590"  # scripted group (container) (typed FeaturePython)
  n = 0.003
FEATURE [App::DocumentObjectGroupPython] K_element010  label="K_element : 0.001"  # scripted group (container) (typed FeaturePython)
  n = 0.001
FEATURE [App::DocumentObjectGroupPython] G4_SKIN_ICRP  # scripted group (container) (typed FeaturePython)
  Dunit = g/cm3
  Dvalue = 1.09
  Group = -> [H_element095,C_element103,N_element039,O_element088,Na_element013,P_element009,S_element020,Cl_element023,K_element010]
  conduct = 2
  density = 1
  expand = 3
  formula = G4_SKIN_ICRP
  name = G4_SKIN_ICRP
  specific = 4
FEATURE [App::DocumentObjectGroupPython] Na_element014  label="Na_element : 2"  # scripted group (container) (typed FeaturePython)
  n = 2
  ref = Na_element
FEATURE [App::DocumentObjectGroupPython] C_element104  label="C_element : 058"  # scripted group (container) (typed FeaturePython)
  n = 1
  ref = C_element
FEATURE [App::DocumentObjectGroupPython] O_element089  label="O_element : 049"  # scripted group (container) (typed FeaturePython)
  n = 3
  ref = O_element
FEATURE [App::DocumentObjectGroupPython] G4_SODIUM_CARBONATE  # scripted group (container) (typed FeaturePython)
  Dunit = g/cm3
  Dvalue = 2.532
  Group = -> [Na_element014,C_element104,O_element089]
  conduct = 2
  density = 1
  expand = 3
  formula = G4_SODIUM_CARBONATE
  name = G4_SODIUM_CARBONATE
  specific = 4
FEATURE [App::DocumentObjectGroupPython] Na_element015  label="Na_element : 1"  # scripted group (container) (typed FeaturePython)
  n = 1
  ref = Na_element
FEATURE [App::DocumentObjectGroupPython] I_element009  label="I_element : 005"  # scripted group (container) (typed FeaturePython)
  n = 1
  ref = I_element
FEATURE [App::DocumentObjectGroupPython] G4_SODIUM_IODIDE  # scripted group (container) (typed FeaturePython)
  Dunit = g/cm3
  Dvalue = 3.667
  Group = -> [Na_element015,I_element009]
  conduct = 2
  density = 1
  expand = 3
  formula = G4_SODIUM_IODIDE
  name = G4_SODIUM_IODIDE
  specific = 4
FEATURE [App::DocumentObjectGroupPython] Na_element016  label="Na_element : 003"  # scripted group (container) (typed FeaturePython)
  n = 2
  ref = Na_element
FEATURE [App::DocumentObjectGroupPython] O_element090  label="O_element : 050"  # scripted group (container) (typed FeaturePython)
  n = 1
  ref = O_element
FEATURE [App::DocumentObjectGroupPython] G4_SODIUM_MONOXIDE  # scripted group (container) (typed FeaturePython)
  Dunit = g/cm3
  Dvalue = 2.27
  Group = -> [Na_element016,O_element090]
  conduct = 2
  density = 1
  expand = 3
  formula = G4_SODIUM_MONOXIDE
  name = G4_SODIUM_MONOXIDE
  specific = 4
FEATURE [App::DocumentObjectGroupPython] Na_element017  label="Na_element : 004"  # scripted group (container) (typed FeaturePython)
  n = 1
  ref = Na_element
FEATURE [App::DocumentObjectGroupPython] N_element040  label="N_element : 018"  # scripted group (container) (typed FeaturePython)
  n = 1
  ref = N_element
FEATURE [App::DocumentObjectGroupPython] O_element091  label="O_element : 051"  # scripted group (container) (typed FeaturePython)
  n = 3
  ref = O_element
FEATURE [App::DocumentObjectGroupPython] G4_SODIUM_NITRATE  # scripted group (container) (typed FeaturePython)
  Dunit = g/cm3
  Dvalue = 2.261
  Group = -> [Na_element017,N_element040,O_element091]
  conduct = 2
  density = 1
  expand = 3
  formula = G4_SODIUM_NITRATE
  name = G4_SODIUM_NITRATE
  specific = 4
FEATURE [App::DocumentObjectGroupPython] C_element105  label="C_element : 059"  # scripted group (container) (typed FeaturePython)
  n = 14
  ref = C_element
FEATURE [App::DocumentObjectGroupPython] H_element096  label="H_element : 053"  # scripted group (container) (typed FeaturePython)
  n = 12
  ref = H_element
FEATURE [App::DocumentObjectGroupPython] G4_STILBENE  # scripted group (container) (typed FeaturePython)
  Dunit = g/cm3
  Dvalue = 0.9707
  Group = -> [C_element105,H_element096]
  conduct = 2
  density = 1
  expand = 3
  formula = G4_STILBENE
  name = G4_STILBENE
  specific = 4
FEATURE [App::DocumentObjectGroupPython] C_element106  label="C_element : 12"  # scripted group (container) (typed FeaturePython)
  n = 12
  ref = C_element
FEATURE [App::DocumentObjectGroupPython] H_element097  label="H_element : 22"  # scripted group (container) (typed FeaturePython)
  n = 22
  ref = H_element
FEATURE [App::DocumentObjectGroupPython] O_element092  label="O_element : 11"  # scripted group (container) (typed FeaturePython)
  n = 11
  ref = O_element
FEATURE [App::DocumentObjectGroupPython] G4_SUCROSE  # scripted group (container) (typed FeaturePython)
  Dunit = g/cm3
  Dvalue = 1.5805
  Group = -> [C_element106,H_element097,O_element092]
  conduct = 2
  density = 1
  expand = 3
  formula = G4_SUCROSE
  name = G4_SUCROSE
  specific = 4
FEATURE [App::DocumentObjectGroupPython] C_element107  label="C_element : 18"  # scripted group (container) (typed FeaturePython)
  n = 18
  ref = C_element
FEATURE [App::DocumentObjectGroupPython] H_element098  label="H_element : 054"  # scripted group (container) (typed FeaturePython)
  n = 14
  ref = H_element
FEATURE [App::DocumentObjectGroupPython] G4_TERPHENYL  # scripted group (container) (typed FeaturePython)
  Dunit = g/cm3
  Dvalue = 1.24
  Group = -> [C_element107,H_element098]
  conduct = 2
  density = 1
  expand = 3
  formula = G4_TERPHENYL
  name = G4_TERPHENYL
  specific = 4
FEATURE [App::DocumentObjectGroupPython] H_element099  label="H_element : 0.146"  # scripted group (container) (typed FeaturePython)
  n = 0.106
FEATURE [App::DocumentObjectGroupPython] C_element108  label="C_element : 0.883"  # scripted group (container) (typed FeaturePython)
  n = 0.099
FEATURE [App::DocumentObjectGroupPython] N_element041  label="N_element : 0.020"  # scripted group (container) (typed FeaturePython)
  n = 0.02
FEATURE [App::DocumentObjectGroupPython] O_element093  label="O_element : 0.766"  # scripted group (container) (typed FeaturePython)
  n = 0.766
FEATURE [App::DocumentObjectGroupPython] Na_element018  label="Na_element : 0.101"  # scripted group (container) (typed FeaturePython)
  n = 0.002
FEATURE [App::DocumentObjectGroupPython] P_element010  label="P_element : 0.108"  # scripted group (container) (typed FeaturePython)
  n = 0.001
FEATURE [App::DocumentObjectGroupPython] S_element021  label="S_element : 0.022"  # scripted group (container) (typed FeaturePython)
  n = 0.002
FEATURE [App::DocumentObjectGroupPython] Cl_element024  label="Cl_element : 0.002"  # scripted group (container) (typed FeaturePython)
  n = 0.002
FEATURE [App::DocumentObjectGroupPython] K_element011  label="K_element : 0.017"  # scripted group (container) (typed FeaturePython)
  n = 0.002
FEATURE [App::DocumentObjectGroupPython] G4_TESTIS_ICRP  # scripted group (container) (typed FeaturePython)
  Dunit = g/cm3
  Dvalue = 1.04
  Group = -> [H_element099,C_element108,N_element041,O_element093,Na_element018,P_element010,S_element021,Cl_element024,K_element011]
  conduct = 2
  density = 1
  expand = 3
  formula = G4_TESTIS_ICRP
  name = G4_TESTIS_ICRP
  specific = 4
FEATURE [App::DocumentObjectGroupPython] C_element109  label="C_element : 060"  # scripted group (container) (typed FeaturePython)
  n = 2
  ref = C_element
FEATURE [App::DocumentObjectGroupPython] Cl_element025  label="Cl_element : 012"  # scripted group (container) (typed FeaturePython)
  n = 4
  ref = Cl_element
FEATURE [App::DocumentObjectGroupPython] G4_TETRACHLOROETHYLENE  # scripted group (container) (typed FeaturePython)
  Dunit = g/cm3
  Dvalue = 1.625
  Group = -> [C_element109,Cl_element025]
  conduct = 2
  density = 1
  expand = 3
  formula = G4_TETRACHLOROETHYLENE
  name = G4_TETRACHLOROETHYLENE
  specific = 4
FEATURE [App::DocumentObjectGroupPython] Tl_element001  label="Tl_element : 1"  # scripted group (container) (typed FeaturePython)
  n = 1
  ref = Tl_element
FEATURE [App::DocumentObjectGroupPython] Cl_element026  label="Cl_element : 013"  # scripted group (container) (typed FeaturePython)
  n = 1
  ref = Cl_element
FEATURE [App::DocumentObjectGroupPython] G4_THALLIUM_CHLORIDE  # scripted group (container) (typed FeaturePython)
  Dunit = g/cm3
  Dvalue = 7.004
  Group = -> [Tl_element001,Cl_element026]
  conduct = 2
  density = 1
  expand = 3
  formula = G4_THALLIUM_CHLORIDE
  name = G4_THALLIUM_CHLORIDE
  specific = 4
FEATURE [App::DocumentObjectGroupPython] H_element100  label="H_element : 0.147"  # scripted group (container) (typed FeaturePython)
  n = 0.105
FEATURE [App::DocumentObjectGroupPython] C_element110  label="C_element : 0.256"  # scripted group (container) (typed FeaturePython)
  n = 0.256
FEATURE [App::DocumentObjectGroupPython] N_element042  label="N_element : 0.760"  # scripted group (container) (typed FeaturePython)
  n = 0.027
FEATURE [App::DocumentObjectGroupPython] O_element094  label="O_element : 0.602"  # scripted group (container) (typed FeaturePython)
  n = 0.602
FEATURE [App::DocumentObjectGroupPython] Na_element019  label="Na_element : 0.102"  # scripted group (container) (typed FeaturePython)
  n = 0.001
FEATURE [App::DocumentObjectGroupPython] P_element011  label="P_element : 0.109"  # scripted group (container) (typed FeaturePython)
  n = 0.002
FEATURE [App::DocumentObjectGroupPython] S_element022  label="S_element : 0.023"  # scripted group (container) (typed FeaturePython)
  n = 0.003
FEATURE [App::DocumentObjectGroupPython] Cl_element027  label="Cl_element : 0.591"  # scripted group (container) (typed FeaturePython)
  n = 0.002
FEATURE [App::DocumentObjectGroupPython] K_element012  label="K_element : 0.018"  # scripted group (container) (typed FeaturePython)
  n = 0.002
FEATURE [App::DocumentObjectGroupPython] G4_TISSUE_SOFT_ICRP  # scripted group (container) (typed FeaturePython)
  Dunit = g/cm3
  Dvalue = 1.03
  Group = -> [H_element100,C_element110,N_element042,O_element094,Na_element019,P_element011,S_element022,Cl_element027,K_element012]
  conduct = 2
  density = 1
  expand = 3
  formula = G4_TISSUE_SOFT_ICRP
  name = G4_TISSUE_SOFT_ICRP
  specific = 4
FEATURE [App::DocumentObjectGroupPython] H_element101  label="H_element : 0.148"  # scripted group (container) (typed FeaturePython)
  n = 0.101
FEATURE [App::DocumentObjectGroupPython] C_element111  label="C_element : 0.111"  # scripted group (container) (typed FeaturePython)
  n = 0.111
FEATURE [App::DocumentObjectGroupPython] N_element043  label="N_element : 0.026"  # scripted group (container) (typed FeaturePython)
  n = 0.026
FEATURE [App::DocumentObjectGroupPython] O_element095  label="O_element : 0.762"  # scripted group (container) (typed FeaturePython)
  n = 0.762
FEATURE [App::DocumentObjectGroupPython] G4_TISSUE_SOFT_ICRU_4  label="G4_TISSUE_SOFT_ICRU-4"  # scripted group (container) (typed FeaturePython)
  Dunit = g/cm3
  Dvalue = 1
  Group = -> [H_element101,C_element111,N_element043,O_element095]
  conduct = 2
  density = 1
  expand = 3
  formula = G4_TISSUE_SOFT_ICRU-4
  name = G4_TISSUE_SOFT_ICRU-4
  specific = 4
FEATURE [App::DocumentObjectGroupPython] H_element102  label="H_element : 0.149"  # scripted group (container) (typed FeaturePython)
  n = 0.101869
FEATURE [App::DocumentObjectGroupPython] C_element112  label="C_element : 0.456"  # scripted group (container) (typed FeaturePython)
  n = 0.456179
FEATURE [App::DocumentObjectGroupPython] N_element044  label="N_element : 0.761"  # scripted group (container) (typed FeaturePython)
  n = 0.035172
FEATURE [App::DocumentObjectGroupPython] O_element096  label="O_element : 0.407"  # scripted group (container) (typed FeaturePython)
  n = 0.40678
FEATURE [App::DocumentObjectGroupPython] G4_TISSUE_METHANE  label="G4_TISSUE-METHANE"  # scripted group (container) (typed FeaturePython)
  Dunit = g/cm3
  Dvalue = 0.00106409
  Group = -> [H_element102,C_element112,N_element044,O_element096]
  conduct = 2
  density = 1
  expand = 3
  formula = G4_TISSUE-METHANE
  name = G4_TISSUE-METHANE
  specific = 4
FEATURE [App::DocumentObjectGroupPython] H_element103  label="H_element : 0.103"  # scripted group (container) (typed FeaturePython)
  n = 0.102672
FEATURE [App::DocumentObjectGroupPython] C_element113  label="C_element : 0.569"  # scripted group (container) (typed FeaturePython)
  n = 0.56894
FEATURE [App::DocumentObjectGroupPython] N_element045  label="N_element : 0.762"  # scripted group (container) (typed FeaturePython)
  n = 0.035022
FEATURE [App::DocumentObjectGroupPython] O_element097  label="O_element : 0.293"  # scripted group (container) (typed FeaturePython)
  n = 0.293366
FEATURE [App::DocumentObjectGroupPython] G4_TISSUE_PROPANE  label="G4_TISSUE-PROPANE"  # scripted group (container) (typed FeaturePython)
  Dunit = g/cm3
  Dvalue = 0.00182628
  Group = -> [H_element103,C_element113,N_element045,O_element097]
  conduct = 2
  density = 1
  expand = 3
  formula = G4_TISSUE-PROPANE
  name = G4_TISSUE-PROPANE
  specific = 4
FEATURE [App::DocumentObjectGroupPython] Ti_element003  label="Ti_element : 1"  # scripted group (container) (typed FeaturePython)
  n = 1
  ref = Ti_element
FEATURE [App::DocumentObjectGroupPython] O_element098  label="O_element : 052"  # scripted group (container) (typed FeaturePython)
  n = 2
  ref = O_element
FEATURE [App::DocumentObjectGroupPython] G4_TITANIUM_DIOXIDE  # scripted group (container) (typed FeaturePython)
  Dunit = g/cm3
  Dvalue = 4.26
  Group = -> [Ti_element003,O_element098]
  conduct = 2
  density = 1
  expand = 3
  formula = G4_TITANIUM_DIOXIDE
  name = G4_TITANIUM_DIOXIDE
  specific = 4
FEATURE [App::DocumentObjectGroupPython] C_element114  label="C_element : 061"  # scripted group (container) (typed FeaturePython)
  n = 7
  ref = C_element
FEATURE [App::DocumentObjectGroupPython] H_element104  label="H_element : 055"  # scripted group (container) (typed FeaturePython)
  n = 8
  ref = H_element
FEATURE [App::DocumentObjectGroupPython] G4_TOLUENE  # scripted group (container) (typed FeaturePython)
  Dunit = g/cm3
  Dvalue = 0.8669
  Group = -> [C_element114,H_element104]
  conduct = 2
  density = 1
  expand = 3
  formula = G4_TOLUENE
  name = G4_TOLUENE
  specific = 4
FEATURE [App::DocumentObjectGroupPython] C_element115  label="C_element : 062"  # scripted group (container) (typed FeaturePython)
  n = 2
  ref = C_element
FEATURE [App::DocumentObjectGroupPython] H_element105  label="H_element : 056"  # scripted group (container) (typed FeaturePython)
  n = 1
  ref = H_element
FEATURE [App::DocumentObjectGroupPython] Cl_element028  label="Cl_element : 014"  # scripted group (container) (typed FeaturePython)
  n = 3
  ref = Cl_element
FEATURE [App::DocumentObjectGroupPython] G4_TRICHLOROETHYLENE  # scripted group (container) (typed FeaturePython)
  Dunit = g/cm3
  Dvalue = 1.46
  Group = -> [C_element115,H_element105,Cl_element028]
  conduct = 2
  density = 1
  expand = 3
  formula = G4_TRICHLOROETHYLENE
  name = G4_TRICHLOROETHYLENE
  specific = 4
FEATURE [App::DocumentObjectGroupPython] C_element116  label="C_element : 063"  # scripted group (container) (typed FeaturePython)
  n = 6
  ref = C_element
FEATURE [App::DocumentObjectGroupPython] H_element106  label="H_element : 15"  # scripted group (container) (typed FeaturePython)
  n = 15
  ref = H_element
FEATURE [App::DocumentObjectGroupPython] O_element099  label="O_element : 053"  # scripted group (container) (typed FeaturePython)
  n = 4
  ref = O_element
FEATURE [App::DocumentObjectGroupPython] P_element012  label="P_element : 1"  # scripted group (container) (typed FeaturePython)
  n = 1
  ref = P_element
FEATURE [App::DocumentObjectGroupPython] G4_TRIETHYL_PHOSPHATE  # scripted group (container) (typed FeaturePython)
  Dunit = g/cm3
  Dvalue = 1.07
  Group = -> [C_element116,H_element106,O_element099,P_element012]
  conduct = 2
  density = 1
  expand = 3
  formula = G4_TRIETHYL_PHOSPHATE
  name = G4_TRIETHYL_PHOSPHATE
  specific = 4
FEATURE [App::DocumentObjectGroupPython] W_element003  label="W_element : 003"  # scripted group (container) (typed FeaturePython)
  n = 1
  ref = W_element
FEATURE [App::DocumentObjectGroupPython] F_element017  label="F_element : 6"  # scripted group (container) (typed FeaturePython)
  n = 6
  ref = F_element
FEATURE [App::DocumentObjectGroupPython] G4_TUNGSTEN_HEXAFLUORIDE  # scripted group (container) (typed FeaturePython)
  Dunit = g/cm3
  Dvalue = 2.4
  Group = -> [W_element003,F_element017]
  conduct = 2
  density = 1
  expand = 3
  formula = G4_TUNGSTEN_HEXAFLUORIDE
  name = G4_TUNGSTEN_HEXAFLUORIDE
  specific = 4
FEATURE [App::DocumentObjectGroupPython] U_element001  label="U_element : 1"  # scripted group (container) (typed FeaturePython)
  n = 1
  ref = U_element
FEATURE [App::DocumentObjectGroupPython] C_element117  label="C_element : 064"  # scripted group (container) (typed FeaturePython)
  n = 2
  ref = C_element
FEATURE [App::DocumentObjectGroupPython] G4_URANIUM_DICARBIDE  # scripted group (container) (typed FeaturePython)
  Dunit = g/cm3
  Dvalue = 11.28
  Group = -> [U_element001,C_element117]
  conduct = 2
  density = 1
  expand = 3
  formula = G4_URANIUM_DICARBIDE
  name = G4_URANIUM_DICARBIDE
  specific = 4
FEATURE [App::DocumentObjectGroupPython] U_element002  label="U_element : 002"  # scripted group (container) (typed FeaturePython)
  n = 1
  ref = U_element
FEATURE [App::DocumentObjectGroupPython] C_element118  label="C_element : 065"  # scripted group (container) (typed FeaturePython)
  n = 1
  ref = C_element
FEATURE [App::DocumentObjectGroupPython] G4_URANIUM_MONOCARBIDE  # scripted group (container) (typed FeaturePython)
  Dunit = g/cm3
  Dvalue = 13.63
  Group = -> [U_element002,C_element118]
  conduct = 2
  density = 1
  expand = 3
  formula = G4_URANIUM_MONOCARBIDE
  name = G4_URANIUM_MONOCARBIDE
  specific = 4
FEATURE [App::DocumentObjectGroupPython] U_element003  label="U_element : 003"  # scripted group (container) (typed FeaturePython)
  n = 1
  ref = U_element
FEATURE [App::DocumentObjectGroupPython] O_element100  label="O_element : 054"  # scripted group (container) (typed FeaturePython)
  n = 2
  ref = O_element
FEATURE [App::DocumentObjectGroupPython] G4_URANIUM_OXIDE  # scripted group (container) (typed FeaturePython)
  Dunit = g/cm3
  Dvalue = 10.96
  Group = -> [U_element003,O_element100]
  conduct = 2
  density = 1
  expand = 3
  formula = G4_URANIUM_OXIDE
  name = G4_URANIUM_OXIDE
  specific = 4
FEATURE [App::DocumentObjectGroupPython] C_element119  label="C_element : 066"  # scripted group (container) (typed FeaturePython)
  n = 1
  ref = C_element
FEATURE [App::DocumentObjectGroupPython] H_element107  label="H_element : 057"  # scripted group (container) (typed FeaturePython)
  n = 4
  ref = H_element
FEATURE [App::DocumentObjectGroupPython] N_element046  label="N_element : 019"  # scripted group (container) (typed FeaturePython)
  n = 2
  ref = N_element
FEATURE [App::DocumentObjectGroupPython] O_element101  label="O_element : 055"  # scripted group (container) (typed FeaturePython)
  n = 1
  ref = O_element
FEATURE [App::DocumentObjectGroupPython] G4_UREA  # scripted group (container) (typed FeaturePython)
  Dunit = g/cm3
  Dvalue = 1.323
  Group = -> [C_element119,H_element107,N_element046,O_element101]
  conduct = 2
  density = 1
  expand = 3
  formula = G4_UREA
  name = G4_UREA
  specific = 4
FEATURE [App::DocumentObjectGroupPython] C_element120  label="C_element : 067"  # scripted group (container) (typed FeaturePython)
  n = 5
  ref = C_element
FEATURE [App::DocumentObjectGroupPython] H_element108  label="H_element : 058"  # scripted group (container) (typed FeaturePython)
  n = 11
  ref = H_element
FEATURE [App::DocumentObjectGroupPython] N_element047  label="N_element : 020"  # scripted group (container) (typed FeaturePython)
  n = 1
  ref = N_element
FEATURE [App::DocumentObjectGroupPython] O_element102  label="O_element : 056"  # scripted group (container) (typed FeaturePython)
  n = 2
  ref = O_element
FEATURE [App::DocumentObjectGroupPython] G4_VALINE  # scripted group (container) (typed FeaturePython)
  Dunit = g/cm3
  Dvalue = 1.23
  Group = -> [C_element120,H_element108,N_element047,O_element102]
  conduct = 2
  density = 1
  expand = 3
  formula = G4_VALINE
  name = G4_VALINE
  specific = 4
FEATURE [App::DocumentObjectGroupPython] H_element109  label="H_element : 0.009"  # scripted group (container) (typed FeaturePython)
  n = 0.009417
FEATURE [App::DocumentObjectGroupPython] C_element121  label="C_element : 0.281"  # scripted group (container) (typed FeaturePython)
  n = 0.280555
FEATURE [App::DocumentObjectGroupPython] F_element018  label="F_element : 0.710"  # scripted group (container) (typed FeaturePython)
  n = 0.710028
FEATURE [App::DocumentObjectGroupPython] G4_VITON  # scripted group (container) (typed FeaturePython)
  Dunit = g/cm3
  Dvalue = 1.8
  Group = -> [H_element109,C_element121,F_element018]
  conduct = 2
  density = 1
  expand = 3
  formula = G4_VITON
  name = G4_VITON
  specific = 4
FEATURE [App::DocumentObjectGroupPython] H_element110  label="H_element : 059"  # scripted group (container) (typed FeaturePython)
  n = 2
  ref = H_element
FEATURE [App::DocumentObjectGroupPython] O_element103  label="O_element : 057"  # scripted group (container) (typed FeaturePython)
  n = 1
  ref = O_element
FEATURE [App::DocumentObjectGroupPython] G4_WATER  # scripted group (container) (typed FeaturePython)
  Dunit = g/cm3
  Dvalue = 1
  Group = -> [H_element110,O_element103]
  conduct = 2
  density = 1
  expand = 3
  formula = G4_WATER
  name = G4_WATER
  specific = 4
FEATURE [App::DocumentObjectGroupPython] H_element111  label="H_element : 060"  # scripted group (container) (typed FeaturePython)
  n = 2
  ref = H_element
FEATURE [App::DocumentObjectGroupPython] O_element104  label="O_element : 058"  # scripted group (container) (typed FeaturePython)
  n = 1
  ref = O_element
FEATURE [App::DocumentObjectGroupPython] G4_WATER_VAPOR  # scripted group (container) (typed FeaturePython)
  Dunit = g/cm3
  Dvalue = 0.000756182
  Group = -> [H_element111,O_element104]
  conduct = 2
  density = 1
  expand = 3
  formula = G4_WATER_VAPOR
  name = G4_WATER_VAPOR
  specific = 4
FEATURE [App::DocumentObjectGroupPython] C_element122  label="C_element : 068"  # scripted group (container) (typed FeaturePython)
  n = 8
  ref = C_element
FEATURE [App::DocumentObjectGroupPython] H_element112  label="H_element : 061"  # scripted group (container) (typed FeaturePython)
  n = 10
  ref = H_element
FEATURE [App::DocumentObjectGroupPython] G4_XYLENE  # scripted group (container) (typed FeaturePython)
  Dunit = g/cm3
  Dvalue = 0.87
  Group = -> [C_element122,H_element112]
  conduct = 2
  density = 1
  expand = 3
  formula = G4_XYLENE
  name = G4_XYLENE
  specific = 4
FEATURE [App::DocumentObjectGroupPython] C_element123  label="C_element : 069"  # scripted group (container) (typed FeaturePython)
  n = 1
  ref = C_element
FEATURE [App::DocumentObjectGroupPython] G4_GRAPHITE  # scripted group (container) (typed FeaturePython)
  Dunit = g/cm3
  Dvalue = 2.21
  Group = -> [C_element123]
  conduct = 2
  density = 1
  expand = 3
  formula = G4_GRAPHITE
  name = G4_GRAPHITE
  specific = 4
FEATURE [App::DocumentObjectGroupPython] NIST  # scripted group (container) (typed FeaturePython)
  Group = -> [G4_A_150_TISSUE,G4_ACETONE,G4_ACETYLENE,G4_ADENINE,G4_ADIPOSE_TISSUE_ICRP,G4_AIR,G4_ALANINE,G4_ALUMINUM_OXIDE,G4_AMBER,G4_AMMONIA,G4_ANILINE,G4_ANTHRACENE,G4_B_100_BONE,G4_BAKELITE,G4_BARIUM_FLUORIDE,G4_BARIUM_SULFATE,G4_BENZENE,G4_BERYLLIUM_OXIDE,G4_BGO,G4_BLOOD_ICRP,G4_BONE_COMPACT_ICRU,G4_BONE_CORTICAL_ICRP,G4_BORON_CARBIDE,G4_BORON_OXIDE,G4_BRAIN_ICRP,G4_BUTANE,G4_N_BUTYL_ALCOHOL,G4_C_552,+152 more]
FEATURE [App::DocumentObjectGroupPython] H_element113  label="H_element : 062"  # scripted group (container) (typed FeaturePython)
  n = 1
  ref = H_element
FEATURE [App::DocumentObjectGroupPython] G4_H  # scripted group (container) (typed FeaturePython)
  Dunit = g/cm3
  Dvalue = 8.3748e-05
  Group = -> [H_element113]
  conduct = 2
  density = 1
  expand = 3
  formula = H
  name = G4_H
  specific = 4
FEATURE [App::DocumentObjectGroupPython] He_element001  label="He_element : 1"  # scripted group (container) (typed FeaturePython)
  n = 1
  ref = He_element
FEATURE [App::DocumentObjectGroupPython] G4_He  # scripted group (container) (typed FeaturePython)
  Dunit = g/cm3
  Dvalue = 0.000166322
  Group = -> [He_element001]
  conduct = 2
  density = 1
  expand = 3
  formula = He
  name = G4_He
  specific = 4
FEATURE [App::DocumentObjectGroupPython] Li_element008  label="Li_element : 008"  # scripted group (container) (typed FeaturePython)
  n = 1
  ref = Li_element
FEATURE [App::DocumentObjectGroupPython] G4_Li  # scripted group (container) (typed FeaturePython)
  Dunit = g/cm3
  Dvalue = 0.534
  Group = -> [Li_element008]
  conduct = 2
  density = 1
  expand = 3
  formula = Li
  name = G4_Li
  specific = 4
FEATURE [App::DocumentObjectGroupPython] Be_element002  label="Be_element : 002"  # scripted group (container) (typed FeaturePython)
  n = 1
  ref = Be_element
FEATURE [App::DocumentObjectGroupPython] G4_Be  # scripted group (container) (typed FeaturePython)
  Dunit = g/cm3
  Dvalue = 1.848
  Group = -> [Be_element002]
  conduct = 2
  density = 1
  expand = 3
  formula = Be
  name = G4_Be
  specific = 4
FEATURE [App::DocumentObjectGroupPython] B_element007  label="B_element : 007"  # scripted group (container) (typed FeaturePython)
  n = 1
  ref = B_element
FEATURE [App::DocumentObjectGroupPython] G4_B  # scripted group (container) (typed FeaturePython)
  Dunit = g/cm3
  Dvalue = 2.37
  Group = -> [B_element007]
  conduct = 2
  density = 1
  expand = 3
  formula = B
  name = G4_B
  specific = 4
FEATURE [App::DocumentObjectGroupPython] C_element124  label="C_element : 070"  # scripted group (container) (typed FeaturePython)
  n = 1
  ref = C_element
FEATURE [App::DocumentObjectGroupPython] G4_C  # scripted group (container) (typed FeaturePython)
  Dunit = g/cm3
  Dvalue = 2
  Group = -> [C_element124]
  conduct = 2
  density = 1
  expand = 3
  formula = C
  name = G4_C
  specific = 4
FEATURE [App::DocumentObjectGroupPython] N_element048  label="N_element : 021"  # scripted group (container) (typed FeaturePython)
  n = 1
  ref = N_element
FEATURE [App::DocumentObjectGroupPython] G4_N  # scripted group (container) (typed FeaturePython)
  Dunit = g/cm3
  Dvalue = 0.0011652
  Group = -> [N_element048]
  conduct = 2
  density = 1
  expand = 3
  formula = N
  name = G4_N
  specific = 4
FEATURE [App::DocumentObjectGroupPython] O_element105  label="O_element : 059"  # scripted group (container) (typed FeaturePython)
  n = 1
  ref = O_element
FEATURE [App::DocumentObjectGroupPython] G4_O  # scripted group (container) (typed FeaturePython)
  Dunit = g/cm3
  Dvalue = 0.00133151
  Group = -> [O_element105]
  conduct = 2
  density = 1
  expand = 3
  formula = O
  name = G4_O
  specific = 4
FEATURE [App::DocumentObjectGroupPython] F_element019  label="F_element : 008"  # scripted group (container) (typed FeaturePython)
  n = 1
  ref = F_element
FEATURE [App::DocumentObjectGroupPython] G4_F  # scripted group (container) (typed FeaturePython)
  Dunit = g/cm3
  Dvalue = 0.00158029
  Group = -> [F_element019]
  conduct = 2
  density = 1
  expand = 3
  formula = F
  name = G4_F
  specific = 4
FEATURE [App::DocumentObjectGroupPython] Ne_element001  label="Ne_element : 1"  # scripted group (container) (typed FeaturePython)
  n = 1
  ref = Ne_element
FEATURE [App::DocumentObjectGroupPython] G4_Ne  # scripted group (container) (typed FeaturePython)
  Dunit = g/cm3
  Dvalue = 0.000838505
  Group = -> [Ne_element001]
  conduct = 2
  density = 1
  expand = 3
  formula = Ne
  name = G4_Ne
  specific = 4
FEATURE [App::DocumentObjectGroupPython] Na_element020  label="Na_element : 005"  # scripted group (container) (typed FeaturePython)
  n = 1
  ref = Na_element
FEATURE [App::DocumentObjectGroupPython] G4_Na  # scripted group (container) (typed FeaturePython)
  Dunit = g/cm3
  Dvalue = 0.971
  Group = -> [Na_element020]
  conduct = 2
  density = 1
  expand = 3
  formula = Na
  name = G4_Na
  specific = 4
FEATURE [App::DocumentObjectGroupPython] Mg_element011  label="Mg_element : 005"  # scripted group (container) (typed FeaturePython)
  n = 1
  ref = Mg_element
FEATURE [App::DocumentObjectGroupPython] G4_Mg  # scripted group (container) (typed FeaturePython)
  Dunit = g/cm3
  Dvalue = 1.74
  Group = -> [Mg_element011]
  conduct = 2
  density = 1
  expand = 3
  formula = Mg
  name = G4_Mg
  specific = 4
FEATURE [App::DocumentObjectGroupPython] Al_element004  label="Al_element : 1"  # scripted group (container) (typed FeaturePython)
  n = 1
  ref = Al_element
FEATURE [App::DocumentObjectGroupPython] G4_Al  # scripted group (container) (typed FeaturePython)
  Dunit = g/cm3
  Dvalue = 2.699
  Group = -> [Al_element004]
  conduct = 2
  density = 1
  expand = 3
  formula = Al
  name = G4_Al
  specific = 4
FEATURE [App::DocumentObjectGroupPython] Si_element007  label="Si_element : 002"  # scripted group (container) (typed FeaturePython)
  n = 1
  ref = Si_element
FEATURE [App::DocumentObjectGroupPython] G4_Si  # scripted group (container) (typed FeaturePython)
  Dunit = g/cm3
  Dvalue = 2.33
  Group = -> [Si_element007]
  conduct = 2
  density = 1
  expand = 3
  formula = Si
  name = G4_Si
  specific = 4
FEATURE [App::DocumentObjectGroupPython] P_element013  label="P_element : 002"  # scripted group (container) (typed FeaturePython)
  n = 1
  ref = P_element
FEATURE [App::DocumentObjectGroupPython] G4_P  # scripted group (container) (typed FeaturePython)
  Dunit = g/cm3
  Dvalue = 2.2
  Group = -> [P_element013]
  conduct = 2
  density = 1
  expand = 3
  formula = P
  name = G4_P
  specific = 4
FEATURE [App::DocumentObjectGroupPython] S_element023  label="S_element : 007"  # scripted group (container) (typed FeaturePython)
  n = 1
  ref = S_element
FEATURE [App::DocumentObjectGroupPython] G4_S  # scripted group (container) (typed FeaturePython)
  Dunit = g/cm3
  Dvalue = 2
  Group = -> [S_element023]
  conduct = 2
  density = 1
  expand = 3
  formula = S
  name = G4_S
  specific = 4
FEATURE [App::DocumentObjectGroupPython] Cl_element029  label="Cl_element : 015"  # scripted group (container) (typed FeaturePython)
  n = 1
  ref = Cl_element
FEATURE [App::DocumentObjectGroupPython] G4_Cl  # scripted group (container) (typed FeaturePython)
  Dunit = g/cm3
  Dvalue = 0.00299473
  Group = -> [Cl_element029]
  conduct = 2
  density = 1
  expand = 3
  formula = Cl
  name = G4_Cl
  specific = 4
FEATURE [App::DocumentObjectGroupPython] Ar_element002  label="Ar_element : 1"  # scripted group (container) (typed FeaturePython)
  n = 1
  ref = Ar_element
FEATURE [App::DocumentObjectGroupPython] G4_Ar  # scripted group (container) (typed FeaturePython)
  Dunit = g/cm3
  Dvalue = 0.00166201
  Group = -> [Ar_element002]
  conduct = 2
  density = 1
  expand = 3
  formula = Ar
  name = G4_Ar
  specific = 4
FEATURE [App::DocumentObjectGroupPython] K_element013  label="K_element : 003"  # scripted group (container) (typed FeaturePython)
  n = 1
  ref = K_element
FEATURE [App::DocumentObjectGroupPython] G4_K  # scripted group (container) (typed FeaturePython)
  Dunit = g/cm3
  Dvalue = 0.862
  Group = -> [K_element013]
  conduct = 2
  density = 1
  expand = 3
  formula = K
  name = G4_K
  specific = 4
FEATURE [App::DocumentObjectGroupPython] Ca_element014  label="Ca_element : 007"  # scripted group (container) (typed FeaturePython)
  n = 1
  ref = Ca_element
FEATURE [App::DocumentObjectGroupPython] G4_Ca  # scripted group (container) (typed FeaturePython)
  Dunit = g/cm3
  Dvalue = 1.55
  Group = -> [Ca_element014]
  conduct = 2
  density = 1
  expand = 3
  formula = Ca
  name = G4_Ca
  specific = 4
FEATURE [App::DocumentObjectGroupPython] Sc_element001  label="Sc_element : 1"  # scripted group (container) (typed FeaturePython)
  n = 1
  ref = Sc_element
FEATURE [App::DocumentObjectGroupPython] G4_Sc  # scripted group (container) (typed FeaturePython)
  Dunit = g/cm3
  Dvalue = 2.989
  Group = -> [Sc_element001]
  conduct = 2
  density = 1
  expand = 3
  formula = Sc
  name = G4_Sc
  specific = 4
FEATURE [App::DocumentObjectGroupPython] Ti_element004  label="Ti_element : 002"  # scripted group (container) (typed FeaturePython)
  n = 1
  ref = Ti_element
FEATURE [App::DocumentObjectGroupPython] G4_Ti  # scripted group (container) (typed FeaturePython)
  Dunit = g/cm3
  Dvalue = 4.54
  Group = -> [Ti_element004]
  conduct = 2
  density = 1
  expand = 3
  formula = Ti
  name = G4_Ti
  specific = 4
FEATURE [App::DocumentObjectGroupPython] V_element001  label="V_element : 1"  # scripted group (container) (typed FeaturePython)
  n = 1
  ref = V_element
FEATURE [App::DocumentObjectGroupPython] G4_V  # scripted group (container) (typed FeaturePython)
  Dunit = g/cm3
  Dvalue = 6.11
  Group = -> [V_element001]
  conduct = 2
  density = 1
  expand = 3
  formula = V
  name = G4_V
  specific = 4
FEATURE [App::DocumentObjectGroupPython] Cr_element001  label="Cr_element : 1"  # scripted group (container) (typed FeaturePython)
  n = 1
  ref = Cr_element
FEATURE [App::DocumentObjectGroupPython] G4_Cr  # scripted group (container) (typed FeaturePython)
  Dunit = g/cm3
  Dvalue = 7.18
  Group = -> [Cr_element001]
  conduct = 2
  density = 1
  expand = 3
  formula = Cr
  name = G4_Cr
  specific = 4
FEATURE [App::DocumentObjectGroupPython] Mn_element001  label="Mn_element : 1"  # scripted group (container) (typed FeaturePython)
  n = 1
  ref = Mn_element
FEATURE [App::DocumentObjectGroupPython] G4_Mn  # scripted group (container) (typed FeaturePython)
  Dunit = g/cm3
  Dvalue = 7.44
  Group = -> [Mn_element001]
  conduct = 2
  density = 1
  expand = 3
  formula = Mn
  name = G4_Mn
  specific = 4
FEATURE [App::DocumentObjectGroupPython] Fe_element007  label="Fe_element : 004"  # scripted group (container) (typed FeaturePython)
  n = 1
  ref = Fe_element
FEATURE [App::DocumentObjectGroupPython] G4_Fe  # scripted group (container) (typed FeaturePython)
  Dunit = g/cm3
  Dvalue = 7.874
  Group = -> [Fe_element007]
  conduct = 2
  density = 1
  expand = 3
  formula = Fe
  name = G4_Fe
  specific = 4
FEATURE [App::DocumentObjectGroupPython] Co_element001  label="Co_element : 1"  # scripted group (container) (typed FeaturePython)
  n = 1
  ref = Co_element
FEATURE [App::DocumentObjectGroupPython] G4_Co  # scripted group (container) (typed FeaturePython)
  Dunit = g/cm3
  Dvalue = 8.9
  Group = -> [Co_element001]
  conduct = 2
  density = 1
  expand = 3
  formula = Co
  name = G4_Co
  specific = 4
FEATURE [App::DocumentObjectGroupPython] Ni_element001  label="Ni_element : 1"  # scripted group (container) (typed FeaturePython)
  n = 1
  ref = Ni_element
FEATURE [App::DocumentObjectGroupPython] G4_Ni  # scripted group (container) (typed FeaturePython)
  Dunit = g/cm3
  Dvalue = 8.902
  Group = -> [Ni_element001]
  conduct = 2
  density = 1
  expand = 3
  formula = Ni
  name = G4_Ni
  specific = 4
FEATURE [App::DocumentObjectGroupPython] Cu_element001  label="Cu_element : 1"  # scripted group (container) (typed FeaturePython)
  n = 1
  ref = Cu_element
FEATURE [App::DocumentObjectGroupPython] G4_Cu  # scripted group (container) (typed FeaturePython)
  Dunit = g/cm3
  Dvalue = 8.96
  Group = -> [Cu_element001]
  conduct = 2
  density = 1
  expand = 3
  formula = Cu
  name = G4_Cu
  specific = 4
FEATURE [App::DocumentObjectGroupPython] Zn_element001  label="Zn_element : 1"  # scripted group (container) (typed FeaturePython)
  n = 1
  ref = Zn_element
FEATURE [App::DocumentObjectGroupPython] G4_Zn  # scripted group (container) (typed FeaturePython)
  Dunit = g/cm3
  Dvalue = 7.133
  Group = -> [Zn_element001]
  conduct = 2
  density = 1
  expand = 3
  formula = Zn
  name = G4_Zn
  specific = 4
FEATURE [App::DocumentObjectGroupPython] Ga_element002  label="Ga_element : 002"  # scripted group (container) (typed FeaturePython)
  n = 1
  ref = Ga_element
FEATURE [App::DocumentObjectGroupPython] G4_Ga  # scripted group (container) (typed FeaturePython)
  Dunit = g/cm3
  Dvalue = 5.904
  Group = -> [Ga_element002]
  conduct = 2
  density = 1
  expand = 3
  formula = Ga
  name = G4_Ga
  specific = 4
FEATURE [App::DocumentObjectGroupPython] Ge_element002  label="Ge_element : 1"  # scripted group (container) (typed FeaturePython)
  n = 1
  ref = Ge_element
FEATURE [App::DocumentObjectGroupPython] G4_Ge  # scripted group (container) (typed FeaturePython)
  Dunit = g/cm3
  Dvalue = 5.323
  Group = -> [Ge_element002]
  conduct = 2
  density = 1
  expand = 3
  formula = Ge
  name = G4_Ge
  specific = 4
FEATURE [App::DocumentObjectGroupPython] As_element003  label="As_element : 002"  # scripted group (container) (typed FeaturePython)
  n = 1
  ref = As_element
FEATURE [App::DocumentObjectGroupPython] G4_As  # scripted group (container) (typed FeaturePython)
  Dunit = g/cm3
  Dvalue = 5.73
  Group = -> [As_element003]
  conduct = 2
  density = 1
  expand = 3
  formula = As
  name = G4_As
  specific = 4
FEATURE [App::DocumentObjectGroupPython] Se_element001  label="Se_element : 1"  # scripted group (container) (typed FeaturePython)
  n = 1
  ref = Se_element
FEATURE [App::DocumentObjectGroupPython] G4_Se  # scripted group (container) (typed FeaturePython)
  Dunit = g/cm3
  Dvalue = 4.5
  Group = -> [Se_element001]
  conduct = 2
  density = 1
  expand = 3
  formula = Se
  name = G4_Se
  specific = 4
FEATURE [App::DocumentObjectGroupPython] Br_element007  label="Br_element : 004"  # scripted group (container) (typed FeaturePython)
  n = 1
  ref = Br_element
FEATURE [App::DocumentObjectGroupPython] G4_Br  # scripted group (container) (typed FeaturePython)
  Dunit = g/cm3
  Dvalue = 0.0070721
  Group = -> [Br_element007]
  conduct = 2
  density = 1
  expand = 3
  formula = Br
  name = G4_Br
  specific = 4
FEATURE [App::DocumentObjectGroupPython] Kr_element001  label="Kr_element : 1"  # scripted group (container) (typed FeaturePython)
  n = 1
  ref = Kr_element
FEATURE [App::DocumentObjectGroupPython] G4_Kr  # scripted group (container) (typed FeaturePython)
  Dunit = g/cm3
  Dvalue = 0.00347832
  Group = -> [Kr_element001]
  conduct = 2
  density = 1
  expand = 3
  formula = Kr
  name = G4_Kr
  specific = 4
FEATURE [App::DocumentObjectGroupPython] Rb_element001  label="Rb_element : 1"  # scripted group (container) (typed FeaturePython)
  n = 1
  ref = Rb_element
FEATURE [App::DocumentObjectGroupPython] G4_Rb  # scripted group (container) (typed FeaturePython)
  Dunit = g/cm3
  Dvalue = 1.532
  Group = -> [Rb_element001]
  conduct = 2
  density = 1
  expand = 3
  formula = Rb
  name = G4_Rb
  specific = 4
FEATURE [App::DocumentObjectGroupPython] Sr_element001  label="Sr_element : 1"  # scripted group (container) (typed FeaturePython)
  n = 1
  ref = Sr_element
FEATURE [App::DocumentObjectGroupPython] G4_Sr  # scripted group (container) (typed FeaturePython)
  Dunit = g/cm3
  Dvalue = 2.54
  Group = -> [Sr_element001]
  conduct = 2
  density = 1
  expand = 3
  formula = Sr
  name = G4_Sr
  specific = 4
FEATURE [App::DocumentObjectGroupPython] Y_element001  label="Y_element : 1"  # scripted group (container) (typed FeaturePython)
  n = 1
  ref = Y_element
FEATURE [App::DocumentObjectGroupPython] G4_Y  # scripted group (container) (typed FeaturePython)
  Dunit = g/cm3
  Dvalue = 4.469
  Group = -> [Y_element001]
  conduct = 2
  density = 1
  expand = 3
  formula = Y
  name = G4_Y
  specific = 4
FEATURE [App::DocumentObjectGroupPython] Zr_element001  label="Zr_element : 1"  # scripted group (container) (typed FeaturePython)
  n = 1
  ref = Zr_element
FEATURE [App::DocumentObjectGroupPython] G4_Zr  # scripted group (container) (typed FeaturePython)
  Dunit = g/cm3
  Dvalue = 6.506
  Group = -> [Zr_element001]
  conduct = 2
  density = 1
  expand = 3
  formula = Zr
  name = G4_Zr
  specific = 4
FEATURE [App::DocumentObjectGroupPython] Nb_element001  label="Nb_element : 1"  # scripted group (container) (typed FeaturePython)
  n = 1
  ref = Nb_element
FEATURE [App::DocumentObjectGroupPython] G4_Nb  # scripted group (container) (typed FeaturePython)
  Dunit = g/cm3
  Dvalue = 8.57
  Group = -> [Nb_element001]
  conduct = 2
  density = 1
  expand = 3
  formula = Nb
  name = G4_Nb
  specific = 4
FEATURE [App::DocumentObjectGroupPython] Mo_element001  label="Mo_element : 1"  # scripted group (container) (typed FeaturePython)
  n = 1
  ref = Mo_element
FEATURE [App::DocumentObjectGroupPython] G4_Mo  # scripted group (container) (typed FeaturePython)
  Dunit = g/cm3
  Dvalue = 10.22
  Group = -> [Mo_element001]
  conduct = 2
  density = 1
  expand = 3
  formula = Mo
  name = G4_Mo
  specific = 4
FEATURE [App::DocumentObjectGroupPython] Tc_element001  label="Tc_element : 1"  # scripted group (container) (typed FeaturePython)
  n = 1
  ref = Tc_element
FEATURE [App::DocumentObjectGroupPython] G4_Tc  # scripted group (container) (typed FeaturePython)
  Dunit = g/cm3
  Dvalue = 11.5
  Group = -> [Tc_element001]
  conduct = 2
  density = 1
  expand = 3
  formula = Tc
  name = G4_Tc
  specific = 4
FEATURE [App::DocumentObjectGroupPython] Ru_element001  label="Ru_element : 1"  # scripted group (container) (typed FeaturePython)
  n = 1
  ref = Ru_element
FEATURE [App::DocumentObjectGroupPython] G4_Ru  # scripted group (container) (typed FeaturePython)
  Dunit = g/cm3
  Dvalue = 12.41
  Group = -> [Ru_element001]
  conduct = 2
  density = 1
  expand = 3
  formula = Ru
  name = G4_Ru
  specific = 4
FEATURE [App::DocumentObjectGroupPython] Rh_element001  label="Rh_element : 1"  # scripted group (container) (typed FeaturePython)
  n = 1
  ref = Rh_element
FEATURE [App::DocumentObjectGroupPython] G4_Rh  # scripted group (container) (typed FeaturePython)
  Dunit = g/cm3
  Dvalue = 12.41
  Group = -> [Rh_element001]
  conduct = 2
  density = 1
  expand = 3
  formula = Rh
  name = G4_Rh
  specific = 4
FEATURE [App::DocumentObjectGroupPython] Pd_element001  label="Pd_element : 1"  # scripted group (container) (typed FeaturePython)
  n = 1
  ref = Pd_element
FEATURE [App::DocumentObjectGroupPython] G4_Pd  # scripted group (container) (typed FeaturePython)
  Dunit = g/cm3
  Dvalue = 12.02
  Group = -> [Pd_element001]
  conduct = 2
  density = 1
  expand = 3
  formula = Pd
  name = G4_Pd
  specific = 4
FEATURE [App::DocumentObjectGroupPython] Ag_element006  label="Ag_element : 004"  # scripted group (container) (typed FeaturePython)
  n = 1
  ref = Ag_element
FEATURE [App::DocumentObjectGroupPython] G4_Ag  # scripted group (container) (typed FeaturePython)
  Dunit = g/cm3
  Dvalue = 10.5
  Group = -> [Ag_element006]
  conduct = 2
  density = 1
  expand = 3
  formula = Ag
  name = G4_Ag
  specific = 4
FEATURE [App::DocumentObjectGroupPython] Cd_element003  label="Cd_element : 003"  # scripted group (container) (typed FeaturePython)
  n = 1
  ref = Cd_element
FEATURE [App::DocumentObjectGroupPython] G4_Cd  # scripted group (container) (typed FeaturePython)
  Dunit = g/cm3
  Dvalue = 8.65
  Group = -> [Cd_element003]
  conduct = 2
  density = 1
  expand = 3
  formula = Cd
  name = G4_Cd
  specific = 4
FEATURE [App::DocumentObjectGroupPython] In_element001  label="In_element : 1"  # scripted group (container) (typed FeaturePython)
  n = 1
  ref = In_element
FEATURE [App::DocumentObjectGroupPython] G4_In  # scripted group (container) (typed FeaturePython)
  Dunit = g/cm3
  Dvalue = 7.31
  Group = -> [In_element001]
  conduct = 2
  density = 1
  expand = 3
  formula = In
  name = G4_In
  specific = 4
FEATURE [App::DocumentObjectGroupPython] Sn_element001  label="Sn_element : 1"  # scripted group (container) (typed FeaturePython)
  n = 1
  ref = Sn_element
FEATURE [App::DocumentObjectGroupPython] G4_Sn  # scripted group (container) (typed FeaturePython)
  Dunit = g/cm3
  Dvalue = 7.31
  Group = -> [Sn_element001]
  conduct = 2
  density = 1
  expand = 3
  formula = Sn
  name = G4_Sn
  specific = 4
FEATURE [App::DocumentObjectGroupPython] Sb_element001  label="Sb_element : 1"  # scripted group (container) (typed FeaturePython)
  n = 1
  ref = Sb_element
FEATURE [App::DocumentObjectGroupPython] G4_Sb  # scripted group (container) (typed FeaturePython)
  Dunit = g/cm3
  Dvalue = 6.691
  Group = -> [Sb_element001]
  conduct = 2
  density = 1
  expand = 3
  formula = Sb
  name = G4_Sb
  specific = 4
FEATURE [App::DocumentObjectGroupPython] Te_element002  label="Te_element : 002"  # scripted group (container) (typed FeaturePython)
  n = 1
  ref = Te_element
FEATURE [App::DocumentObjectGroupPython] G4_Te  # scripted group (container) (typed FeaturePython)
  Dunit = g/cm3
  Dvalue = 6.24
  Group = -> [Te_element002]
  conduct = 2
  density = 1
  expand = 3
  formula = Te
  name = G4_Te
  specific = 4
FEATURE [App::DocumentObjectGroupPython] I_element010  label="I_element : 006"  # scripted group (container) (typed FeaturePython)
  n = 1
  ref = I_element
FEATURE [App::DocumentObjectGroupPython] G4_I  # scripted group (container) (typed FeaturePython)
  Dunit = g/cm3
  Dvalue = 4.93
  Group = -> [I_element010]
  conduct = 2
  density = 1
  expand = 3
  formula = I
  name = G4_I
  specific = 4
FEATURE [App::DocumentObjectGroupPython] Xe_element001  label="Xe_element : 1"  # scripted group (container) (typed FeaturePython)
  n = 1
  ref = Xe_element
FEATURE [App::DocumentObjectGroupPython] G4_Xe  # scripted group (container) (typed FeaturePython)
  Dunit = g/cm3
  Dvalue = 0.00548536
  Group = -> [Xe_element001]
  conduct = 2
  density = 1
  expand = 3
  formula = Xe
  name = G4_Xe
  specific = 4
FEATURE [App::DocumentObjectGroupPython] Cs_element003  label="Cs_element : 003"  # scripted group (container) (typed FeaturePython)
  n = 1
  ref = Cs_element
FEATURE [App::DocumentObjectGroupPython] G4_Cs  # scripted group (container) (typed FeaturePython)
  Dunit = g/cm3
  Dvalue = 1.873
  Group = -> [Cs_element003]
  conduct = 2
  density = 1
  expand = 3
  formula = Cs
  name = G4_Cs
  specific = 4
FEATURE [App::DocumentObjectGroupPython] Ba_element003  label="Ba_element : 003"  # scripted group (container) (typed FeaturePython)
  n = 1
  ref = Ba_element
FEATURE [App::DocumentObjectGroupPython] G4_Ba  # scripted group (container) (typed FeaturePython)
  Dunit = g/cm3
  Dvalue = 3.5
  Group = -> [Ba_element003]
  conduct = 2
  density = 1
  expand = 3
  formula = Ba
  name = G4_Ba
  specific = 4
FEATURE [App::DocumentObjectGroupPython] La_element003  label="La_element : 003"  # scripted group (container) (typed FeaturePython)
  n = 1
  ref = La_element
FEATURE [App::DocumentObjectGroupPython] G4_La  # scripted group (container) (typed FeaturePython)
  Dunit = g/cm3
  Dvalue = 6.154
  Group = -> [La_element003]
  conduct = 2
  density = 1
  expand = 3
  formula = La
  name = G4_La
  specific = 4
FEATURE [App::DocumentObjectGroupPython] Ce_element002  label="Ce_element : 1"  # scripted group (container) (typed FeaturePython)
  n = 1
  ref = Ce_element
FEATURE [App::DocumentObjectGroupPython] G4_Ce  # scripted group (container) (typed FeaturePython)
  Dunit = g/cm3
  Dvalue = 6.657
  Group = -> [Ce_element002]
  conduct = 2
  density = 1
  expand = 3
  formula = Ce
  name = G4_Ce
  specific = 4
FEATURE [App::DocumentObjectGroupPython] Pr_element001  label="Pr_element : 1"  # scripted group (container) (typed FeaturePython)
  n = 1
  ref = Pr_element
FEATURE [App::DocumentObjectGroupPython] G4_Pr  # scripted group (container) (typed FeaturePython)
  Dunit = g/cm3
  Dvalue = 6.71
  Group = -> [Pr_element001]
  conduct = 2
  density = 1
  expand = 3
  formula = Pr
  name = G4_Pr
  specific = 4
FEATURE [App::DocumentObjectGroupPython] Nd_element001  label="Nd_element : 1"  # scripted group (container) (typed FeaturePython)
  n = 1
  ref = Nd_element
FEATURE [App::DocumentObjectGroupPython] G4_Nd  # scripted group (container) (typed FeaturePython)
  Dunit = g/cm3
  Dvalue = 6.9
  Group = -> [Nd_element001]
  conduct = 2
  density = 1
  expand = 3
  formula = Nd
  name = G4_Nd
  specific = 4
FEATURE [App::DocumentObjectGroupPython] Pm_element001  label="Pm_element : 1"  # scripted group (container) (typed FeaturePython)
  n = 1
  ref = Pm_element
FEATURE [App::DocumentObjectGroupPython] G4_Pm  # scripted group (container) (typed FeaturePython)
  Dunit = g/cm3
  Dvalue = 7.22
  Group = -> [Pm_element001]
  conduct = 2
  density = 1
  expand = 3
  formula = Pm
  name = G4_Pm
  specific = 4
FEATURE [App::DocumentObjectGroupPython] Sm_element001  label="Sm_element : 1"  # scripted group (container) (typed FeaturePython)
  n = 1
  ref = Sm_element
FEATURE [App::DocumentObjectGroupPython] G4_Sm  # scripted group (container) (typed FeaturePython)
  Dunit = g/cm3
  Dvalue = 7.46
  Group = -> [Sm_element001]
  conduct = 2
  density = 1
  expand = 3
  formula = Sm
  name = G4_Sm
  specific = 4
FEATURE [App::DocumentObjectGroupPython] Eu_element001  label="Eu_element : 1"  # scripted group (container) (typed FeaturePython)
  n = 1
  ref = Eu_element
FEATURE [App::DocumentObjectGroupPython] G4_Eu  # scripted group (container) (typed FeaturePython)
  Dunit = g/cm3
  Dvalue = 5.243
  Group = -> [Eu_element001]
  conduct = 2
  density = 1
  expand = 3
  formula = Eu
  name = G4_Eu
  specific = 4
FEATURE [App::DocumentObjectGroupPython] Gd_element002  label="Gd_element : 1"  # scripted group (container) (typed FeaturePython)
  n = 1
  ref = Gd_element
FEATURE [App::DocumentObjectGroupPython] G4_Gd  # scripted group (container) (typed FeaturePython)
  Dunit = g/cm3
  Dvalue = 7.9004
  Group = -> [Gd_element002]
  conduct = 2
  density = 1
  expand = 3
  formula = Gd
  name = G4_Gd
  specific = 4
FEATURE [App::DocumentObjectGroupPython] Tb_element001  label="Tb_element : 1"  # scripted group (container) (typed FeaturePython)
  n = 1
  ref = Tb_element
FEATURE [App::DocumentObjectGroupPython] G4_Tb  # scripted group (container) (typed FeaturePython)
  Dunit = g/cm3
  Dvalue = 8.229
  Group = -> [Tb_element001]
  conduct = 2
  density = 1
  expand = 3
  formula = Tb
  name = G4_Tb
  specific = 4
FEATURE [App::DocumentObjectGroupPython] Dy_element001  label="Dy_element : 1"  # scripted group (container) (typed FeaturePython)
  n = 1
  ref = Dy_element
FEATURE [App::DocumentObjectGroupPython] G4_Dy  # scripted group (container) (typed FeaturePython)
  Dunit = g/cm3
  Dvalue = 8.55
  Group = -> [Dy_element001]
  conduct = 2
  density = 1
  expand = 3
  formula = Dy
  name = G4_Dy
  specific = 4
FEATURE [App::DocumentObjectGroupPython] Ho_element001  label="Ho_element : 1"  # scripted group (container) (typed FeaturePython)
  n = 1
  ref = Ho_element
FEATURE [App::DocumentObjectGroupPython] G4_Ho  # scripted group (container) (typed FeaturePython)
  Dunit = g/cm3
  Dvalue = 8.795
  Group = -> [Ho_element001]
  conduct = 2
  density = 1
  expand = 3
  formula = Ho
  name = G4_Ho
  specific = 4
FEATURE [App::DocumentObjectGroupPython] Er_element001  label="Er_element : 1"  # scripted group (container) (typed FeaturePython)
  n = 1
  ref = Er_element
FEATURE [App::DocumentObjectGroupPython] G4_Er  # scripted group (container) (typed FeaturePython)
  Dunit = g/cm3
  Dvalue = 9.066
  Group = -> [Er_element001]
  conduct = 2
  density = 1
  expand = 3
  formula = Er
  name = G4_Er
  specific = 4
FEATURE [App::DocumentObjectGroupPython] Tm_element001  label="Tm_element : 1"  # scripted group (container) (typed FeaturePython)
  n = 1
  ref = Tm_element
FEATURE [App::DocumentObjectGroupPython] G4_Tm  # scripted group (container) (typed FeaturePython)
  Dunit = g/cm3
  Dvalue = 9.321
  Group = -> [Tm_element001]
  conduct = 2
  density = 1
  expand = 3
  formula = Tm
  name = G4_Tm
  specific = 4
FEATURE [App::DocumentObjectGroupPython] Yb_element001  label="Yb_element : 1"  # scripted group (container) (typed FeaturePython)
  n = 1
  ref = Yb_element
FEATURE [App::DocumentObjectGroupPython] G4_Yb  # scripted group (container) (typed FeaturePython)
  Dunit = g/cm3
  Dvalue = 6.73
  Group = -> [Yb_element001]
  conduct = 2
  density = 1
  expand = 3
  formula = Yb
  name = G4_Yb
  specific = 4
FEATURE [App::DocumentObjectGroupPython] Lu_element001  label="Lu_element : 1"  # scripted group (container) (typed FeaturePython)
  n = 1
  ref = Lu_element
FEATURE [App::DocumentObjectGroupPython] G4_Lu  # scripted group (container) (typed FeaturePython)
  Dunit = g/cm3
  Dvalue = 9.84
  Group = -> [Lu_element001]
  conduct = 2
  density = 1
  expand = 3
  formula = Lu
  name = G4_Lu
  specific = 4
FEATURE [App::DocumentObjectGroupPython] Hf_element001  label="Hf_element : 1"  # scripted group (container) (typed FeaturePython)
  n = 1
  ref = Hf_element
FEATURE [App::DocumentObjectGroupPython] G4_Hf  # scripted group (container) (typed FeaturePython)
  Dunit = g/cm3
  Dvalue = 13.31
  Group = -> [Hf_element001]
  conduct = 2
  density = 1
  expand = 3
  formula = Hf
  name = G4_Hf
  specific = 4
FEATURE [App::DocumentObjectGroupPython] Ta_element001  label="Ta_element : 1"  # scripted group (container) (typed FeaturePython)
  n = 1
  ref = Ta_element
FEATURE [App::DocumentObjectGroupPython] G4_Ta  # scripted group (container) (typed FeaturePython)
  Dunit = g/cm3
  Dvalue = 16.654
  Group = -> [Ta_element001]
  conduct = 2
  density = 1
  expand = 3
  formula = Ta
  name = G4_Ta
  specific = 4
FEATURE [App::DocumentObjectGroupPython] W_element004  label="W_element : 004"  # scripted group (container) (typed FeaturePython)
  n = 1
  ref = W_element
FEATURE [App::DocumentObjectGroupPython] G4_W  # scripted group (container) (typed FeaturePython)
  Dunit = g/cm3
  Dvalue = 19.3
  Group = -> [W_element004]
  conduct = 2
  density = 1
  expand = 3
  formula = W
  name = G4_W
  specific = 4
FEATURE [App::DocumentObjectGroupPython] Re_element001  label="Re_element : 1"  # scripted group (container) (typed FeaturePython)
  n = 1
  ref = Re_element
FEATURE [App::DocumentObjectGroupPython] G4_Re  # scripted group (container) (typed FeaturePython)
  Dunit = g/cm3
  Dvalue = 21.02
  Group = -> [Re_element001]
  conduct = 2
  density = 1
  expand = 3
  formula = Re
  name = G4_Re
  specific = 4
FEATURE [App::DocumentObjectGroupPython] Os_element001  label="Os_element : 1"  # scripted group (container) (typed FeaturePython)
  n = 1
  ref = Os_element
FEATURE [App::DocumentObjectGroupPython] G4_Os  # scripted group (container) (typed FeaturePython)
  Dunit = g/cm3
  Dvalue = 22.57
  Group = -> [Os_element001]
  conduct = 2
  density = 1
  expand = 3
  formula = Os
  name = G4_Os
  specific = 4
FEATURE [App::DocumentObjectGroupPython] Ir_element001  label="Ir_element : 1"  # scripted group (container) (typed FeaturePython)
  n = 1
  ref = Ir_element
FEATURE [App::DocumentObjectGroupPython] G4_Ir  # scripted group (container) (typed FeaturePython)
  Dunit = g/cm3
  Dvalue = 22.42
  Group = -> [Ir_element001]
  conduct = 2
  density = 1
  expand = 3
  formula = Ir
  name = G4_Ir
  specific = 4
FEATURE [App::DocumentObjectGroupPython] Pt_element001  label="Pt_element : 1"  # scripted group (container) (typed FeaturePython)
  n = 1
  ref = Pt_element
FEATURE [App::DocumentObjectGroupPython] G4_Pt  # scripted group (container) (typed FeaturePython)
  Dunit = g/cm3
  Dvalue = 21.45
  Group = -> [Pt_element001]
  conduct = 2
  density = 1
  expand = 3
  formula = Pt
  name = G4_Pt
  specific = 4
FEATURE [App::DocumentObjectGroupPython] Au_element001  label="Au_element : 1"  # scripted group (container) (typed FeaturePython)
  n = 1
  ref = Au_element
FEATURE [App::DocumentObjectGroupPython] G4_Au  # scripted group (container) (typed FeaturePython)
  Dunit = g/cm3
  Dvalue = 19.32
  Group = -> [Au_element001]
  conduct = 2
  density = 1
  expand = 3
  formula = Au
  name = G4_Au
  specific = 4
FEATURE [App::DocumentObjectGroupPython] Hg_element002  label="Hg_element : 002"  # scripted group (container) (typed FeaturePython)
  n = 1
  ref = Hg_element
FEATURE [App::DocumentObjectGroupPython] G4_Hg  # scripted group (container) (typed FeaturePython)
  Dunit = g/cm3
  Dvalue = 13.546
  Group = -> [Hg_element002]
  conduct = 2
  density = 1
  expand = 3
  formula = Hg
  name = G4_Hg
  specific = 4
FEATURE [App::DocumentObjectGroupPython] Tl_element002  label="Tl_element : 002"  # scripted group (container) (typed FeaturePython)
  n = 1
  ref = Tl_element
FEATURE [App::DocumentObjectGroupPython] G4_Tl  # scripted group (container) (typed FeaturePython)
  Dunit = g/cm3
  Dvalue = 11.72
  Group = -> [Tl_element002]
  conduct = 2
  density = 1
  expand = 3
  formula = Tl
  name = G4_Tl
  specific = 4
FEATURE [App::DocumentObjectGroupPython] Pb_element003  label="Pb_element : 1"  # scripted group (container) (typed FeaturePython)
  n = 1
  ref = Pb_element
FEATURE [App::DocumentObjectGroupPython] G4_Pb  # scripted group (container) (typed FeaturePython)
  Dunit = g/cm3
  Dvalue = 11.35
  Group = -> [Pb_element003]
  conduct = 2
  density = 1
  expand = 3
  formula = Pb
  name = G4_Pb
  specific = 4
FEATURE [App::DocumentObjectGroupPython] Bi_element002  label="Bi_element : 1"  # scripted group (container) (typed FeaturePython)
  n = 1
  ref = Bi_element
FEATURE [App::DocumentObjectGroupPython] G4_Bi  # scripted group (container) (typed FeaturePython)
  Dunit = g/cm3
  Dvalue = 9.747
  Group = -> [Bi_element002]
  conduct = 2
  density = 1
  expand = 3
  formula = Bi
  name = G4_Bi
  specific = 4
FEATURE [App::DocumentObjectGroupPython] Po_element001  label="Po_element : 1"  # scripted group (container) (typed FeaturePython)
  n = 1
  ref = Po_element
FEATURE [App::DocumentObjectGroupPython] G4_Po  # scripted group (container) (typed FeaturePython)
  Dunit = g/cm3
  Dvalue = 9.32
  Group = -> [Po_element001]
  conduct = 2
  density = 1
  expand = 3
  formula = Po
  name = G4_Po
  specific = 4
FEATURE [App::DocumentObjectGroupPython] At_element001  label="At_element : 1"  # scripted group (container) (typed FeaturePython)
  n = 1
  ref = At_element
FEATURE [App::DocumentObjectGroupPython] G4_At  # scripted group (container) (typed FeaturePython)
  Dunit = g/cm3
  Dvalue = 9.32
  Group = -> [At_element001]
  conduct = 2
  density = 1
  expand = 3
  formula = At
  name = G4_At
  specific = 4
FEATURE [App::DocumentObjectGroupPython] Rn_element001  label="Rn_element : 1"  # scripted group (container) (typed FeaturePython)
  n = 1
  ref = Rn_element
FEATURE [App::DocumentObjectGroupPython] G4_Rn  # scripted group (container) (typed FeaturePython)
  Dunit = g/cm3
  Dvalue = 0.00900662
  Group = -> [Rn_element001]
  conduct = 2
  density = 1
  expand = 3
  formula = Rn
  name = G4_Rn
  specific = 4
FEATURE [App::DocumentObjectGroupPython] Fr_element001  label="Fr_element : 1"  # scripted group (container) (typed FeaturePython)
  n = 1
  ref = Fr_element
FEATURE [App::DocumentObjectGroupPython] G4_Fr  # scripted group (container) (typed FeaturePython)
  Dunit = g/cm3
  Dvalue = 1
  Group = -> [Fr_element001]
  conduct = 2
  density = 1
  expand = 3
  formula = Fr
  name = G4_Fr
  specific = 4
FEATURE [App::DocumentObjectGroupPython] Ra_element001  label="Ra_element : 1"  # scripted group (container) (typed FeaturePython)
  n = 1
  ref = Ra_element
FEATURE [App::DocumentObjectGroupPython] G4_Ra  # scripted group (container) (typed FeaturePython)
  Dunit = g/cm3
  Dvalue = 5
  Group = -> [Ra_element001]
  conduct = 2
  density = 1
  expand = 3
  formula = Ra
  name = G4_Ra
  specific = 4
FEATURE [App::DocumentObjectGroupPython] Ac_element001  label="Ac_element : 1"  # scripted group (container) (typed FeaturePython)
  n = 1
  ref = Ac_element
FEATURE [App::DocumentObjectGroupPython] G4_Ac  # scripted group (container) (typed FeaturePython)
  Dunit = g/cm3
  Dvalue = 10.07
  Group = -> [Ac_element001]
  conduct = 2
  density = 1
  expand = 3
  formula = Ac
  name = G4_Ac
  specific = 4
FEATURE [App::DocumentObjectGroupPython] Th_element001  label="Th_element : 1"  # scripted group (container) (typed FeaturePython)
  n = 1
  ref = Th_element
FEATURE [App::DocumentObjectGroupPython] G4_Th  # scripted group (container) (typed FeaturePython)
  Dunit = g/cm3
  Dvalue = 11.72
  Group = -> [Th_element001]
  conduct = 2
  density = 1
  expand = 3
  formula = Th
  name = G4_Th
  specific = 4
FEATURE [App::DocumentObjectGroupPython] Pa_element001  label="Pa_element : 1"  # scripted group (container) (typed FeaturePython)
  n = 1
  ref = Pa_element
FEATURE [App::DocumentObjectGroupPython] G4_Pa  # scripted group (container) (typed FeaturePython)
  Dunit = g/cm3
  Dvalue = 15.37
  Group = -> [Pa_element001]
  conduct = 2
  density = 1
  expand = 3
  formula = Pa
  name = G4_Pa
  specific = 4
FEATURE [App::DocumentObjectGroupPython] U_element004  label="U_element : 004"  # scripted group (container) (typed FeaturePython)
  n = 1
  ref = U_element
FEATURE [App::DocumentObjectGroupPython] G4_U  # scripted group (container) (typed FeaturePython)
  Dunit = g/cm3
  Dvalue = 18.95
  Group = -> [U_element004]
  conduct = 2
  density = 1
  expand = 3
  formula = U
  name = G4_U
  specific = 4
FEATURE [App::DocumentObjectGroupPython] Np_element001  label="Np_element : 1"  # scripted group (container) (typed FeaturePython)
  n = 1
  ref = Np_element
FEATURE [App::DocumentObjectGroupPython] G4_Np  # scripted group (container) (typed FeaturePython)
  Dunit = g/cm3
  Dvalue = 20.25
  Group = -> [Np_element001]
  conduct = 2
  density = 1
  expand = 3
  formula = Np
  name = G4_Np
  specific = 4
FEATURE [App::DocumentObjectGroupPython] Pu_element002  label="Pu_element : 002"  # scripted group (container) (typed FeaturePython)
  n = 1
  ref = Pu_element
FEATURE [App::DocumentObjectGroupPython] G4_Pu  # scripted group (container) (typed FeaturePython)
  Dunit = g/cm3
  Dvalue = 19.84
  Group = -> [Pu_element002]
  conduct = 2
  density = 1
  expand = 3
  formula = Pu
  name = G4_Pu
  specific = 4
FEATURE [App::DocumentObjectGroupPython] Am_element001  label="Am_element : 1"  # scripted group (container) (typed FeaturePython)
  n = 1
  ref = Am_element
FEATURE [App::DocumentObjectGroupPython] G4_Am  # scripted group (container) (typed FeaturePython)
  Dunit = g/cm3
  Dvalue = 13.67
  Group = -> [Am_element001]
  conduct = 2
  density = 1
  expand = 3
  formula = Am
  name = G4_Am
  specific = 4
FEATURE [App::DocumentObjectGroupPython] Cm_element001  label="Cm_element : 1"  # scripted group (container) (typed FeaturePython)
  n = 1
  ref = Cm_element
FEATURE [App::DocumentObjectGroupPython] G4_Cm  # scripted group (container) (typed FeaturePython)
  Dunit = g/cm3
  Dvalue = 13.51
  Group = -> [Cm_element001]
  conduct = 2
  density = 1
  expand = 3
  formula = Cm
  name = G4_Cm
  specific = 4
FEATURE [App::DocumentObjectGroupPython] Bk_element001  label="Bk_element : 1"  # scripted group (container) (typed FeaturePython)
  n = 1
  ref = Bk_element
FEATURE [App::DocumentObjectGroupPython] G4_Bk  # scripted group (container) (typed FeaturePython)
  Dunit = g/cm3
  Dvalue = 14
  Group = -> [Bk_element001]
  conduct = 2
  density = 1
  expand = 3
  formula = Bk
  name = G4_Bk
  specific = 4
FEATURE [App::DocumentObjectGroupPython] Cf_element001  label="Cf_element : 1"  # scripted group (container) (typed FeaturePython)
  n = 1
  ref = Cf_element
FEATURE [App::DocumentObjectGroupPython] G4_Cf  # scripted group (container) (typed FeaturePython)
  Dunit = g/cm3
  Dvalue = 10
  Group = -> [Cf_element001]
  conduct = 2
  density = 1
  expand = 3
  formula = Cf
  name = G4_Cf
  specific = 4
FEATURE [App::DocumentObjectGroupPython] Element  # scripted group (container) (typed FeaturePython)
  Group = -> [G4_H,G4_He,G4_Li,G4_Be,G4_B,G4_C,G4_N,G4_O,G4_F,G4_Ne,G4_Na,G4_Mg,G4_Al,G4_Si,G4_P,G4_S,G4_Cl,G4_Ar,G4_K,G4_Ca,G4_Sc,G4_Ti,G4_V,G4_Cr,G4_Mn,G4_Fe,G4_Co,G4_Ni,G4_Cu,G4_Zn,G4_Ga,G4_Ge,G4_As,G4_Se,G4_Br,G4_Kr,G4_Rb,G4_Sr,G4_Y,G4_Zr,G4_Nb,G4_Mo,G4_Tc,G4_Ru,G4_Rh,G4_Pd,G4_Ag,G4_Cd,G4_In,G4_Sn,G4_Sb,G4_Te,G4_I,G4_Xe,G4_Cs,G4_Ba,G4_La,G4_Ce,G4_Pr,G4_Nd,G4_Pm,G4_Sm,G4_Eu,G4_Gd,G4_Tb,G4_Dy,G4_Ho,G4_Er,+30 more]
FEATURE [App::DocumentObjectGroupPython] H_element114  label="H_element : 063"  # scripted group (container) (typed FeaturePython)
  n = 2
  ref = H_element
FEATURE [App::DocumentObjectGroupPython] G4_lH2  # scripted group (container) (typed FeaturePython)
  Dunit = g/cm3
  Dvalue = 0.0708
  Group = -> [H_element114]
  conduct = 2
  density = 1
  expand = 3
  formula = G4_lH2
  name = G4_lH2
  specific = 4
FEATURE [App::DocumentObjectGroupPython] N_element049  label="N_element : 022"  # scripted group (container) (typed FeaturePython)
  n = 2
  ref = N_element
FEATURE [App::DocumentObjectGroupPython] G4_lN2  # scripted group (container) (typed FeaturePython)
  Dunit = g/cm3
  Dvalue = 0.807
  Group = -> [N_element049]
  conduct = 2
  density = 1
  expand = 3
  formula = G4_lN2
  name = G4_lN2
  specific = 4
FEATURE [App::DocumentObjectGroupPython] O_element106  label="O_element : 060"  # scripted group (container) (typed FeaturePython)
  n = 2
  ref = O_element
FEATURE [App::DocumentObjectGroupPython] G4_lO2  # scripted group (container) (typed FeaturePython)
  Dunit = g/cm3
  Dvalue = 1.141
  Group = -> [O_element106]
  conduct = 2
  density = 1
  expand = 3
  formula = G4_lO2
  name = G4_lO2
  specific = 4
FEATURE [App::DocumentObjectGroupPython] Ar  label="Ar : 1"  # scripted group (container) (typed FeaturePython)
  n = 1
  ref = Ar
FEATURE [App::DocumentObjectGroupPython] G4_lAr  # scripted group (container) (typed FeaturePython)
  Dunit = g/cm3
  Dvalue = 1.396
  Group = -> [Ar]
  conduct = 2
  density = 1
  expand = 3
  formula = G4_lAr
  name = G4_lAr
  specific = 4
FEATURE [App::DocumentObjectGroupPython] Br  label="Br : 1"  # scripted group (container) (typed FeaturePython)
  n = 1
  ref = Br
FEATURE [App::DocumentObjectGroupPython] G4_lBr  # scripted group (container) (typed FeaturePython)
  Dunit = g/cm3
  Dvalue = 3.1028
  Group = -> [Br]
  conduct = 2
  density = 1
  expand = 3
  formula = G4_lBr
  name = G4_lBr
  specific = 4
FEATURE [App::DocumentObjectGroupPython] Kr  label="Kr : 1"  # scripted group (container) (typed FeaturePython)
  n = 1
  ref = Kr
FEATURE [App::DocumentObjectGroupPython] G4_lKr  # scripted group (container) (typed FeaturePython)
  Dunit = g/cm3
  Dvalue = 2.418
  Group = -> [Kr]
  conduct = 2
  density = 1
  expand = 3
  formula = G4_lKr
  name = G4_lKr
  specific = 4
FEATURE [App::DocumentObjectGroupPython] Xe  label="Xe : 1"  # scripted group (container) (typed FeaturePython)
  n = 1
  ref = Xe
FEATURE [App::DocumentObjectGroupPython] G4_lXe  # scripted group (container) (typed FeaturePython)
  Dunit = g/cm3
  Dvalue = 2.953
  Group = -> [Xe]
  conduct = 2
  density = 1
  expand = 3
  formula = G4_lXe
  name = G4_lXe
  specific = 4
FEATURE [App::DocumentObjectGroupPython] O_element107  label="O_element : 061"  # scripted group (container) (typed FeaturePython)
  n = 4
  ref = O_element
FEATURE [App::DocumentObjectGroupPython] Pb_element004  label="Pb_element : 002"  # scripted group (container) (typed FeaturePython)
  n = 1
  ref = Pb_element
FEATURE [App::DocumentObjectGroupPython] W_element005  label="W_element : 005"  # scripted group (container) (typed FeaturePython)
  n = 1
  ref = W_element
FEATURE [App::DocumentObjectGroupPython] G4_PbWO4  # scripted group (container) (typed FeaturePython)
  Dunit = g/cm3
  Dvalue = 8.28
  Group = -> [O_element107,Pb_element004,W_element005]
  conduct = 2
  density = 1
  expand = 3
  formula = G4_PbWO4
  name = G4_PbWO4
  specific = 4
FEATURE [App::DocumentObjectGroupPython] alactic  label="alactic : 1"  # scripted group (container) (typed FeaturePython)
  n = 1
  ref = alactic
FEATURE [App::DocumentObjectGroupPython] G4_Galactic  # scripted group (container) (typed FeaturePython)
  Dunit = g/cm3
  Dvalue = 0
  Group = -> [alactic]
  conduct = 2
  density = 1
  expand = 3
  formula = G4_Galactic
  name = G4_Galactic
  specific = 4
FEATURE [App::DocumentObjectGroupPython] RAPHITE_POROUS  label="RAPHITE_POROUS : 1"  # scripted group (container) (typed FeaturePython)
  n = 1
  ref = RAPHITE_POROUS
FEATURE [App::DocumentObjectGroupPython] G4_GRAPHITE_POROUS  # scripted group (container) (typed FeaturePython)
  Dunit = g/cm3
  Dvalue = 1.7
  Group = -> [RAPHITE_POROUS]
  conduct = 2
  density = 1
  expand = 3
  formula = G4_GRAPHITE_POROUS
  name = G4_GRAPHITE_POROUS
  specific = 4
FEATURE [App::DocumentObjectGroupPython] H_element115  label="H_element : 0.150"  # scripted group (container) (typed FeaturePython)
  n = 0.080538
FEATURE [App::DocumentObjectGroupPython] C_element125  label="C_element : 0.600"  # scripted group (container) (typed FeaturePython)
  n = 0.599848
FEATURE [App::DocumentObjectGroupPython] O_element108  label="O_element : 0.320"  # scripted group (container) (typed FeaturePython)
  n = 0.319614
FEATURE [App::DocumentObjectGroupPython] G4_LUCITE  # scripted group (container) (typed FeaturePython)
  Dunit = g/cm3
  Dvalue = 1.19
  Group = -> [H_element115,C_element125,O_element108]
  conduct = 2
  density = 1
  expand = 3
  formula = G4_LUCITE
  name = G4_LUCITE
  specific = 4
FEATURE [App::DocumentObjectGroupPython] Cu_element002  label="Cu_element : 62"  # scripted group (container) (typed FeaturePython)
  n = 62
  ref = Cu_element
FEATURE [App::DocumentObjectGroupPython] Zn_element002  label="Zn_element : 35"  # scripted group (container) (typed FeaturePython)
  n = 35
  ref = Zn_element
FEATURE [App::DocumentObjectGroupPython] Pb_element005  label="Pb_element : 3"  # scripted group (container) (typed FeaturePython)
  n = 3
  ref = Pb_element
FEATURE [App::DocumentObjectGroupPython] G4_BRASS  # scripted group (container) (typed FeaturePython)
  Dunit = g/cm3
  Dvalue = 8.52
  Group = -> [Cu_element002,Zn_element002,Pb_element005]
  conduct = 2
  density = 1
  expand = 3
  formula = G4_BRASS
  name = G4_BRASS
  specific = 4
FEATURE [App::DocumentObjectGroupPython] Cu_element003  label="Cu_element : 89"  # scripted group (container) (typed FeaturePython)
  n = 89
  ref = Cu_element
FEATURE [App::DocumentObjectGroupPython] Zn_element003  label="Zn_element : 9"  # scripted group (container) (typed FeaturePython)
  n = 9
  ref = Zn_element
FEATURE [App::DocumentObjectGroupPython] Pb_element006  label="Pb_element : 2"  # scripted group (container) (typed FeaturePython)
  n = 2
  ref = Pb_element
FEATURE [App::DocumentObjectGroupPython] G4_BRONZE  # scripted group (container) (typed FeaturePython)
  Dunit = g/cm3
  Dvalue = 8.82
  Group = -> [Cu_element003,Zn_element003,Pb_element006]
  conduct = 2
  density = 1
  expand = 3
  formula = G4_BRONZE
  name = G4_BRONZE
  specific = 4
FEATURE [App::DocumentObjectGroupPython] Fe_element008  label="Fe_element : 74"  # scripted group (container) (typed FeaturePython)
  n = 74
  ref = Fe_element
FEATURE [App::DocumentObjectGroupPython] Cr_element002  label="Cr_element : 18"  # scripted group (container) (typed FeaturePython)
  n = 18
  ref = Cr_element
FEATURE [App::DocumentObjectGroupPython] Ni_element002  label="Ni_element : 8"  # scripted group (container) (typed FeaturePython)
  n = 8
  ref = Ni_element
FEATURE [App::DocumentObjectGroupPython] G4_STAINLESS_STEEL  label="G4_STAINLESS-STEEL"  # scripted group (container) (typed FeaturePython)
  Dunit = g/cm3
  Dvalue = 8
  Group = -> [Fe_element008,Cr_element002,Ni_element002]
  conduct = 2
  density = 1
  expand = 3
  formula = G4_STAINLESS-STEEL
  name = G4_STAINLESS-STEEL
  specific = 4
FEATURE [App::DocumentObjectGroupPython] H_element116  label="H_element : 064"  # scripted group (container) (typed FeaturePython)
  n = 18
  ref = H_element
FEATURE [App::DocumentObjectGroupPython] C_element126  label="C_element : 071"  # scripted group (container) (typed FeaturePython)
  n = 12
  ref = C_element
FEATURE [App::DocumentObjectGroupPython] O_element109  label="O_element : 062"  # scripted group (container) (typed FeaturePython)
  n = 7
  ref = O_element
FEATURE [App::DocumentObjectGroupPython] G4_CR39  # scripted group (container) (typed FeaturePython)
  Dunit = g/cm3
  Dvalue = 1.32
  Group = -> [H_element116,C_element126,O_element109]
  conduct = 2
  density = 1
  expand = 3
  formula = G4_CR39
  name = G4_CR39
  specific = 4
FEATURE [App::DocumentObjectGroupPython] H_element117  label="H_element : 38"  # scripted group (container) (typed FeaturePython)
  n = 38
  ref = H_element
FEATURE [App::DocumentObjectGroupPython] C_element127  label="C_element : 072"  # scripted group (container) (typed FeaturePython)
  n = 18
  ref = C_element
FEATURE [App::DocumentObjectGroupPython] O_element110  label="O_element : 063"  # scripted group (container) (typed FeaturePython)
  n = 1
  ref = O_element
FEATURE [App::DocumentObjectGroupPython] G4_OCTADECANOL  # scripted group (container) (typed FeaturePython)
  Dunit = g/cm3
  Dvalue = 0.812
  Group = -> [H_element117,C_element127,O_element110]
  conduct = 2
  density = 1
  expand = 3
  formula = G4_OCTADECANOL
  name = G4_OCTADECANOL
  specific = 4
FEATURE [App::DocumentObjectGroupPython] HEP  # scripted group (container) (typed FeaturePython)
  Group = -> [G4_lH2,G4_lN2,G4_lO2,G4_lAr,G4_lBr,G4_lKr,G4_lXe,G4_PbWO4,G4_Galactic,G4_GRAPHITE_POROUS,G4_LUCITE,G4_BRASS,G4_BRONZE,G4_STAINLESS_STEEL,G4_CR39,G4_OCTADECANOL]
FEATURE [App::DocumentObjectGroupPython] C_element128  label="C_element : 073"  # scripted group (container) (typed FeaturePython)
  n = 14
  ref = C_element
FEATURE [App::DocumentObjectGroupPython] H_element118  label="H_element : 065"  # scripted group (container) (typed FeaturePython)
  n = 10
  ref = H_element
FEATURE [App::DocumentObjectGroupPython] O_element111  label="O_element : 064"  # scripted group (container) (typed FeaturePython)
  n = 2
  ref = O_element
FEATURE [App::DocumentObjectGroupPython] N_element050  label="N_element : 023"  # scripted group (container) (typed FeaturePython)
  n = 2
  ref = N_element
FEATURE [App::DocumentObjectGroupPython] G4_KEVLAR  # scripted group (container) (typed FeaturePython)
  Dunit = g/cm3
  Dvalue = 1.44
  Group = -> [C_element128,H_element118,O_element111,N_element050]
  conduct = 2
  density = 1
  expand = 3
  formula = G4_KEVLAR
  name = G4_KEVLAR
  specific = 4
FEATURE [App::DocumentObjectGroupPython] C_element129  label="C_element : 074"  # scripted group (container) (typed FeaturePython)
  n = 10
  ref = C_element
FEATURE [App::DocumentObjectGroupPython] H_element119  label="H_element : 066"  # scripted group (container) (typed FeaturePython)
  n = 8
  ref = H_element
FEATURE [App::DocumentObjectGroupPython] O_element112  label="O_element : 065"  # scripted group (container) (typed FeaturePython)
  n = 4
  ref = O_element
FEATURE [App::DocumentObjectGroupPython] G4_DACRON  # scripted group (container) (typed FeaturePython)
  Dunit = g/cm3
  Dvalue = 1.4
  Group = -> [C_element129,H_element119,O_element112]
  conduct = 2
  density = 1
  expand = 3
  formula = G4_DACRON
  name = G4_DACRON
  specific = 4
FEATURE [App::DocumentObjectGroupPython] C_element130  label="C_element : 075"  # scripted group (container) (typed FeaturePython)
  n = 4
  ref = C_element
FEATURE [App::DocumentObjectGroupPython] H_element120  label="H_element : 067"  # scripted group (container) (typed FeaturePython)
  n = 5
  ref = H_element
FEATURE [App::DocumentObjectGroupPython] Cl_element030  label="Cl_element : 016"  # scripted group (container) (typed FeaturePython)
  n = 1
  ref = Cl_element
FEATURE [App::DocumentObjectGroupPython] G4_NEOPRENE  # scripted group (container) (typed FeaturePython)
  Dunit = g/cm3
  Dvalue = 1.23
  Group = -> [C_element130,H_element120,Cl_element030]
  conduct = 2
  density = 1
  expand = 3
  formula = G4_NEOPRENE
  name = G4_NEOPRENE
  specific = 4
FEATURE [App::DocumentObjectGroupPython] Space  # scripted group (container) (typed FeaturePython)
  Group = -> [G4_KEVLAR,G4_DACRON,G4_NEOPRENE]
FEATURE [App::DocumentObjectGroupPython] H_element121  label="H_element : 068"  # scripted group (container) (typed FeaturePython)
  n = 5
  ref = H_element
FEATURE [App::DocumentObjectGroupPython] C_element131  label="C_element : 076"  # scripted group (container) (typed FeaturePython)
  n = 4
  ref = C_element
FEATURE [App::DocumentObjectGroupPython] N_element051  label="N_element : 3"  # scripted group (container) (typed FeaturePython)
  n = 3
  ref = N_element
FEATURE [App::DocumentObjectGroupPython] O_element113  label="O_element : 066"  # scripted group (container) (typed FeaturePython)
  n = 1
  ref = O_element
FEATURE [App::DocumentObjectGroupPython] G4_CYTOSINE  # scripted group (container) (typed FeaturePython)
  Dunit = g/cm3
  Dvalue = 1.55
  Group = -> [H_element121,C_element131,N_element051,O_element113]
  conduct = 2
  density = 1
  expand = 3
  formula = G4_CYTOSINE
  name = G4_CYTOSINE
  specific = 4
FEATURE [App::DocumentObjectGroupPython] H_element122  label="H_element : 069"  # scripted group (container) (typed FeaturePython)
  n = 6
  ref = H_element
FEATURE [App::DocumentObjectGroupPython] C_element132  label="C_element : 077"  # scripted group (container) (typed FeaturePython)
  n = 5
  ref = C_element
FEATURE [App::DocumentObjectGroupPython] N_element052  label="N_element : 024"  # scripted group (container) (typed FeaturePython)
  n = 2
  ref = N_element
FEATURE [App::DocumentObjectGroupPython] O_element114  label="O_element : 067"  # scripted group (container) (typed FeaturePython)
  n = 2
  ref = O_element
FEATURE [App::DocumentObjectGroupPython] G4_THYMINE  # scripted group (container) (typed FeaturePython)
  Dunit = g/cm3
  Dvalue = 1.23
  Group = -> [H_element122,C_element132,N_element052,O_element114]
  conduct = 2
  density = 1
  expand = 3
  formula = G4_THYMINE
  name = G4_THYMINE
  specific = 4
FEATURE [App::DocumentObjectGroupPython] H_element123  label="H_element : 070"  # scripted group (container) (typed FeaturePython)
  n = 4
  ref = H_element
FEATURE [App::DocumentObjectGroupPython] C_element133  label="C_element : 078"  # scripted group (container) (typed FeaturePython)
  n = 4
  ref = C_element
FEATURE [App::DocumentObjectGroupPython] N_element053  label="N_element : 025"  # scripted group (container) (typed FeaturePython)
  n = 2
  ref = N_element
FEATURE [App::DocumentObjectGroupPython] O_element115  label="O_element : 068"  # scripted group (container) (typed FeaturePython)
  n = 2
  ref = O_element
FEATURE [App::DocumentObjectGroupPython] G4_URACIL  # scripted group (container) (typed FeaturePython)
  Dunit = g/cm3
  Dvalue = 1.32
  Group = -> [H_element123,C_element133,N_element053,O_element115]
  conduct = 2
  density = 1
  expand = 3
  formula = G4_URACIL
  name = G4_URACIL
  specific = 4
FEATURE [App::DocumentObjectGroupPython] H_element124  label="H_element : 071"  # scripted group (container) (typed FeaturePython)
  n = 4
  ref = H_element
FEATURE [App::DocumentObjectGroupPython] C_element134  label="C_element : 079"  # scripted group (container) (typed FeaturePython)
  n = 5
  ref = C_element
FEATURE [App::DocumentObjectGroupPython] N_element054  label="N_element : 026"  # scripted group (container) (typed FeaturePython)
  n = 5
  ref = N_element
FEATURE [App::DocumentObjectGroupPython] G4_DNA_ADENINE  # scripted group (container) (typed FeaturePython)
  Dunit = g/cm3
  Dvalue = 1
  Group = -> [H_element124,C_element134,N_element054]
  conduct = 2
  density = 1
  expand = 3
  formula = G4_DNA_ADENINE
  name = G4_DNA_ADENINE
  specific = 4
FEATURE [App::DocumentObjectGroupPython] H_element125  label="H_element : 072"  # scripted group (container) (typed FeaturePython)
  n = 4
  ref = H_element
FEATURE [App::DocumentObjectGroupPython] C_element135  label="C_element : 080"  # scripted group (container) (typed FeaturePython)
  n = 5
  ref = C_element
FEATURE [App::DocumentObjectGroupPython] N_element055  label="N_element : 027"  # scripted group (container) (typed FeaturePython)
  n = 5
  ref = N_element
FEATURE [App::DocumentObjectGroupPython] O_element116  label="O_element : 069"  # scripted group (container) (typed FeaturePython)
  n = 1
  ref = O_element
FEATURE [App::DocumentObjectGroupPython] G4_DNA_GUANINE  # scripted group (container) (typed FeaturePython)
  Dunit = g/cm3
  Dvalue = 1
  Group = -> [H_element125,C_element135,N_element055,O_element116]
  conduct = 2
  density = 1
  expand = 3
  formula = G4_DNA_GUANINE
  name = G4_DNA_GUANINE
  specific = 4
FEATURE [App::DocumentObjectGroupPython] H_element126  label="H_element : 073"  # scripted group (container) (typed FeaturePython)
  n = 4
  ref = H_element
FEATURE [App::DocumentObjectGroupPython] C_element136  label="C_element : 081"  # scripted group (container) (typed FeaturePython)
  n = 4
  ref = C_element
FEATURE [App::DocumentObjectGroupPython] N_element056  label="N_element : 028"  # scripted group (container) (typed FeaturePython)
  n = 3
  ref = N_element
FEATURE [App::DocumentObjectGroupPython] O_element117  label="O_element : 070"  # scripted group (container) (typed FeaturePython)
  n = 1
  ref = O_element
FEATURE [App::DocumentObjectGroupPython] G4_DNA_CYTOSINE  # scripted group (container) (typed FeaturePython)
  Dunit = g/cm3
  Dvalue = 1
  Group = -> [H_element126,C_element136,N_element056,O_element117]
  conduct = 2
  density = 1
  expand = 3
  formula = G4_DNA_CYTOSINE
  name = G4_DNA_CYTOSINE
  specific = 4
FEATURE [App::DocumentObjectGroupPython] H_element127  label="H_element : 074"  # scripted group (container) (typed FeaturePython)
  n = 5
  ref = H_element
FEATURE [App::DocumentObjectGroupPython] C_element137  label="C_element : 082"  # scripted group (container) (typed FeaturePython)
  n = 5
  ref = C_element
FEATURE [App::DocumentObjectGroupPython] N_element057  label="N_element : 029"  # scripted group (container) (typed FeaturePython)
  n = 2
  ref = N_element
FEATURE [App::DocumentObjectGroupPython] O_element118  label="O_element : 071"  # scripted group (container) (typed FeaturePython)
  n = 2
  ref = O_element
FEATURE [App::DocumentObjectGroupPython] G4_DNA_THYMINE  # scripted group (container) (typed FeaturePython)
  Dunit = g/cm3
  Dvalue = 1
  Group = -> [H_element127,C_element137,N_element057,O_element118]
  conduct = 2
  density = 1
  expand = 3
  formula = G4_DNA_THYMINE
  name = G4_DNA_THYMINE
  specific = 4
FEATURE [App::DocumentObjectGroupPython] H_element128  label="H_element : 075"  # scripted group (container) (typed FeaturePython)
  n = 3
  ref = H_element
FEATURE [App::DocumentObjectGroupPython] C_element138  label="C_element : 083"  # scripted group (container) (typed FeaturePython)
  n = 4
  ref = C_element
FEATURE [App::DocumentObjectGroupPython] N_element058  label="N_element : 030"  # scripted group (container) (typed FeaturePython)
  n = 2
  ref = N_element
FEATURE [App::DocumentObjectGroupPython] O_element119  label="O_element : 072"  # scripted group (container) (typed FeaturePython)
  n = 2
  ref = O_element
FEATURE [App::DocumentObjectGroupPython] G4_DNA_URACIL  # scripted group (container) (typed FeaturePython)
  Dunit = g/cm3
  Dvalue = 1
  Group = -> [H_element128,C_element138,N_element058,O_element119]
  conduct = 2
  density = 1
  expand = 3
  formula = G4_DNA_URACIL
  name = G4_DNA_URACIL
  specific = 4
FEATURE [App::DocumentObjectGroupPython] H_element129  label="H_element : 076"  # scripted group (container) (typed FeaturePython)
  n = 10
  ref = H_element
FEATURE [App::DocumentObjectGroupPython] C_element139  label="C_element : 084"  # scripted group (container) (typed FeaturePython)
  n = 10
  ref = C_element
FEATURE [App::DocumentObjectGroupPython] N_element059  label="N_element : 031"  # scripted group (container) (typed FeaturePython)
  n = 5
  ref = N_element
FEATURE [App::DocumentObjectGroupPython] O_element120  label="O_element : 073"  # scripted group (container) (typed FeaturePython)
  n = 4
  ref = O_element
FEATURE [App::DocumentObjectGroupPython] G4_DNA_ADENOSINE  # scripted group (container) (typed FeaturePython)
  Dunit = g/cm3
  Dvalue = 1
  Group = -> [H_element129,C_element139,N_element059,O_element120]
  conduct = 2
  density = 1
  expand = 3
  formula = G4_DNA_ADENOSINE
  name = G4_DNA_ADENOSINE
  specific = 4
FEATURE [App::DocumentObjectGroupPython] H_element130  label="H_element : 077"  # scripted group (container) (typed FeaturePython)
  n = 10
  ref = H_element
FEATURE [App::DocumentObjectGroupPython] C_element140  label="C_element : 085"  # scripted group (container) (typed FeaturePython)
  n = 10
  ref = C_element
FEATURE [App::DocumentObjectGroupPython] N_element060  label="N_element : 032"  # scripted group (container) (typed FeaturePython)
  n = 5
  ref = N_element
FEATURE [App::DocumentObjectGroupPython] O_element121  label="O_element : 074"  # scripted group (container) (typed FeaturePython)
  n = 5
  ref = O_element
FEATURE [App::DocumentObjectGroupPython] G4_DNA_GUANOSINE  # scripted group (container) (typed FeaturePython)
  Dunit = g/cm3
  Dvalue = 1
  Group = -> [H_element130,C_element140,N_element060,O_element121]
  conduct = 2
  density = 1
  expand = 3
  formula = G4_DNA_GUANOSINE
  name = G4_DNA_GUANOSINE
  specific = 4
FEATURE [App::DocumentObjectGroupPython] H_element131  label="H_element : 078"  # scripted group (container) (typed FeaturePython)
  n = 10
  ref = H_element
FEATURE [App::DocumentObjectGroupPython] C_element141  label="C_element : 086"  # scripted group (container) (typed FeaturePython)
  n = 9
  ref = C_element
FEATURE [App::DocumentObjectGroupPython] N_element061  label="N_element : 033"  # scripted group (container) (typed FeaturePython)
  n = 3
  ref = N_element
FEATURE [App::DocumentObjectGroupPython] O_element122  label="O_element : 075"  # scripted group (container) (typed FeaturePython)
  n = 5
  ref = O_element
FEATURE [App::DocumentObjectGroupPython] G4_DNA_CYTIDINE  # scripted group (container) (typed FeaturePython)
  Dunit = g/cm3
  Dvalue = 1
  Group = -> [H_element131,C_element141,N_element061,O_element122]
  conduct = 2
  density = 1
  expand = 3
  formula = G4_DNA_CYTIDINE
  name = G4_DNA_CYTIDINE
  specific = 4
FEATURE [App::DocumentObjectGroupPython] H_element132  label="H_element : 079"  # scripted group (container) (typed FeaturePython)
  n = 9
  ref = H_element
FEATURE [App::DocumentObjectGroupPython] C_element142  label="C_element : 087"  # scripted group (container) (typed FeaturePython)
  n = 9
  ref = C_element
FEATURE [App::DocumentObjectGroupPython] N_element062  label="N_element : 034"  # scripted group (container) (typed FeaturePython)
  n = 2
  ref = N_element
FEATURE [App::DocumentObjectGroupPython] O_element123  label="O_element : 076"  # scripted group (container) (typed FeaturePython)
  n = 6
  ref = O_element
FEATURE [App::DocumentObjectGroupPython] G4_DNA_URIDINE  # scripted group (container) (typed FeaturePython)
  Dunit = g/cm3
  Dvalue = 1
  Group = -> [H_element132,C_element142,N_element062,O_element123]
  conduct = 2
  density = 1
  expand = 3
  formula = G4_DNA_URIDINE
  name = G4_DNA_URIDINE
  specific = 4
FEATURE [App::DocumentObjectGroupPython] H_element133  label="H_element : 080"  # scripted group (container) (typed FeaturePython)
  n = 11
  ref = H_element
FEATURE [App::DocumentObjectGroupPython] C_element143  label="C_element : 088"  # scripted group (container) (typed FeaturePython)
  n = 10
  ref = C_element
FEATURE [App::DocumentObjectGroupPython] N_element063  label="N_element : 035"  # scripted group (container) (typed FeaturePython)
  n = 2
  ref = N_element
FEATURE [App::DocumentObjectGroupPython] O_element124  label="O_element : 077"  # scripted group (container) (typed FeaturePython)
  n = 6
  ref = O_element
FEATURE [App::DocumentObjectGroupPython] G4_DNA_METHYLURIDINE  # scripted group (container) (typed FeaturePython)
  Dunit = g/cm3
  Dvalue = 1
  Group = -> [H_element133,C_element143,N_element063,O_element124]
  conduct = 2
  density = 1
  expand = 3
  formula = G4_DNA_METHYLURIDINE
  name = G4_DNA_METHYLURIDINE
  specific = 4
FEATURE [App::DocumentObjectGroupPython] P_element014  label="P_element : 003"  # scripted group (container) (typed FeaturePython)
  n = 1
  ref = P_element
FEATURE [App::DocumentObjectGroupPython] O_element125  label="O_element : 078"  # scripted group (container) (typed FeaturePython)
  n = 3
  ref = O_element
FEATURE [App::DocumentObjectGroupPython] G4_DNA_MONOPHOSPHATE  # scripted group (container) (typed FeaturePython)
  Dunit = g/cm3
  Dvalue = 1
  Group = -> [P_element014,O_element125]
  conduct = 2
  density = 1
  expand = 3
  formula = G4_DNA_MONOPHOSPHATE
  name = G4_DNA_MONOPHOSPHATE
  specific = 4
FEATURE [App::DocumentObjectGroupPython] H_element134  label="H_element : 081"  # scripted group (container) (typed FeaturePython)
  n = 10
  ref = H_element
FEATURE [App::DocumentObjectGroupPython] C_element144  label="C_element : 089"  # scripted group (container) (typed FeaturePython)
  n = 10
  ref = C_element
FEATURE [App::DocumentObjectGroupPython] N_element064  label="N_element : 036"  # scripted group (container) (typed FeaturePython)
  n = 5
  ref = N_element
FEATURE [App::DocumentObjectGroupPython] O_element126  label="O_element : 079"  # scripted group (container) (typed FeaturePython)
  n = 7
  ref = O_element
FEATURE [App::DocumentObjectGroupPython] P_element015  label="P_element : 004"  # scripted group (container) (typed FeaturePython)
  n = 1
  ref = P_element
FEATURE [App::DocumentObjectGroupPython] G4_DNA_A  # scripted group (container) (typed FeaturePython)
  Dunit = g/cm3
  Dvalue = 1
  Group = -> [H_element134,C_element144,N_element064,O_element126,P_element015]
  conduct = 2
  density = 1
  expand = 3
  formula = G4_DNA_A
  name = G4_DNA_A
  specific = 4
FEATURE [App::DocumentObjectGroupPython] H_element135  label="H_element : 082"  # scripted group (container) (typed FeaturePython)
  n = 10
  ref = H_element
FEATURE [App::DocumentObjectGroupPython] C_element145  label="C_element : 090"  # scripted group (container) (typed FeaturePython)
  n = 10
  ref = C_element
FEATURE [App::DocumentObjectGroupPython] N_element065  label="N_element : 037"  # scripted group (container) (typed FeaturePython)
  n = 5
  ref = N_element
FEATURE [App::DocumentObjectGroupPython] O_element127  label="O_element : 8"  # scripted group (container) (typed FeaturePython)
  n = 8
  ref = O_element
FEATURE [App::DocumentObjectGroupPython] P_element016  label="P_element : 005"  # scripted group (container) (typed FeaturePython)
  n = 1
  ref = P_element
FEATURE [App::DocumentObjectGroupPython] G4_DNA_G  # scripted group (container) (typed FeaturePython)
  Dunit = g/cm3
  Dvalue = 1
  Group = -> [H_element135,C_element145,N_element065,O_element127,P_element016]
  conduct = 2
  density = 1
  expand = 3
  formula = G4_DNA_G
  name = G4_DNA_G
  specific = 4
FEATURE [App::DocumentObjectGroupPython] H_element136  label="H_element : 083"  # scripted group (container) (typed FeaturePython)
  n = 10
  ref = H_element
FEATURE [App::DocumentObjectGroupPython] C_element146  label="C_element : 091"  # scripted group (container) (typed FeaturePython)
  n = 9
  ref = C_element
FEATURE [App::DocumentObjectGroupPython] N_element066  label="N_element : 038"  # scripted group (container) (typed FeaturePython)
  n = 3
  ref = N_element
FEATURE [App::DocumentObjectGroupPython] O_element128  label="O_element : 080"  # scripted group (container) (typed FeaturePython)
  n = 8
  ref = O_element
FEATURE [App::DocumentObjectGroupPython] P_element017  label="P_element : 006"  # scripted group (container) (typed FeaturePython)
  n = 1
  ref = P_element
FEATURE [App::DocumentObjectGroupPython] G4_DNA_C  # scripted group (container) (typed FeaturePython)
  Dunit = g/cm3
  Dvalue = 1
  Group = -> [H_element136,C_element146,N_element066,O_element128,P_element017]
  conduct = 2
  density = 1
  expand = 3
  formula = G4_DNA_C
  name = G4_DNA_C
  specific = 4
FEATURE [App::DocumentObjectGroupPython] H_element137  label="H_element : 084"  # scripted group (container) (typed FeaturePython)
  n = 9
  ref = H_element
FEATURE [App::DocumentObjectGroupPython] C_element147  label="C_element : 092"  # scripted group (container) (typed FeaturePython)
  n = 9
  ref = C_element
FEATURE [App::DocumentObjectGroupPython] N_element067  label="N_element : 039"  # scripted group (container) (typed FeaturePython)
  n = 2
  ref = N_element
FEATURE [App::DocumentObjectGroupPython] O_element129  label="O_element : 9"  # scripted group (container) (typed FeaturePython)
  n = 9
  ref = O_element
FEATURE [App::DocumentObjectGroupPython] P_element018  label="P_element : 007"  # scripted group (container) (typed FeaturePython)
  n = 1
  ref = P_element
FEATURE [App::DocumentObjectGroupPython] G4_DNA_U  # scripted group (container) (typed FeaturePython)
  Dunit = g/cm3
  Dvalue = 1
  Group = -> [H_element137,C_element147,N_element067,O_element129,P_element018]
  conduct = 2
  density = 1
  expand = 3
  formula = G4_DNA_U
  name = G4_DNA_U
  specific = 4
FEATURE [App::DocumentObjectGroupPython] H_element138  label="H_element : 085"  # scripted group (container) (typed FeaturePython)
  n = 11
  ref = H_element
FEATURE [App::DocumentObjectGroupPython] C_element148  label="C_element : 093"  # scripted group (container) (typed FeaturePython)
  n = 10
  ref = C_element
FEATURE [App::DocumentObjectGroupPython] N_element068  label="N_element : 040"  # scripted group (container) (typed FeaturePython)
  n = 2
  ref = N_element
FEATURE [App::DocumentObjectGroupPython] O_element130  label="O_element : 081"  # scripted group (container) (typed FeaturePython)
  n = 9
  ref = O_element
FEATURE [App::DocumentObjectGroupPython] P_element019  label="P_element : 008"  # scripted group (container) (typed FeaturePython)
  n = 1
  ref = P_element
FEATURE [App::DocumentObjectGroupPython] G4_DNA_MU  # scripted group (container) (typed FeaturePython)
  Dunit = g/cm3
  Dvalue = 1
  Group = -> [H_element138,C_element148,N_element068,O_element130,P_element019]
  conduct = 2
  density = 1
  expand = 3
  formula = G4_DNA_MU
  name = G4_DNA_MU
  specific = 4
FEATURE [App::DocumentObjectGroupPython] BioChemical  # scripted group (container) (typed FeaturePython)
  Group = -> [G4_CYTOSINE,G4_THYMINE,G4_URACIL,G4_DNA_ADENINE,G4_DNA_GUANINE,G4_DNA_CYTOSINE,G4_DNA_THYMINE,G4_DNA_URACIL,G4_DNA_ADENOSINE,G4_DNA_GUANOSINE,G4_DNA_CYTIDINE,G4_DNA_URIDINE,G4_DNA_METHYLURIDINE,G4_DNA_MONOPHOSPHATE,G4_DNA_A,G4_DNA_G,G4_DNA_C,G4_DNA_U,G4_DNA_MU]
FEATURE [App::DocumentObjectGroupPython] G4Materials  # scripted group (container) (typed FeaturePython)
  Group = -> [NIST,Element,HEP,Space,BioChemical]
  version = 1
FEATURE [App::DocumentObjectGroupPython] Geant4  # scripted group (container) (typed FeaturePython)
  Group = -> [G4Isotopes,G4Elements,G4Materials]
FEATURE [App::DocumentObjectGroupPython] Materials  # scripted group (container) (typed FeaturePython)
  Group = -> [Geant4]
FEATURE [Part::FeaturePython] GDMLBox_WorldBox  # WARN: FeaturePython — macro-defined, semantics opaque (R4)
  lunit = 2
  material = 5
  x = 52
  y = 52
  z = 13
FEATURE [Part::FeaturePython] GDMLBox_Box  # WARN: FeaturePython — macro-defined, semantics opaque (R4)
  lunit = 2
  material = 0
  x = 10
  y = 10
  z = 10
FEATURE [Part::FeaturePython] GDMLSphere  # WARN: FeaturePython — macro-defined, semantics opaque (R4)
  aunit = 1
  deltaphi = 360
  deltatheta = 180
  lunit = 2
  material = 285
  rmax = 3
  rmin = 0
  startphi = 0
  starttheta = 0
FEATURE [Part::FeaturePython] Array  # Draft array (typed FeaturePython)
  AlwaysSyncPlacement = false
  Angle = 360
  ArrayType = 0
  Axis = (0,0,1)
  Base = -> GDMLBox_Box
  Center = (0,0,0)
  Count = 4
  ExpandArray = false
  Fuse = false
  IntervalAxis = (0,0,0)
  IntervalX = (15,0,0)
  IntervalY = (0,15,0)
  IntervalZ = (0,0,100)
  NumberCircles = 3
  NumberPolar = 5
  NumberX = 2
  NumberY = 2
  NumberZ = 1
  PlacementList = 4 placements: [(0,0,0),(0,15,0),(15,0,0),(15,15,0)]
  RadialDistance = 50
  ScaleList = (4) [(1,1,1),(1,1,1),(1,1,1),(1,1,1)]
  Symmetry = 1
  TangentialDistance = 25
FEATURE [Part::FeaturePython] Array001  # Draft array (typed FeaturePython)
  AlwaysSyncPlacement = false
  Angle = 360
  ArrayType = 0
  Axis = (0,0,1)
  Base = -> GDMLSphere
  Center = (0,0,0)
  Count = 4
  ExpandArray = false
  Fuse = false
  IntervalAxis = (0,0,0)
  IntervalX = (15,0,0)
  IntervalY = (0,15,0)
  IntervalZ = (0,0,100)
  NumberCircles = 3
  NumberPolar = 5
  NumberX = 2
  NumberY = 2
  NumberZ = 1
  PlacementList = 4 placements: [(0,0,0),(0,15,0),(15,0,0),(15,15,0)]
  RadialDistance = 50
  ScaleList = (4) [(1,1,1),(1,1,1),(1,1,1),(1,1,1)]
  Symmetry = 1
  TangentialDistance = 25
FEATURE [App::Part] Part001
  Group = -> [GDMLSphere,Array001]
  Origin = -> Origin002
FEATURE [App::Part] Part
  Group = -> [GDMLBox_Box,Array,Part001]
  Origin = -> Origin001
FEATURE [App::Part] worldVOL
  Group = -> [GDMLBox_WorldBox,Part]
  Origin = -> Origin
